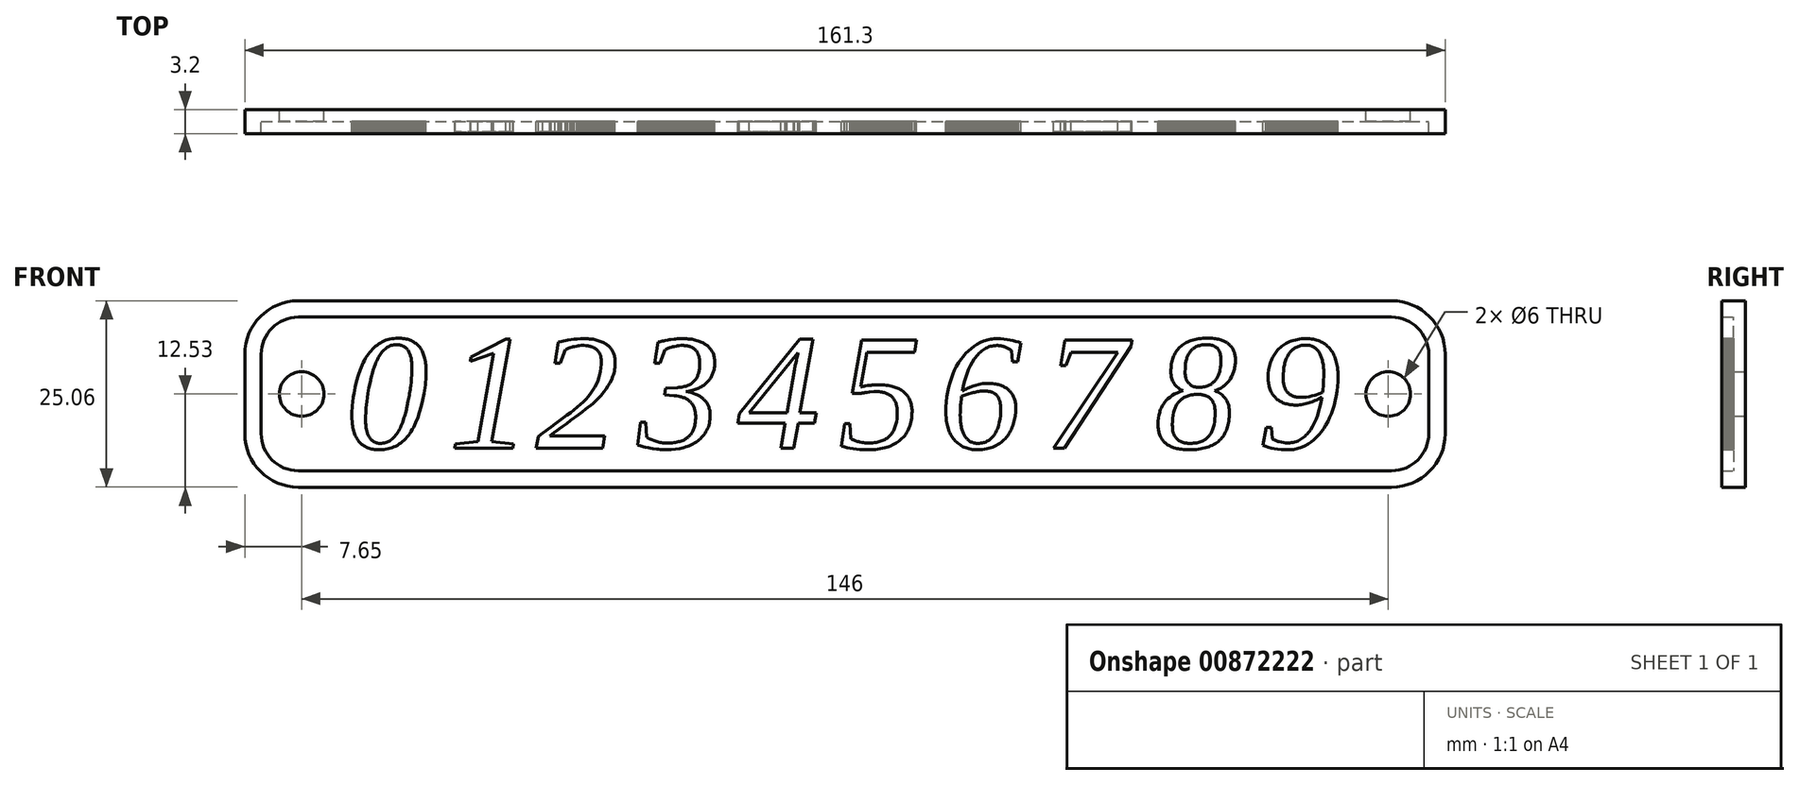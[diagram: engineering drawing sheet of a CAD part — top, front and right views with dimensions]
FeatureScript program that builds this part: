
annotation { "Feature Type Name" : "Feature", "Feature Type Description" : "" }
export const myFeature = defineFeature(function(context is Context, id is Id, definition is map)
    precondition{}
    {
        {
            var Q0;
            Q0=qCreatedBy(makeId("Front.planeOp"),FACE);
            var sketch = newSketch(context, id + "F0", { "sketchPlane" : qUnion([Q0])});
            skLineSegment(sketch, "E0", {"start": v(-109.12, 0) * mm, "end": v(57, 0) * mm, "construction": true});
            skPoint(sketch, "E0.startSnap0", {"position": v(-80, 0) * mm});
            skPoint(sketch, "E0.endSnap0", {"position": v(24, 0) * mm});
            skCircle(sketch, "E1", {"center": v(-73, 0) * mm, "radius": 3 * mm});
            skCircle(sketch, "E2", {"center": v(73, 0) * mm, "radius": 3 * mm});
            skLineSegment(sketch, "E3", {"start": v(-56.56, 0.05) * mm, "end": v(-56.74, -0.83) * mm});
            skLineSegment(sketch, "E4", {"start": v(-56.74, -0.83) * mm, "end": v(-56.94, -1.67) * mm});
            skLineSegment(sketch, "E5", {"start": v(-56.94, -1.67) * mm, "end": v(-57.16, -2.45) * mm});
            skLineSegment(sketch, "E6", {"start": v(-57.16, -2.45) * mm, "end": v(-57.4, -3.18) * mm});
            skLineSegment(sketch, "E7", {"start": v(-57.4, -3.18) * mm, "end": v(-57.68, -3.86) * mm});
            skLineSegment(sketch, "E8", {"start": v(-57.68, -3.86) * mm, "end": v(-57.82, -4.18) * mm});
            skLineSegment(sketch, "E9", {"start": v(-57.82, -4.18) * mm, "end": v(-57.98, -4.48) * mm});
            skLineSegment(sketch, "E10", {"start": v(-57.98, -4.48) * mm, "end": v(-58.13, -4.77) * mm});
            skLineSegment(sketch, "E11", {"start": v(-58.13, -4.77) * mm, "end": v(-58.3, -5.05) * mm});
            skLineSegment(sketch, "E12", {"start": v(-58.3, -5.05) * mm, "end": v(-58.48, -5.3) * mm});
            skLineSegment(sketch, "E13", {"start": v(-58.48, -5.3) * mm, "end": v(-58.66, -5.56) * mm});
            skLineSegment(sketch, "E14", {"start": v(-58.66, -5.56) * mm, "end": v(-58.84, -5.79) * mm});
            skLineSegment(sketch, "E15", {"start": v(-58.84, -5.79) * mm, "end": v(-59.04, -6) * mm});
            skLineSegment(sketch, "E16", {"start": v(-59.04, -6) * mm, "end": v(-59.24, -6.2) * mm});
            skLineSegment(sketch, "E17", {"start": v(-59.24, -6.2) * mm, "end": v(-59.45, -6.4) * mm});
            skLineSegment(sketch, "E18", {"start": v(-59.45, -6.4) * mm, "end": v(-59.67, -6.57) * mm});
            skLineSegment(sketch, "E19", {"start": v(-59.67, -6.57) * mm, "end": v(-59.9, -6.73) * mm});
            skLineSegment(sketch, "E20", {"start": v(-59.9, -6.73) * mm, "end": v(-60.13, -6.88) * mm});
            skLineSegment(sketch, "E21", {"start": v(-60.13, -6.88) * mm, "end": v(-60.37, -7.01) * mm});
            skLineSegment(sketch, "E22", {"start": v(-60.37, -7.01) * mm, "end": v(-60.62, -7.13) * mm});
            skLineSegment(sketch, "E23", {"start": v(-60.62, -7.13) * mm, "end": v(-60.87, -7.23) * mm});
            skLineSegment(sketch, "E24", {"start": v(-60.87, -7.23) * mm, "end": v(-61.13, -7.3) * mm});
            skLineSegment(sketch, "E25", {"start": v(-61.13, -7.3) * mm, "end": v(-61.4, -7.38) * mm});
            skLineSegment(sketch, "E26", {"start": v(-61.4, -7.38) * mm, "end": v(-61.68, -7.43) * mm});
            skLineSegment(sketch, "E27", {"start": v(-61.68, -7.43) * mm, "end": v(-61.97, -7.47) * mm});
            skLineSegment(sketch, "E28", {"start": v(-61.97, -7.47) * mm, "end": v(-62.26, -7.5) * mm});
            skLineSegment(sketch, "E29", {"start": v(-62.26, -7.5) * mm, "end": v(-62.56, -7.5) * mm});
            skLineSegment(sketch, "E30", {"start": v(-62.56, -7.5) * mm, "end": v(-62.79, -7.5) * mm});
            skLineSegment(sketch, "E31", {"start": v(-62.79, -7.5) * mm, "end": v(-63, -7.48) * mm});
            skLineSegment(sketch, "E32", {"start": v(-63, -7.48) * mm, "end": v(-63.2, -7.46) * mm});
            skLineSegment(sketch, "E33", {"start": v(-63.2, -7.46) * mm, "end": v(-63.41, -7.43) * mm});
            skLineSegment(sketch, "E34", {"start": v(-63.41, -7.43) * mm, "end": v(-63.6, -7.4) * mm});
            skLineSegment(sketch, "E35", {"start": v(-63.6, -7.4) * mm, "end": v(-63.8, -7.34) * mm});
            skLineSegment(sketch, "E36", {"start": v(-63.8, -7.34) * mm, "end": v(-63.98, -7.29) * mm});
            skLineSegment(sketch, "E37", {"start": v(-63.98, -7.29) * mm, "end": v(-64.15, -7.22) * mm});
            skLineSegment(sketch, "E38", {"start": v(-64.15, -7.22) * mm, "end": v(-64.32, -7.15) * mm});
            skLineSegment(sketch, "E39", {"start": v(-64.32, -7.15) * mm, "end": v(-64.48, -7.06) * mm});
            skLineSegment(sketch, "E40", {"start": v(-64.48, -7.06) * mm, "end": v(-64.64, -6.97) * mm});
            skLineSegment(sketch, "E41", {"start": v(-64.64, -6.97) * mm, "end": v(-64.78, -6.87) * mm});
            skLineSegment(sketch, "E42", {"start": v(-64.78, -6.87) * mm, "end": v(-64.93, -6.76) * mm});
            skLineSegment(sketch, "E43", {"start": v(-64.93, -6.76) * mm, "end": v(-65.06, -6.64) * mm});
            skLineSegment(sketch, "E44", {"start": v(-65.06, -6.64) * mm, "end": v(-65.19, -6.52) * mm});
            skLineSegment(sketch, "E45", {"start": v(-65.19, -6.52) * mm, "end": v(-65.3, -6.38) * mm});
            skLineSegment(sketch, "E46", {"start": v(-65.3, -6.38) * mm, "end": v(-65.42, -6.24) * mm});
            skLineSegment(sketch, "E47", {"start": v(-65.42, -6.24) * mm, "end": v(-65.53, -6.08) * mm});
            skLineSegment(sketch, "E48", {"start": v(-65.53, -6.08) * mm, "end": v(-65.63, -5.92) * mm});
            skLineSegment(sketch, "E49", {"start": v(-65.63, -5.92) * mm, "end": v(-65.72, -5.74) * mm});
            skLineSegment(sketch, "E50", {"start": v(-65.72, -5.74) * mm, "end": v(-65.8, -5.56) * mm});
            skLineSegment(sketch, "E51", {"start": v(-65.8, -5.56) * mm, "end": v(-65.88, -5.37) * mm});
            skLineSegment(sketch, "E52", {"start": v(-65.88, -5.37) * mm, "end": v(-65.95, -5.17) * mm});
            skLineSegment(sketch, "E53", {"start": v(-65.95, -5.17) * mm, "end": v(-66.02, -4.96) * mm});
            skLineSegment(sketch, "E54", {"start": v(-66.02, -4.96) * mm, "end": v(-66.07, -4.74) * mm});
            skLineSegment(sketch, "E55", {"start": v(-66.07, -4.74) * mm, "end": v(-66.12, -4.51) * mm});
            skLineSegment(sketch, "E56", {"start": v(-66.12, -4.51) * mm, "end": v(-66.16, -4.28) * mm});
            skLineSegment(sketch, "E57", {"start": v(-66.16, -4.28) * mm, "end": v(-66.2, -4.03) * mm});
            skLineSegment(sketch, "E58", {"start": v(-66.2, -4.03) * mm, "end": v(-66.22, -3.77) * mm});
            skLineSegment(sketch, "E59", {"start": v(-66.22, -3.77) * mm, "end": v(-66.25, -3.24) * mm});
            skLineSegment(sketch, "E60", {"start": v(-66.25, -3.24) * mm, "end": v(-66.25, -2.95) * mm});
            skLineSegment(sketch, "E61", {"start": v(-66.25, -2.95) * mm, "end": v(-66.25, -2.62) * mm});
            skLineSegment(sketch, "E62", {"start": v(-66.25, -2.62) * mm, "end": v(-66.24, -2.28) * mm});
            skLineSegment(sketch, "E63", {"start": v(-66.24, -2.28) * mm, "end": v(-66.22, -1.92) * mm});
            skLineSegment(sketch, "E64", {"start": v(-66.22, -1.92) * mm, "end": v(-66.19, -1.54) * mm});
            skLineSegment(sketch, "E65", {"start": v(-66.19, -1.54) * mm, "end": v(-66.15, -1.15) * mm});
            skLineSegment(sketch, "E66", {"start": v(-66.15, -1.15) * mm, "end": v(-66.05, -0.35) * mm});
            skLineSegment(sketch, "E67", {"start": v(-66.05, -0.35) * mm, "end": v(-65.98, 0.05) * mm});
            skLineSegment(sketch, "E68", {"start": v(-65.98, 0.05) * mm, "end": v(-65.8, 0.93) * mm});
            skLineSegment(sketch, "E69", {"start": v(-65.8, 0.93) * mm, "end": v(-65.6, 1.75) * mm});
            skLineSegment(sketch, "E70", {"start": v(-65.6, 1.75) * mm, "end": v(-65.38, 2.52) * mm});
            skLineSegment(sketch, "E71", {"start": v(-65.38, 2.52) * mm, "end": v(-65.14, 3.25) * mm});
            skLineSegment(sketch, "E72", {"start": v(-65.14, 3.25) * mm, "end": v(-64.86, 3.91) * mm});
            skLineSegment(sketch, "E73", {"start": v(-64.86, 3.91) * mm, "end": v(-64.71, 4.22) * mm});
            skLineSegment(sketch, "E74", {"start": v(-64.71, 4.22) * mm, "end": v(-64.56, 4.52) * mm});
            skLineSegment(sketch, "E75", {"start": v(-64.56, 4.52) * mm, "end": v(-64.4, 4.8) * mm});
            skLineSegment(sketch, "E76", {"start": v(-64.4, 4.8) * mm, "end": v(-64.23, 5.08) * mm});
            skLineSegment(sketch, "E77", {"start": v(-64.23, 5.08) * mm, "end": v(-64.06, 5.34) * mm});
            skLineSegment(sketch, "E78", {"start": v(-64.06, 5.34) * mm, "end": v(-63.88, 5.58) * mm});
            skLineSegment(sketch, "E79", {"start": v(-63.88, 5.58) * mm, "end": v(-63.69, 5.8) * mm});
            skLineSegment(sketch, "E80", {"start": v(-63.69, 5.8) * mm, "end": v(-63.5, 6.02) * mm});
            skLineSegment(sketch, "E81", {"start": v(-63.5, 6.02) * mm, "end": v(-63.3, 6.22) * mm});
            skLineSegment(sketch, "E82", {"start": v(-63.3, 6.22) * mm, "end": v(-63.08, 6.4) * mm});
            skLineSegment(sketch, "E83", {"start": v(-63.08, 6.4) * mm, "end": v(-62.87, 6.58) * mm});
            skLineSegment(sketch, "E84", {"start": v(-62.87, 6.58) * mm, "end": v(-62.65, 6.74) * mm});
            skLineSegment(sketch, "E85", {"start": v(-62.65, 6.74) * mm, "end": v(-62.42, 6.88) * mm});
            skLineSegment(sketch, "E86", {"start": v(-62.42, 6.88) * mm, "end": v(-62.18, 7.01) * mm});
            skLineSegment(sketch, "E87", {"start": v(-62.18, 7.01) * mm, "end": v(-61.94, 7.13) * mm});
            skLineSegment(sketch, "E88", {"start": v(-61.94, 7.13) * mm, "end": v(-61.7, 7.23) * mm});
            skLineSegment(sketch, "E89", {"start": v(-61.7, 7.23) * mm, "end": v(-61.43, 7.3) * mm});
            skLineSegment(sketch, "E90", {"start": v(-61.43, 7.3) * mm, "end": v(-61.17, 7.38) * mm});
            skLineSegment(sketch, "E91", {"start": v(-61.17, 7.38) * mm, "end": v(-60.9, 7.43) * mm});
            skLineSegment(sketch, "E92", {"start": v(-60.9, 7.43) * mm, "end": v(-60.62, 7.47) * mm});
            skLineSegment(sketch, "E93", {"start": v(-60.62, 7.47) * mm, "end": v(-60.33, 7.5) * mm});
            skLineSegment(sketch, "E94", {"start": v(-60.33, 7.5) * mm, "end": v(-60.03, 7.5) * mm});
            skLineSegment(sketch, "E95", {"start": v(-60.03, 7.5) * mm, "end": v(-59.81, 7.5) * mm});
            skLineSegment(sketch, "E96", {"start": v(-59.81, 7.5) * mm, "end": v(-59.6, 7.48) * mm});
            skLineSegment(sketch, "E97", {"start": v(-59.6, 7.48) * mm, "end": v(-59.39, 7.46) * mm});
            skLineSegment(sketch, "E98", {"start": v(-59.39, 7.46) * mm, "end": v(-59.19, 7.43) * mm});
            skLineSegment(sketch, "E99", {"start": v(-59.19, 7.43) * mm, "end": v(-58.99, 7.4) * mm});
            skLineSegment(sketch, "E100", {"start": v(-58.99, 7.4) * mm, "end": v(-58.8, 7.35) * mm});
            skLineSegment(sketch, "E101", {"start": v(-58.8, 7.35) * mm, "end": v(-58.62, 7.3) * mm});
            skLineSegment(sketch, "E102", {"start": v(-58.62, 7.3) * mm, "end": v(-58.44, 7.23) * mm});
            skLineSegment(sketch, "E103", {"start": v(-58.44, 7.23) * mm, "end": v(-58.27, 7.16) * mm});
            skLineSegment(sketch, "E104", {"start": v(-58.27, 7.16) * mm, "end": v(-58.1, 7.08) * mm});
            skLineSegment(sketch, "E105", {"start": v(-58.1, 7.08) * mm, "end": v(-57.95, 6.99) * mm});
            skLineSegment(sketch, "E106", {"start": v(-57.95, 6.99) * mm, "end": v(-57.8, 6.89) * mm});
            skLineSegment(sketch, "E107", {"start": v(-57.8, 6.89) * mm, "end": v(-57.65, 6.78) * mm});
            skLineSegment(sketch, "E108", {"start": v(-57.65, 6.78) * mm, "end": v(-57.51, 6.67) * mm});
            skLineSegment(sketch, "E109", {"start": v(-57.51, 6.67) * mm, "end": v(-57.38, 6.55) * mm});
            skLineSegment(sketch, "E110", {"start": v(-57.38, 6.55) * mm, "end": v(-57.26, 6.41) * mm});
            skLineSegment(sketch, "E111", {"start": v(-57.26, 6.41) * mm, "end": v(-57.14, 6.27) * mm});
            skLineSegment(sketch, "E112", {"start": v(-57.14, 6.27) * mm, "end": v(-57.03, 6.12) * mm});
            skLineSegment(sketch, "E113", {"start": v(-57.03, 6.12) * mm, "end": v(-56.92, 5.97) * mm});
            skLineSegment(sketch, "E114", {"start": v(-56.92, 5.97) * mm, "end": v(-56.83, 5.8) * mm});
            skLineSegment(sketch, "E115", {"start": v(-56.83, 5.8) * mm, "end": v(-56.74, 5.62) * mm});
            skLineSegment(sketch, "E116", {"start": v(-56.74, 5.62) * mm, "end": v(-56.66, 5.43) * mm});
            skLineSegment(sketch, "E117", {"start": v(-56.66, 5.43) * mm, "end": v(-56.59, 5.23) * mm});
            skLineSegment(sketch, "E118", {"start": v(-56.59, 5.23) * mm, "end": v(-56.52, 5.03) * mm});
            skLineSegment(sketch, "E119", {"start": v(-56.52, 5.03) * mm, "end": v(-56.47, 4.81) * mm});
            skLineSegment(sketch, "E120", {"start": v(-56.47, 4.81) * mm, "end": v(-56.42, 4.59) * mm});
            skLineSegment(sketch, "E121", {"start": v(-56.42, 4.59) * mm, "end": v(-56.37, 4.35) * mm});
            skLineSegment(sketch, "E122", {"start": v(-56.37, 4.35) * mm, "end": v(-56.34, 4.1) * mm});
            skLineSegment(sketch, "E123", {"start": v(-56.34, 4.1) * mm, "end": v(-56.31, 3.86) * mm});
            skLineSegment(sketch, "E124", {"start": v(-56.31, 3.86) * mm, "end": v(-56.3, 3.6) * mm});
            skLineSegment(sketch, "E125", {"start": v(-56.3, 3.6) * mm, "end": v(-56.28, 3.32) * mm});
            skLineSegment(sketch, "E126", {"start": v(-56.28, 3.32) * mm, "end": v(-56.28, 3.04) * mm});
            skLineSegment(sketch, "E127", {"start": v(-56.28, 3.04) * mm, "end": v(-56.28, 2.71) * mm});
            skLineSegment(sketch, "E128", {"start": v(-56.28, 2.71) * mm, "end": v(-56.3, 2.37) * mm});
            skLineSegment(sketch, "E129", {"start": v(-56.3, 2.37) * mm, "end": v(-56.32, 2) * mm});
            skLineSegment(sketch, "E130", {"start": v(-56.32, 2) * mm, "end": v(-56.36, 1.62) * mm});
            skLineSegment(sketch, "E131", {"start": v(-56.36, 1.62) * mm, "end": v(-56.4, 1.23) * mm});
            skLineSegment(sketch, "E132", {"start": v(-56.4, 1.23) * mm, "end": v(-56.5, 0.45) * mm});
            skLineSegment(sketch, "E133", {"start": v(-56.5, 0.45) * mm, "end": v(-56.56, 0.05) * mm});
            skLineSegment(sketch, "E134", {"start": v(-58.54, -0.18) * mm, "end": v(-58.5, 0.08) * mm});
            skLineSegment(sketch, "E135", {"start": v(-58.5, 0.08) * mm, "end": v(-58.42, 0.6) * mm});
            skLineSegment(sketch, "E136", {"start": v(-58.42, 0.6) * mm, "end": v(-58.38, 0.85) * mm});
            skLineSegment(sketch, "E137", {"start": v(-58.38, 0.85) * mm, "end": v(-58.35, 1.1) * mm});
            skLineSegment(sketch, "E138", {"start": v(-58.35, 1.1) * mm, "end": v(-58.29, 1.6) * mm});
            skLineSegment(sketch, "E139", {"start": v(-58.29, 1.6) * mm, "end": v(-58.27, 1.85) * mm});
            skLineSegment(sketch, "E140", {"start": v(-58.27, 1.85) * mm, "end": v(-58.24, 2.08) * mm});
            skLineSegment(sketch, "E141", {"start": v(-58.24, 2.08) * mm, "end": v(-58.21, 2.52) * mm});
            skLineSegment(sketch, "E142", {"start": v(-58.21, 2.52) * mm, "end": v(-58.2, 2.74) * mm});
            skLineSegment(sketch, "E143", {"start": v(-58.2, 2.74) * mm, "end": v(-58.2, 2.94) * mm});
            skLineSegment(sketch, "E144", {"start": v(-58.2, 2.94) * mm, "end": v(-58.18, 3.13) * mm});
            skLineSegment(sketch, "E145", {"start": v(-58.18, 3.13) * mm, "end": v(-58.18, 3.32) * mm});
            skLineSegment(sketch, "E146", {"start": v(-58.18, 3.32) * mm, "end": v(-58.18, 3.48) * mm});
            skLineSegment(sketch, "E147", {"start": v(-58.18, 3.48) * mm, "end": v(-58.19, 3.84) * mm});
            skLineSegment(sketch, "E148", {"start": v(-58.19, 3.84) * mm, "end": v(-58.2, 4.18) * mm});
            skLineSegment(sketch, "E149", {"start": v(-58.2, 4.18) * mm, "end": v(-58.25, 4.5) * mm});
            skLineSegment(sketch, "E150", {"start": v(-58.25, 4.5) * mm, "end": v(-58.3, 4.8) * mm});
            skLineSegment(sketch, "E151", {"start": v(-58.3, 4.8) * mm, "end": v(-58.33, 4.95) * mm});
            skLineSegment(sketch, "E152", {"start": v(-58.33, 4.95) * mm, "end": v(-58.37, 5.09) * mm});
            skLineSegment(sketch, "E153", {"start": v(-58.37, 5.09) * mm, "end": v(-58.4, 5.22) * mm});
            skLineSegment(sketch, "E154", {"start": v(-58.4, 5.22) * mm, "end": v(-58.45, 5.35) * mm});
            skLineSegment(sketch, "E155", {"start": v(-58.45, 5.35) * mm, "end": v(-58.5, 5.47) * mm});
            skLineSegment(sketch, "E156", {"start": v(-58.5, 5.47) * mm, "end": v(-58.56, 5.58) * mm});
            skLineSegment(sketch, "E157", {"start": v(-58.56, 5.58) * mm, "end": v(-58.61, 5.7) * mm});
            skLineSegment(sketch, "E158", {"start": v(-58.61, 5.7) * mm, "end": v(-58.68, 5.8) * mm});
            skLineSegment(sketch, "E159", {"start": v(-58.68, 5.8) * mm, "end": v(-58.74, 5.9) * mm});
            skLineSegment(sketch, "E160", {"start": v(-58.74, 5.9) * mm, "end": v(-58.81, 5.99) * mm});
            skLineSegment(sketch, "E161", {"start": v(-58.81, 5.99) * mm, "end": v(-58.88, 6.08) * mm});
            skLineSegment(sketch, "E162", {"start": v(-58.88, 6.08) * mm, "end": v(-58.96, 6.16) * mm});
            skLineSegment(sketch, "E163", {"start": v(-58.96, 6.16) * mm, "end": v(-59.04, 6.23) * mm});
            skLineSegment(sketch, "E164", {"start": v(-59.04, 6.23) * mm, "end": v(-59.13, 6.3) * mm});
            skLineSegment(sketch, "E165", {"start": v(-59.13, 6.3) * mm, "end": v(-59.22, 6.36) * mm});
            skLineSegment(sketch, "E166", {"start": v(-59.22, 6.36) * mm, "end": v(-59.32, 6.41) * mm});
            skLineSegment(sketch, "E167", {"start": v(-59.32, 6.41) * mm, "end": v(-59.42, 6.47) * mm});
            skLineSegment(sketch, "E168", {"start": v(-59.42, 6.47) * mm, "end": v(-59.52, 6.5) * mm});
            skLineSegment(sketch, "E169", {"start": v(-59.52, 6.5) * mm, "end": v(-59.62, 6.55) * mm});
            skLineSegment(sketch, "E170", {"start": v(-59.62, 6.55) * mm, "end": v(-59.74, 6.58) * mm});
            skLineSegment(sketch, "E171", {"start": v(-59.74, 6.58) * mm, "end": v(-59.85, 6.6) * mm});
            skLineSegment(sketch, "E172", {"start": v(-59.85, 6.6) * mm, "end": v(-59.97, 6.62) * mm});
            skLineSegment(sketch, "E173", {"start": v(-59.97, 6.62) * mm, "end": v(-60.1, 6.63) * mm});
            skLineSegment(sketch, "E174", {"start": v(-60.1, 6.63) * mm, "end": v(-60.23, 6.63) * mm});
            skLineSegment(sketch, "E175", {"start": v(-60.23, 6.63) * mm, "end": v(-60.43, 6.62) * mm});
            skLineSegment(sketch, "E176", {"start": v(-60.43, 6.62) * mm, "end": v(-60.62, 6.6) * mm});
            skLineSegment(sketch, "E177", {"start": v(-60.62, 6.6) * mm, "end": v(-60.8, 6.57) * mm});
            skLineSegment(sketch, "E178", {"start": v(-60.8, 6.57) * mm, "end": v(-60.98, 6.52) * mm});
            skLineSegment(sketch, "E179", {"start": v(-60.98, 6.52) * mm, "end": v(-61.15, 6.46) * mm});
            skLineSegment(sketch, "E180", {"start": v(-61.15, 6.46) * mm, "end": v(-61.32, 6.38) * mm});
            skLineSegment(sketch, "E181", {"start": v(-61.32, 6.38) * mm, "end": v(-61.48, 6.3) * mm});
            skLineSegment(sketch, "E182", {"start": v(-61.48, 6.3) * mm, "end": v(-61.63, 6.19) * mm});
            skLineSegment(sketch, "E183", {"start": v(-61.63, 6.19) * mm, "end": v(-61.78, 6.07) * mm});
            skLineSegment(sketch, "E184", {"start": v(-61.78, 6.07) * mm, "end": v(-61.92, 5.94) * mm});
            skLineSegment(sketch, "E185", {"start": v(-61.92, 5.94) * mm, "end": v(-62.06, 5.8) * mm});
            skLineSegment(sketch, "E186", {"start": v(-62.06, 5.8) * mm, "end": v(-62.2, 5.65) * mm});
            skLineSegment(sketch, "E187", {"start": v(-62.2, 5.65) * mm, "end": v(-62.32, 5.49) * mm});
            skLineSegment(sketch, "E188", {"start": v(-62.32, 5.49) * mm, "end": v(-62.45, 5.3) * mm});
            skLineSegment(sketch, "E189", {"start": v(-62.45, 5.3) * mm, "end": v(-62.57, 5.12) * mm});
            skLineSegment(sketch, "E190", {"start": v(-62.57, 5.12) * mm, "end": v(-62.68, 4.92) * mm});
            skLineSegment(sketch, "E191", {"start": v(-62.68, 4.92) * mm, "end": v(-62.8, 4.7) * mm});
            skLineSegment(sketch, "E192", {"start": v(-62.8, 4.7) * mm, "end": v(-62.9, 4.47) * mm});
            skLineSegment(sketch, "E193", {"start": v(-62.9, 4.47) * mm, "end": v(-63, 4.24) * mm});
            skLineSegment(sketch, "E194", {"start": v(-63, 4.24) * mm, "end": v(-63.11, 3.98) * mm});
            skLineSegment(sketch, "E195", {"start": v(-63.11, 3.98) * mm, "end": v(-63.21, 3.72) * mm});
            skLineSegment(sketch, "E196", {"start": v(-63.21, 3.72) * mm, "end": v(-63.4, 3.16) * mm});
            skLineSegment(sketch, "E197", {"start": v(-63.4, 3.16) * mm, "end": v(-63.49, 2.85) * mm});
            skLineSegment(sketch, "E198", {"start": v(-63.49, 2.85) * mm, "end": v(-63.65, 2.22) * mm});
            skLineSegment(sketch, "E199", {"start": v(-63.65, 2.22) * mm, "end": v(-63.8, 1.54) * mm});
            skLineSegment(sketch, "E200", {"start": v(-63.8, 1.54) * mm, "end": v(-63.95, 0.83) * mm});
            skLineSegment(sketch, "E201", {"start": v(-63.95, 0.83) * mm, "end": v(-64.1, 0.07) * mm});
            skLineSegment(sketch, "E202", {"start": v(-64.1, 0.07) * mm, "end": v(-64.18, -0.48) * mm});
            skLineSegment(sketch, "E203", {"start": v(-64.18, -0.48) * mm, "end": v(-64.26, -0.99) * mm});
            skLineSegment(sketch, "E204", {"start": v(-64.26, -0.99) * mm, "end": v(-64.31, -1.47) * mm});
            skLineSegment(sketch, "E205", {"start": v(-64.31, -1.47) * mm, "end": v(-64.35, -1.91) * mm});
            skLineSegment(sketch, "E206", {"start": v(-64.35, -1.91) * mm, "end": v(-64.38, -2.33) * mm});
            skLineSegment(sketch, "E207", {"start": v(-64.38, -2.33) * mm, "end": v(-64.4, -3.15) * mm});
            skLineSegment(sketch, "E208", {"start": v(-64.4, -3.15) * mm, "end": v(-64.4, -3.54) * mm});
            skLineSegment(sketch, "E209", {"start": v(-64.4, -3.54) * mm, "end": v(-64.4, -3.88) * mm});
            skLineSegment(sketch, "E210", {"start": v(-64.4, -3.88) * mm, "end": v(-64.38, -4.2) * mm});
            skLineSegment(sketch, "E211", {"start": v(-64.38, -4.2) * mm, "end": v(-64.35, -4.51) * mm});
            skLineSegment(sketch, "E212", {"start": v(-64.35, -4.51) * mm, "end": v(-64.3, -4.8) * mm});
            skLineSegment(sketch, "E213", {"start": v(-64.3, -4.8) * mm, "end": v(-64.27, -4.95) * mm});
            skLineSegment(sketch, "E214", {"start": v(-64.27, -4.95) * mm, "end": v(-64.23, -5.09) * mm});
            skLineSegment(sketch, "E215", {"start": v(-64.23, -5.09) * mm, "end": v(-64.2, -5.22) * mm});
            skLineSegment(sketch, "E216", {"start": v(-64.2, -5.22) * mm, "end": v(-64.15, -5.34) * mm});
            skLineSegment(sketch, "E217", {"start": v(-64.15, -5.34) * mm, "end": v(-64.1, -5.46) * mm});
            skLineSegment(sketch, "E218", {"start": v(-64.1, -5.46) * mm, "end": v(-64.05, -5.58) * mm});
            skLineSegment(sketch, "E219", {"start": v(-64.05, -5.58) * mm, "end": v(-64, -5.7) * mm});
            skLineSegment(sketch, "E220", {"start": v(-64, -5.7) * mm, "end": v(-63.94, -5.8) * mm});
            skLineSegment(sketch, "E221", {"start": v(-63.94, -5.8) * mm, "end": v(-63.88, -5.9) * mm});
            skLineSegment(sketch, "E222", {"start": v(-63.88, -5.9) * mm, "end": v(-63.8, -5.99) * mm});
            skLineSegment(sketch, "E223", {"start": v(-63.8, -5.99) * mm, "end": v(-63.74, -6.07) * mm});
            skLineSegment(sketch, "E224", {"start": v(-63.74, -6.07) * mm, "end": v(-63.66, -6.15) * mm});
            skLineSegment(sketch, "E225", {"start": v(-63.66, -6.15) * mm, "end": v(-63.58, -6.23) * mm});
            skLineSegment(sketch, "E226", {"start": v(-63.58, -6.23) * mm, "end": v(-63.5, -6.3) * mm});
            skLineSegment(sketch, "E227", {"start": v(-63.5, -6.3) * mm, "end": v(-63.41, -6.37) * mm});
            skLineSegment(sketch, "E228", {"start": v(-63.41, -6.37) * mm, "end": v(-63.32, -6.43) * mm});
            skLineSegment(sketch, "E229", {"start": v(-63.32, -6.43) * mm, "end": v(-63.23, -6.48) * mm});
            skLineSegment(sketch, "E230", {"start": v(-63.23, -6.48) * mm, "end": v(-63.13, -6.52) * mm});
            skLineSegment(sketch, "E231", {"start": v(-63.13, -6.52) * mm, "end": v(-63.03, -6.56) * mm});
            skLineSegment(sketch, "E232", {"start": v(-63.03, -6.56) * mm, "end": v(-62.92, -6.59) * mm});
            skLineSegment(sketch, "E233", {"start": v(-62.92, -6.59) * mm, "end": v(-62.8, -6.61) * mm});
            skLineSegment(sketch, "E234", {"start": v(-62.8, -6.61) * mm, "end": v(-62.68, -6.63) * mm});
            skLineSegment(sketch, "E235", {"start": v(-62.68, -6.63) * mm, "end": v(-62.56, -6.64) * mm});
            skLineSegment(sketch, "E236", {"start": v(-62.56, -6.64) * mm, "end": v(-62.43, -6.64) * mm});
            skLineSegment(sketch, "E237", {"start": v(-62.43, -6.64) * mm, "end": v(-62.24, -6.64) * mm});
            skLineSegment(sketch, "E238", {"start": v(-62.24, -6.64) * mm, "end": v(-62.05, -6.62) * mm});
            skLineSegment(sketch, "E239", {"start": v(-62.05, -6.62) * mm, "end": v(-61.86, -6.58) * mm});
            skLineSegment(sketch, "E240", {"start": v(-61.86, -6.58) * mm, "end": v(-61.69, -6.54) * mm});
            skLineSegment(sketch, "E241", {"start": v(-61.69, -6.54) * mm, "end": v(-61.51, -6.48) * mm});
            skLineSegment(sketch, "E242", {"start": v(-61.51, -6.48) * mm, "end": v(-61.35, -6.4) * mm});
            skLineSegment(sketch, "E243", {"start": v(-61.35, -6.4) * mm, "end": v(-61.19, -6.32) * mm});
            skLineSegment(sketch, "E244", {"start": v(-61.19, -6.32) * mm, "end": v(-61.03, -6.22) * mm});
            skLineSegment(sketch, "E245", {"start": v(-61.03, -6.22) * mm, "end": v(-60.88, -6.1) * mm});
            skLineSegment(sketch, "E246", {"start": v(-60.88, -6.1) * mm, "end": v(-60.74, -5.98) * mm});
            skLineSegment(sketch, "E247", {"start": v(-60.74, -5.98) * mm, "end": v(-60.6, -5.85) * mm});
            skLineSegment(sketch, "E248", {"start": v(-60.6, -5.85) * mm, "end": v(-60.46, -5.7) * mm});
            skLineSegment(sketch, "E249", {"start": v(-60.46, -5.7) * mm, "end": v(-60.33, -5.54) * mm});
            skLineSegment(sketch, "E250", {"start": v(-60.33, -5.54) * mm, "end": v(-60.2, -5.36) * mm});
            skLineSegment(sketch, "E251", {"start": v(-60.2, -5.36) * mm, "end": v(-60.09, -5.18) * mm});
            skLineSegment(sketch, "E252", {"start": v(-60.09, -5.18) * mm, "end": v(-59.97, -4.98) * mm});
            skLineSegment(sketch, "E253", {"start": v(-59.97, -4.98) * mm, "end": v(-59.85, -4.77) * mm});
            skLineSegment(sketch, "E254", {"start": v(-59.85, -4.77) * mm, "end": v(-59.74, -4.55) * mm});
            skLineSegment(sketch, "E255", {"start": v(-59.74, -4.55) * mm, "end": v(-59.64, -4.3) * mm});
            skLineSegment(sketch, "E256", {"start": v(-59.64, -4.3) * mm, "end": v(-59.54, -4.06) * mm});
            skLineSegment(sketch, "E257", {"start": v(-59.54, -4.06) * mm, "end": v(-59.44, -3.8) * mm});
            skLineSegment(sketch, "E258", {"start": v(-59.44, -3.8) * mm, "end": v(-59.25, -3.25) * mm});
            skLineSegment(sketch, "E259", {"start": v(-59.25, -3.25) * mm, "end": v(-59.17, -2.95) * mm});
            skLineSegment(sketch, "E260", {"start": v(-59.17, -2.95) * mm, "end": v(-59, -2.33) * mm});
            skLineSegment(sketch, "E261", {"start": v(-59, -2.33) * mm, "end": v(-58.84, -1.66) * mm});
            skLineSegment(sketch, "E262", {"start": v(-58.84, -1.66) * mm, "end": v(-58.68, -0.94) * mm});
            skLineSegment(sketch, "E263", {"start": v(-58.68, -0.94) * mm, "end": v(-58.54, -0.18) * mm});
            skLineSegment(sketch, "E264", {"start": v(-47.45, -6.41) * mm, "end": v(-44.52, -6.7) * mm});
            skLineSegment(sketch, "E265", {"start": v(-44.52, -6.7) * mm, "end": v(-44.63, -7.28) * mm});
            skLineSegment(sketch, "E266", {"start": v(-44.63, -7.28) * mm, "end": v(-52.46, -7.28) * mm});
            skLineSegment(sketch, "E267", {"start": v(-52.46, -7.28) * mm, "end": v(-52.35, -6.7) * mm});
            skLineSegment(sketch, "E268", {"start": v(-52.35, -6.7) * mm, "end": v(-49.32, -6.41) * mm});
            skLineSegment(sketch, "E269", {"start": v(-49.32, -6.41) * mm, "end": v(-47.23, 5.46) * mm});
            skLineSegment(sketch, "E270", {"start": v(-47.23, 5.46) * mm, "end": v(-50.35, 4.4) * mm});
            skLineSegment(sketch, "E271", {"start": v(-50.35, 4.4) * mm, "end": v(-50.24, 4.98) * mm});
            skLineSegment(sketch, "E272", {"start": v(-50.24, 4.98) * mm, "end": v(-45.58, 7.4) * mm});
            skLineSegment(sketch, "E273", {"start": v(-45.58, 7.4) * mm, "end": v(-45.01, 7.4) * mm});
            skLineSegment(sketch, "E274", {"start": v(-45.01, 7.4) * mm, "end": v(-47.45, -6.41) * mm});
            skLineSegment(sketch, "E275", {"start": v(-32.58, -7.28) * mm, "end": v(-41.48, -7.28) * mm});
            skLineSegment(sketch, "E276", {"start": v(-41.48, -7.28) * mm, "end": v(-41.2, -5.69) * mm});
            skLineSegment(sketch, "E277", {"start": v(-41.2, -5.69) * mm, "end": v(-40.6, -5.25) * mm});
            skLineSegment(sketch, "E278", {"start": v(-40.6, -5.25) * mm, "end": v(-39.45, -4.4) * mm});
            skLineSegment(sketch, "E279", {"start": v(-39.45, -4.4) * mm, "end": v(-38.9, -4.02) * mm});
            skLineSegment(sketch, "E280", {"start": v(-38.9, -4.02) * mm, "end": v(-38.36, -3.63) * mm});
            skLineSegment(sketch, "E281", {"start": v(-38.36, -3.63) * mm, "end": v(-37.35, -2.87) * mm});
            skLineSegment(sketch, "E282", {"start": v(-37.35, -2.87) * mm, "end": v(-36.87, -2.5) * mm});
            skLineSegment(sketch, "E283", {"start": v(-36.87, -2.5) * mm, "end": v(-36.4, -2.14) * mm});
            skLineSegment(sketch, "E284", {"start": v(-36.4, -2.14) * mm, "end": v(-35.56, -1.4) * mm});
            skLineSegment(sketch, "E285", {"start": v(-35.56, -1.4) * mm, "end": v(-35.17, -1.04) * mm});
            skLineSegment(sketch, "E286", {"start": v(-35.17, -1.04) * mm, "end": v(-34.8, -0.67) * mm});
            skLineSegment(sketch, "E287", {"start": v(-34.8, -0.67) * mm, "end": v(-34.46, -0.28) * mm});
            skLineSegment(sketch, "E288", {"start": v(-34.46, -0.28) * mm, "end": v(-34.15, 0.1) * mm});
            skLineSegment(sketch, "E289", {"start": v(-34.15, 0.1) * mm, "end": v(-33.87, 0.51) * mm});
            skLineSegment(sketch, "E290", {"start": v(-33.87, 0.51) * mm, "end": v(-33.62, 0.92) * mm});
            skLineSegment(sketch, "E291", {"start": v(-33.62, 0.92) * mm, "end": v(-33.4, 1.35) * mm});
            skLineSegment(sketch, "E292", {"start": v(-33.4, 1.35) * mm, "end": v(-33.2, 1.8) * mm});
            skLineSegment(sketch, "E293", {"start": v(-33.2, 1.8) * mm, "end": v(-33.04, 2.25) * mm});
            skLineSegment(sketch, "E294", {"start": v(-33.04, 2.25) * mm, "end": v(-32.97, 2.48) * mm});
            skLineSegment(sketch, "E295", {"start": v(-32.97, 2.48) * mm, "end": v(-32.9, 2.72) * mm});
            skLineSegment(sketch, "E296", {"start": v(-32.9, 2.72) * mm, "end": v(-32.86, 2.97) * mm});
            skLineSegment(sketch, "E297", {"start": v(-32.86, 2.97) * mm, "end": v(-32.79, 3.48) * mm});
            skLineSegment(sketch, "E298", {"start": v(-32.79, 3.48) * mm, "end": v(-32.75, 4.02) * mm});
            skLineSegment(sketch, "E299", {"start": v(-32.75, 4.02) * mm, "end": v(-32.74, 4.3) * mm});
            skLineSegment(sketch, "E300", {"start": v(-32.74, 4.3) * mm, "end": v(-32.75, 4.44) * mm});
            skLineSegment(sketch, "E301", {"start": v(-32.75, 4.44) * mm, "end": v(-32.75, 4.58) * mm});
            skLineSegment(sketch, "E302", {"start": v(-32.75, 4.58) * mm, "end": v(-32.77, 4.71) * mm});
            skLineSegment(sketch, "E303", {"start": v(-32.77, 4.71) * mm, "end": v(-32.78, 4.84) * mm});
            skLineSegment(sketch, "E304", {"start": v(-32.78, 4.84) * mm, "end": v(-32.8, 4.96) * mm});
            skLineSegment(sketch, "E305", {"start": v(-32.8, 4.96) * mm, "end": v(-32.83, 5.08) * mm});
            skLineSegment(sketch, "E306", {"start": v(-32.83, 5.08) * mm, "end": v(-32.87, 5.2) * mm});
            skLineSegment(sketch, "E307", {"start": v(-32.87, 5.2) * mm, "end": v(-32.9, 5.3) * mm});
            skLineSegment(sketch, "E308", {"start": v(-32.9, 5.3) * mm, "end": v(-32.94, 5.4) * mm});
            skLineSegment(sketch, "E309", {"start": v(-32.94, 5.4) * mm, "end": v(-33, 5.5) * mm});
            skLineSegment(sketch, "E310", {"start": v(-33, 5.5) * mm, "end": v(-33.04, 5.6) * mm});
            skLineSegment(sketch, "E311", {"start": v(-33.04, 5.6) * mm, "end": v(-33.1, 5.69) * mm});
            skLineSegment(sketch, "E312", {"start": v(-33.1, 5.69) * mm, "end": v(-33.16, 5.77) * mm});
            skLineSegment(sketch, "E313", {"start": v(-33.16, 5.77) * mm, "end": v(-33.23, 5.85) * mm});
            skLineSegment(sketch, "E314", {"start": v(-33.23, 5.85) * mm, "end": v(-33.3, 5.92) * mm});
            skLineSegment(sketch, "E315", {"start": v(-33.3, 5.92) * mm, "end": v(-33.37, 6) * mm});
            skLineSegment(sketch, "E316", {"start": v(-33.37, 6) * mm, "end": v(-33.46, 6.06) * mm});
            skLineSegment(sketch, "E317", {"start": v(-33.46, 6.06) * mm, "end": v(-33.54, 6.12) * mm});
            skLineSegment(sketch, "E318", {"start": v(-33.54, 6.12) * mm, "end": v(-33.63, 6.17) * mm});
            skLineSegment(sketch, "E319", {"start": v(-33.63, 6.17) * mm, "end": v(-33.73, 6.22) * mm});
            skLineSegment(sketch, "E320", {"start": v(-33.73, 6.22) * mm, "end": v(-33.82, 6.27) * mm});
            skLineSegment(sketch, "E321", {"start": v(-33.82, 6.27) * mm, "end": v(-33.93, 6.32) * mm});
            skLineSegment(sketch, "E322", {"start": v(-33.93, 6.32) * mm, "end": v(-34.04, 6.35) * mm});
            skLineSegment(sketch, "E323", {"start": v(-34.04, 6.35) * mm, "end": v(-34.15, 6.4) * mm});
            skLineSegment(sketch, "E324", {"start": v(-34.15, 6.4) * mm, "end": v(-34.27, 6.42) * mm});
            skLineSegment(sketch, "E325", {"start": v(-34.27, 6.42) * mm, "end": v(-34.4, 6.45) * mm});
            skLineSegment(sketch, "E326", {"start": v(-34.4, 6.45) * mm, "end": v(-34.52, 6.47) * mm});
            skLineSegment(sketch, "E327", {"start": v(-34.52, 6.47) * mm, "end": v(-34.65, 6.49) * mm});
            skLineSegment(sketch, "E328", {"start": v(-34.65, 6.49) * mm, "end": v(-34.78, 6.5) * mm});
            skLineSegment(sketch, "E329", {"start": v(-34.78, 6.5) * mm, "end": v(-35.07, 6.52) * mm});
            skLineSegment(sketch, "E330", {"start": v(-35.07, 6.52) * mm, "end": v(-35.22, 6.52) * mm});
            skLineSegment(sketch, "E331", {"start": v(-35.22, 6.52) * mm, "end": v(-35.38, 6.52) * mm});
            skLineSegment(sketch, "E332", {"start": v(-35.38, 6.52) * mm, "end": v(-35.71, 6.5) * mm});
            skLineSegment(sketch, "E333", {"start": v(-35.71, 6.5) * mm, "end": v(-35.88, 6.47) * mm});
            skLineSegment(sketch, "E334", {"start": v(-35.88, 6.47) * mm, "end": v(-36.04, 6.44) * mm});
            skLineSegment(sketch, "E335", {"start": v(-36.04, 6.44) * mm, "end": v(-36.36, 6.38) * mm});
            skLineSegment(sketch, "E336", {"start": v(-36.36, 6.38) * mm, "end": v(-36.52, 6.34) * mm});
            skLineSegment(sketch, "E337", {"start": v(-36.52, 6.34) * mm, "end": v(-36.67, 6.3) * mm});
            skLineSegment(sketch, "E338", {"start": v(-36.67, 6.3) * mm, "end": v(-36.96, 6.2) * mm});
            skLineSegment(sketch, "E339", {"start": v(-36.96, 6.2) * mm, "end": v(-37.1, 6.15) * mm});
            skLineSegment(sketch, "E340", {"start": v(-37.1, 6.15) * mm, "end": v(-37.23, 6.1) * mm});
            skLineSegment(sketch, "E341", {"start": v(-37.23, 6.1) * mm, "end": v(-37.35, 6.05) * mm});
            skLineSegment(sketch, "E342", {"start": v(-37.35, 6.05) * mm, "end": v(-37.47, 6) * mm});
            skLineSegment(sketch, "E343", {"start": v(-37.47, 6) * mm, "end": v(-37.57, 5.95) * mm});
            skLineSegment(sketch, "E344", {"start": v(-37.57, 5.95) * mm, "end": v(-38.27, 4.17) * mm});
            skLineSegment(sketch, "E345", {"start": v(-38.27, 4.17) * mm, "end": v(-38.99, 4.17) * mm});
            skLineSegment(sketch, "E346", {"start": v(-38.99, 4.17) * mm, "end": v(-38.5, 6.97) * mm});
            skLineSegment(sketch, "E347", {"start": v(-38.5, 6.97) * mm, "end": v(-38.07, 7.06) * mm});
            skLineSegment(sketch, "E348", {"start": v(-38.07, 7.06) * mm, "end": v(-37.23, 7.22) * mm});
            skLineSegment(sketch, "E349", {"start": v(-37.23, 7.22) * mm, "end": v(-36.81, 7.3) * mm});
            skLineSegment(sketch, "E350", {"start": v(-36.81, 7.3) * mm, "end": v(-36.4, 7.36) * mm});
            skLineSegment(sketch, "E351", {"start": v(-36.4, 7.36) * mm, "end": v(-35.96, 7.4) * mm});
            skLineSegment(sketch, "E352", {"start": v(-35.96, 7.4) * mm, "end": v(-35.52, 7.43) * mm});
            skLineSegment(sketch, "E353", {"start": v(-35.52, 7.43) * mm, "end": v(-35.06, 7.43) * mm});
            skLineSegment(sketch, "E354", {"start": v(-35.06, 7.43) * mm, "end": v(-34.55, 7.42) * mm});
            skLineSegment(sketch, "E355", {"start": v(-34.55, 7.42) * mm, "end": v(-34.3, 7.4) * mm});
            skLineSegment(sketch, "E356", {"start": v(-34.3, 7.4) * mm, "end": v(-34.07, 7.38) * mm});
            skLineSegment(sketch, "E357", {"start": v(-34.07, 7.38) * mm, "end": v(-33.85, 7.35) * mm});
            skLineSegment(sketch, "E358", {"start": v(-33.85, 7.35) * mm, "end": v(-33.63, 7.3) * mm});
            skLineSegment(sketch, "E359", {"start": v(-33.63, 7.3) * mm, "end": v(-33.42, 7.26) * mm});
            skLineSegment(sketch, "E360", {"start": v(-33.42, 7.26) * mm, "end": v(-33.22, 7.2) * mm});
            skLineSegment(sketch, "E361", {"start": v(-33.22, 7.2) * mm, "end": v(-33.03, 7.15) * mm});
            skLineSegment(sketch, "E362", {"start": v(-33.03, 7.15) * mm, "end": v(-32.84, 7.09) * mm});
            skLineSegment(sketch, "E363", {"start": v(-32.84, 7.09) * mm, "end": v(-32.67, 7.02) * mm});
            skLineSegment(sketch, "E364", {"start": v(-32.67, 7.02) * mm, "end": v(-32.5, 6.94) * mm});
            skLineSegment(sketch, "E365", {"start": v(-32.5, 6.94) * mm, "end": v(-32.34, 6.86) * mm});
            skLineSegment(sketch, "E366", {"start": v(-32.34, 6.86) * mm, "end": v(-32.19, 6.77) * mm});
            skLineSegment(sketch, "E367", {"start": v(-32.19, 6.77) * mm, "end": v(-32.04, 6.68) * mm});
            skLineSegment(sketch, "E368", {"start": v(-32.04, 6.68) * mm, "end": v(-31.9, 6.58) * mm});
            skLineSegment(sketch, "E369", {"start": v(-31.9, 6.58) * mm, "end": v(-31.78, 6.47) * mm});
            skLineSegment(sketch, "E370", {"start": v(-31.78, 6.47) * mm, "end": v(-31.66, 6.36) * mm});
            skLineSegment(sketch, "E371", {"start": v(-31.66, 6.36) * mm, "end": v(-31.55, 6.25) * mm});
            skLineSegment(sketch, "E372", {"start": v(-31.55, 6.25) * mm, "end": v(-31.45, 6.12) * mm});
            skLineSegment(sketch, "E373", {"start": v(-31.45, 6.12) * mm, "end": v(-31.36, 6) * mm});
            skLineSegment(sketch, "E374", {"start": v(-31.36, 6) * mm, "end": v(-31.27, 5.87) * mm});
            skLineSegment(sketch, "E375", {"start": v(-31.27, 5.87) * mm, "end": v(-31.2, 5.73) * mm});
            skLineSegment(sketch, "E376", {"start": v(-31.2, 5.73) * mm, "end": v(-31.13, 5.59) * mm});
            skLineSegment(sketch, "E377", {"start": v(-31.13, 5.59) * mm, "end": v(-31.07, 5.44) * mm});
            skLineSegment(sketch, "E378", {"start": v(-31.07, 5.44) * mm, "end": v(-31.01, 5.3) * mm});
            skLineSegment(sketch, "E379", {"start": v(-31.01, 5.3) * mm, "end": v(-30.97, 5.14) * mm});
            skLineSegment(sketch, "E380", {"start": v(-30.97, 5.14) * mm, "end": v(-30.93, 4.98) * mm});
            skLineSegment(sketch, "E381", {"start": v(-30.93, 4.98) * mm, "end": v(-30.9, 4.82) * mm});
            skLineSegment(sketch, "E382", {"start": v(-30.9, 4.82) * mm, "end": v(-30.88, 4.65) * mm});
            skLineSegment(sketch, "E383", {"start": v(-30.88, 4.65) * mm, "end": v(-30.87, 4.47) * mm});
            skLineSegment(sketch, "E384", {"start": v(-30.87, 4.47) * mm, "end": v(-30.87, 4.3) * mm});
            skLineSegment(sketch, "E385", {"start": v(-30.87, 4.3) * mm, "end": v(-30.89, 3.79) * mm});
            skLineSegment(sketch, "E386", {"start": v(-30.89, 3.79) * mm, "end": v(-30.91, 3.54) * mm});
            skLineSegment(sketch, "E387", {"start": v(-30.91, 3.54) * mm, "end": v(-30.95, 3.3) * mm});
            skLineSegment(sketch, "E388", {"start": v(-30.95, 3.3) * mm, "end": v(-31, 3.05) * mm});
            skLineSegment(sketch, "E389", {"start": v(-31, 3.05) * mm, "end": v(-31.05, 2.81) * mm});
            skLineSegment(sketch, "E390", {"start": v(-31.05, 2.81) * mm, "end": v(-31.12, 2.58) * mm});
            skLineSegment(sketch, "E391", {"start": v(-31.12, 2.58) * mm, "end": v(-31.2, 2.36) * mm});
            skLineSegment(sketch, "E392", {"start": v(-31.2, 2.36) * mm, "end": v(-31.37, 1.92) * mm});
            skLineSegment(sketch, "E393", {"start": v(-31.37, 1.92) * mm, "end": v(-31.58, 1.48) * mm});
            skLineSegment(sketch, "E394", {"start": v(-31.58, 1.48) * mm, "end": v(-31.83, 1.06) * mm});
            skLineSegment(sketch, "E395", {"start": v(-31.83, 1.06) * mm, "end": v(-32.1, 0.65) * mm});
            skLineSegment(sketch, "E396", {"start": v(-32.1, 0.65) * mm, "end": v(-32.4, 0.25) * mm});
            skLineSegment(sketch, "E397", {"start": v(-32.4, 0.25) * mm, "end": v(-32.74, -0.15) * mm});
            skLineSegment(sketch, "E398", {"start": v(-32.74, -0.15) * mm, "end": v(-33.1, -0.54) * mm});
            skLineSegment(sketch, "E399", {"start": v(-33.1, -0.54) * mm, "end": v(-33.5, -0.92) * mm});
            skLineSegment(sketch, "E400", {"start": v(-33.5, -0.92) * mm, "end": v(-33.91, -1.3) * mm});
            skLineSegment(sketch, "E401", {"start": v(-33.91, -1.3) * mm, "end": v(-34.81, -2.05) * mm});
            skLineSegment(sketch, "E402", {"start": v(-34.81, -2.05) * mm, "end": v(-35.3, -2.43) * mm});
            skLineSegment(sketch, "E403", {"start": v(-35.3, -2.43) * mm, "end": v(-35.8, -2.8) * mm});
            skLineSegment(sketch, "E404", {"start": v(-35.8, -2.8) * mm, "end": v(-36.84, -3.57) * mm});
            skLineSegment(sketch, "E405", {"start": v(-36.84, -3.57) * mm, "end": v(-37.4, -3.96) * mm});
            skLineSegment(sketch, "E406", {"start": v(-37.4, -3.96) * mm, "end": v(-37.95, -4.36) * mm});
            skLineSegment(sketch, "E407", {"start": v(-37.95, -4.36) * mm, "end": v(-39.1, -5.18) * mm});
            skLineSegment(sketch, "E408", {"start": v(-39.1, -5.18) * mm, "end": v(-39.7, -5.61) * mm});
            skLineSegment(sketch, "E409", {"start": v(-39.7, -5.61) * mm, "end": v(-32.29, -5.61) * mm});
            skLineSegment(sketch, "E410", {"start": v(-32.29, -5.61) * mm, "end": v(-32.58, -7.28) * mm});
            skLineSegment(sketch, "E411", {"start": v(-23.96, -7.5) * mm, "end": v(-24.23, -7.5) * mm});
            skLineSegment(sketch, "E412", {"start": v(-24.23, -7.5) * mm, "end": v(-24.77, -7.47) * mm});
            skLineSegment(sketch, "E413", {"start": v(-24.77, -7.47) * mm, "end": v(-25.05, -7.45) * mm});
            skLineSegment(sketch, "E414", {"start": v(-25.05, -7.45) * mm, "end": v(-25.32, -7.42) * mm});
            skLineSegment(sketch, "E415", {"start": v(-25.32, -7.42) * mm, "end": v(-25.85, -7.34) * mm});
            skLineSegment(sketch, "E416", {"start": v(-25.85, -7.34) * mm, "end": v(-26.11, -7.3) * mm});
            skLineSegment(sketch, "E417", {"start": v(-26.11, -7.3) * mm, "end": v(-26.36, -7.25) * mm});
            skLineSegment(sketch, "E418", {"start": v(-26.36, -7.25) * mm, "end": v(-26.85, -7.15) * mm});
            skLineSegment(sketch, "E419", {"start": v(-26.85, -7.15) * mm, "end": v(-27.08, -7.09) * mm});
            skLineSegment(sketch, "E420", {"start": v(-27.08, -7.09) * mm, "end": v(-27.3, -7.03) * mm});
            skLineSegment(sketch, "E421", {"start": v(-27.3, -7.03) * mm, "end": v(-27.5, -6.97) * mm});
            skLineSegment(sketch, "E422", {"start": v(-27.5, -6.97) * mm, "end": v(-27.69, -6.9) * mm});
            skLineSegment(sketch, "E423", {"start": v(-27.69, -6.9) * mm, "end": v(-27.87, -6.84) * mm});
            skLineSegment(sketch, "E424", {"start": v(-27.87, -6.84) * mm, "end": v(-27.47, -3.78) * mm});
            skLineSegment(sketch, "E425", {"start": v(-27.47, -3.78) * mm, "end": v(-26.75, -3.78) * mm});
            skLineSegment(sketch, "E426", {"start": v(-26.75, -3.78) * mm, "end": v(-26.62, -5.82) * mm});
            skLineSegment(sketch, "E427", {"start": v(-26.62, -5.82) * mm, "end": v(-26.57, -5.86) * mm});
            skLineSegment(sketch, "E428", {"start": v(-26.57, -5.86) * mm, "end": v(-26.52, -5.9) * mm});
            skLineSegment(sketch, "E429", {"start": v(-26.52, -5.9) * mm, "end": v(-26.46, -5.93) * mm});
            skLineSegment(sketch, "E430", {"start": v(-26.46, -5.93) * mm, "end": v(-26.4, -5.97) * mm});
            skLineSegment(sketch, "E431", {"start": v(-26.4, -5.97) * mm, "end": v(-26.33, -6) * mm});
            skLineSegment(sketch, "E432", {"start": v(-26.33, -6) * mm, "end": v(-26.26, -6.04) * mm});
            skLineSegment(sketch, "E433", {"start": v(-26.26, -6.04) * mm, "end": v(-26.19, -6.08) * mm});
            skLineSegment(sketch, "E434", {"start": v(-26.19, -6.08) * mm, "end": v(-26.11, -6.11) * mm});
            skLineSegment(sketch, "E435", {"start": v(-26.11, -6.11) * mm, "end": v(-25.95, -6.18) * mm});
            skLineSegment(sketch, "E436", {"start": v(-25.95, -6.18) * mm, "end": v(-25.6, -6.3) * mm});
            skLineSegment(sketch, "E437", {"start": v(-25.6, -6.3) * mm, "end": v(-25.43, -6.36) * mm});
            skLineSegment(sketch, "E438", {"start": v(-25.43, -6.36) * mm, "end": v(-25.24, -6.41) * mm});
            skLineSegment(sketch, "E439", {"start": v(-25.24, -6.41) * mm, "end": v(-24.87, -6.5) * mm});
            skLineSegment(sketch, "E440", {"start": v(-24.87, -6.5) * mm, "end": v(-24.68, -6.53) * mm});
            skLineSegment(sketch, "E441", {"start": v(-24.68, -6.53) * mm, "end": v(-24.49, -6.56) * mm});
            skLineSegment(sketch, "E442", {"start": v(-24.49, -6.56) * mm, "end": v(-24.3, -6.58) * mm});
            skLineSegment(sketch, "E443", {"start": v(-24.3, -6.58) * mm, "end": v(-24.13, -6.6) * mm});
            skLineSegment(sketch, "E444", {"start": v(-24.13, -6.6) * mm, "end": v(-23.96, -6.6) * mm});
            skLineSegment(sketch, "E445", {"start": v(-23.96, -6.6) * mm, "end": v(-23.7, -6.6) * mm});
            skLineSegment(sketch, "E446", {"start": v(-23.7, -6.6) * mm, "end": v(-23.46, -6.59) * mm});
            skLineSegment(sketch, "E447", {"start": v(-23.46, -6.59) * mm, "end": v(-23.22, -6.57) * mm});
            skLineSegment(sketch, "E448", {"start": v(-23.22, -6.57) * mm, "end": v(-22.99, -6.54) * mm});
            skLineSegment(sketch, "E449", {"start": v(-22.99, -6.54) * mm, "end": v(-22.77, -6.51) * mm});
            skLineSegment(sketch, "E450", {"start": v(-22.77, -6.51) * mm, "end": v(-22.56, -6.48) * mm});
            skLineSegment(sketch, "E451", {"start": v(-22.56, -6.48) * mm, "end": v(-22.36, -6.43) * mm});
            skLineSegment(sketch, "E452", {"start": v(-22.36, -6.43) * mm, "end": v(-22.17, -6.38) * mm});
            skLineSegment(sketch, "E453", {"start": v(-22.17, -6.38) * mm, "end": v(-22, -6.32) * mm});
            skLineSegment(sketch, "E454", {"start": v(-22, -6.32) * mm, "end": v(-21.82, -6.26) * mm});
            skLineSegment(sketch, "E455", {"start": v(-21.82, -6.26) * mm, "end": v(-21.66, -6.18) * mm});
            skLineSegment(sketch, "E456", {"start": v(-21.66, -6.18) * mm, "end": v(-21.5, -6.1) * mm});
            skLineSegment(sketch, "E457", {"start": v(-21.5, -6.1) * mm, "end": v(-21.35, -6.02) * mm});
            skLineSegment(sketch, "E458", {"start": v(-21.35, -6.02) * mm, "end": v(-21.22, -5.92) * mm});
            skLineSegment(sketch, "E459", {"start": v(-21.22, -5.92) * mm, "end": v(-21.09, -5.83) * mm});
            skLineSegment(sketch, "E460", {"start": v(-21.09, -5.83) * mm, "end": v(-20.97, -5.72) * mm});
            skLineSegment(sketch, "E461", {"start": v(-20.97, -5.72) * mm, "end": v(-20.85, -5.6) * mm});
            skLineSegment(sketch, "E462", {"start": v(-20.85, -5.6) * mm, "end": v(-20.75, -5.48) * mm});
            skLineSegment(sketch, "E463", {"start": v(-20.75, -5.48) * mm, "end": v(-20.65, -5.36) * mm});
            skLineSegment(sketch, "E464", {"start": v(-20.65, -5.36) * mm, "end": v(-20.56, -5.22) * mm});
            skLineSegment(sketch, "E465", {"start": v(-20.56, -5.22) * mm, "end": v(-20.48, -5.08) * mm});
            skLineSegment(sketch, "E466", {"start": v(-20.48, -5.08) * mm, "end": v(-20.4, -4.93) * mm});
            skLineSegment(sketch, "E467", {"start": v(-20.4, -4.93) * mm, "end": v(-20.34, -4.78) * mm});
            skLineSegment(sketch, "E468", {"start": v(-20.34, -4.78) * mm, "end": v(-20.28, -4.61) * mm});
            skLineSegment(sketch, "E469", {"start": v(-20.28, -4.61) * mm, "end": v(-20.23, -4.44) * mm});
            skLineSegment(sketch, "E470", {"start": v(-20.23, -4.44) * mm, "end": v(-20.19, -4.27) * mm});
            skLineSegment(sketch, "E471", {"start": v(-20.19, -4.27) * mm, "end": v(-20.15, -4.08) * mm});
            skLineSegment(sketch, "E472", {"start": v(-20.15, -4.08) * mm, "end": v(-20.12, -3.9) * mm});
            skLineSegment(sketch, "E473", {"start": v(-20.12, -3.9) * mm, "end": v(-20.1, -3.7) * mm});
            skLineSegment(sketch, "E474", {"start": v(-20.1, -3.7) * mm, "end": v(-20.08, -3.5) * mm});
            skLineSegment(sketch, "E475", {"start": v(-20.08, -3.5) * mm, "end": v(-20.07, -3.28) * mm});
            skLineSegment(sketch, "E476", {"start": v(-20.07, -3.28) * mm, "end": v(-20.07, -3.06) * mm});
            skLineSegment(sketch, "E477", {"start": v(-20.07, -3.06) * mm, "end": v(-20.07, -2.9) * mm});
            skLineSegment(sketch, "E478", {"start": v(-20.07, -2.9) * mm, "end": v(-20.08, -2.73) * mm});
            skLineSegment(sketch, "E479", {"start": v(-20.08, -2.73) * mm, "end": v(-20.1, -2.58) * mm});
            skLineSegment(sketch, "E480", {"start": v(-20.1, -2.58) * mm, "end": v(-20.11, -2.43) * mm});
            skLineSegment(sketch, "E481", {"start": v(-20.11, -2.43) * mm, "end": v(-20.14, -2.28) * mm});
            skLineSegment(sketch, "E482", {"start": v(-20.14, -2.28) * mm, "end": v(-20.17, -2.14) * mm});
            skLineSegment(sketch, "E483", {"start": v(-20.17, -2.14) * mm, "end": v(-20.2, -2) * mm});
            skLineSegment(sketch, "E484", {"start": v(-20.2, -2) * mm, "end": v(-20.25, -1.88) * mm});
            skLineSegment(sketch, "E485", {"start": v(-20.25, -1.88) * mm, "end": v(-20.3, -1.75) * mm});
            skLineSegment(sketch, "E486", {"start": v(-20.3, -1.75) * mm, "end": v(-20.36, -1.63) * mm});
            skLineSegment(sketch, "E487", {"start": v(-20.36, -1.63) * mm, "end": v(-20.42, -1.52) * mm});
            skLineSegment(sketch, "E488", {"start": v(-20.42, -1.52) * mm, "end": v(-20.49, -1.4) * mm});
            skLineSegment(sketch, "E489", {"start": v(-20.49, -1.4) * mm, "end": v(-20.56, -1.3) * mm});
            skLineSegment(sketch, "E490", {"start": v(-20.56, -1.3) * mm, "end": v(-20.64, -1.2) * mm});
            skLineSegment(sketch, "E491", {"start": v(-20.64, -1.2) * mm, "end": v(-20.72, -1.1) * mm});
            skLineSegment(sketch, "E492", {"start": v(-20.72, -1.1) * mm, "end": v(-20.81, -1.02) * mm});
            skLineSegment(sketch, "E493", {"start": v(-20.81, -1.02) * mm, "end": v(-20.9, -0.94) * mm});
            skLineSegment(sketch, "E494", {"start": v(-20.9, -0.94) * mm, "end": v(-21.01, -0.86) * mm});
            skLineSegment(sketch, "E495", {"start": v(-21.01, -0.86) * mm, "end": v(-21.12, -0.78) * mm});
            skLineSegment(sketch, "E496", {"start": v(-21.12, -0.78) * mm, "end": v(-21.23, -0.7) * mm});
            skLineSegment(sketch, "E497", {"start": v(-21.23, -0.7) * mm, "end": v(-21.34, -0.64) * mm});
            skLineSegment(sketch, "E498", {"start": v(-21.34, -0.64) * mm, "end": v(-21.47, -0.58) * mm});
            skLineSegment(sketch, "E499", {"start": v(-21.47, -0.58) * mm, "end": v(-21.6, -0.52) * mm});
            skLineSegment(sketch, "E500", {"start": v(-21.6, -0.52) * mm, "end": v(-21.73, -0.47) * mm});
            skLineSegment(sketch, "E501", {"start": v(-21.73, -0.47) * mm, "end": v(-21.86, -0.42) * mm});
            skLineSegment(sketch, "E502", {"start": v(-21.86, -0.42) * mm, "end": v(-22, -0.38) * mm});
            skLineSegment(sketch, "E503", {"start": v(-22, -0.38) * mm, "end": v(-22.16, -0.34) * mm});
            skLineSegment(sketch, "E504", {"start": v(-22.16, -0.34) * mm, "end": v(-22.31, -0.3) * mm});
            skLineSegment(sketch, "E505", {"start": v(-22.31, -0.3) * mm, "end": v(-22.64, -0.25) * mm});
            skLineSegment(sketch, "E506", {"start": v(-22.64, -0.25) * mm, "end": v(-22.99, -0.22) * mm});
            skLineSegment(sketch, "E507", {"start": v(-22.99, -0.22) * mm, "end": v(-24.23, -0.13) * mm});
            skLineSegment(sketch, "E508", {"start": v(-24.23, -0.13) * mm, "end": v(-24.08, 0.76) * mm});
            skLineSegment(sketch, "E509", {"start": v(-24.08, 0.76) * mm, "end": v(-22.5, 0.86) * mm});
            skLineSegment(sketch, "E510", {"start": v(-22.5, 0.86) * mm, "end": v(-22.3, 0.87) * mm});
            skLineSegment(sketch, "E511", {"start": v(-22.3, 0.87) * mm, "end": v(-22.1, 0.9) * mm});
            skLineSegment(sketch, "E512", {"start": v(-22.1, 0.9) * mm, "end": v(-21.92, 0.93) * mm});
            skLineSegment(sketch, "E513", {"start": v(-21.92, 0.93) * mm, "end": v(-21.74, 0.96) * mm});
            skLineSegment(sketch, "E514", {"start": v(-21.74, 0.96) * mm, "end": v(-21.56, 1) * mm});
            skLineSegment(sketch, "E515", {"start": v(-21.56, 1) * mm, "end": v(-21.4, 1.05) * mm});
            skLineSegment(sketch, "E516", {"start": v(-21.4, 1.05) * mm, "end": v(-21.24, 1.1) * mm});
            skLineSegment(sketch, "E517", {"start": v(-21.24, 1.1) * mm, "end": v(-21.1, 1.16) * mm});
            skLineSegment(sketch, "E518", {"start": v(-21.1, 1.16) * mm, "end": v(-20.96, 1.23) * mm});
            skLineSegment(sketch, "E519", {"start": v(-20.96, 1.23) * mm, "end": v(-20.82, 1.3) * mm});
            skLineSegment(sketch, "E520", {"start": v(-20.82, 1.3) * mm, "end": v(-20.7, 1.37) * mm});
            skLineSegment(sketch, "E521", {"start": v(-20.7, 1.37) * mm, "end": v(-20.58, 1.45) * mm});
            skLineSegment(sketch, "E522", {"start": v(-20.58, 1.45) * mm, "end": v(-20.47, 1.54) * mm});
            skLineSegment(sketch, "E523", {"start": v(-20.47, 1.54) * mm, "end": v(-20.36, 1.63) * mm});
            skLineSegment(sketch, "E524", {"start": v(-20.36, 1.63) * mm, "end": v(-20.26, 1.73) * mm});
            skLineSegment(sketch, "E525", {"start": v(-20.26, 1.73) * mm, "end": v(-20.17, 1.83) * mm});
            skLineSegment(sketch, "E526", {"start": v(-20.17, 1.83) * mm, "end": v(-20.09, 1.94) * mm});
            skLineSegment(sketch, "E527", {"start": v(-20.09, 1.94) * mm, "end": v(-20, 2.06) * mm});
            skLineSegment(sketch, "E528", {"start": v(-20, 2.06) * mm, "end": v(-19.93, 2.17) * mm});
            skLineSegment(sketch, "E529", {"start": v(-19.93, 2.17) * mm, "end": v(-19.87, 2.3) * mm});
            skLineSegment(sketch, "E530", {"start": v(-19.87, 2.3) * mm, "end": v(-19.8, 2.42) * mm});
            skLineSegment(sketch, "E531", {"start": v(-19.8, 2.42) * mm, "end": v(-19.75, 2.55) * mm});
            skLineSegment(sketch, "E532", {"start": v(-19.75, 2.55) * mm, "end": v(-19.7, 2.7) * mm});
            skLineSegment(sketch, "E533", {"start": v(-19.7, 2.7) * mm, "end": v(-19.66, 2.83) * mm});
            skLineSegment(sketch, "E534", {"start": v(-19.66, 2.83) * mm, "end": v(-19.6, 3.13) * mm});
            skLineSegment(sketch, "E535", {"start": v(-19.6, 3.13) * mm, "end": v(-19.55, 3.45) * mm});
            skLineSegment(sketch, "E536", {"start": v(-19.55, 3.45) * mm, "end": v(-19.52, 3.78) * mm});
            skLineSegment(sketch, "E537", {"start": v(-19.52, 3.78) * mm, "end": v(-19.51, 4.12) * mm});
            skLineSegment(sketch, "E538", {"start": v(-19.51, 4.12) * mm, "end": v(-19.51, 4.27) * mm});
            skLineSegment(sketch, "E539", {"start": v(-19.51, 4.27) * mm, "end": v(-19.52, 4.41) * mm});
            skLineSegment(sketch, "E540", {"start": v(-19.52, 4.41) * mm, "end": v(-19.53, 4.55) * mm});
            skLineSegment(sketch, "E541", {"start": v(-19.53, 4.55) * mm, "end": v(-19.55, 4.68) * mm});
            skLineSegment(sketch, "E542", {"start": v(-19.55, 4.68) * mm, "end": v(-19.57, 4.81) * mm});
            skLineSegment(sketch, "E543", {"start": v(-19.57, 4.81) * mm, "end": v(-19.6, 4.94) * mm});
            skLineSegment(sketch, "E544", {"start": v(-19.6, 4.94) * mm, "end": v(-19.62, 5.05) * mm});
            skLineSegment(sketch, "E545", {"start": v(-19.62, 5.05) * mm, "end": v(-19.65, 5.17) * mm});
            skLineSegment(sketch, "E546", {"start": v(-19.65, 5.17) * mm, "end": v(-19.7, 5.28) * mm});
            skLineSegment(sketch, "E547", {"start": v(-19.7, 5.28) * mm, "end": v(-19.73, 5.38) * mm});
            skLineSegment(sketch, "E548", {"start": v(-19.73, 5.38) * mm, "end": v(-19.78, 5.48) * mm});
            skLineSegment(sketch, "E549", {"start": v(-19.78, 5.48) * mm, "end": v(-19.83, 5.58) * mm});
            skLineSegment(sketch, "E550", {"start": v(-19.83, 5.58) * mm, "end": v(-19.88, 5.67) * mm});
            skLineSegment(sketch, "E551", {"start": v(-19.88, 5.67) * mm, "end": v(-19.94, 5.76) * mm});
            skLineSegment(sketch, "E552", {"start": v(-19.94, 5.76) * mm, "end": v(-20, 5.84) * mm});
            skLineSegment(sketch, "E553", {"start": v(-20, 5.84) * mm, "end": v(-20.08, 5.92) * mm});
            skLineSegment(sketch, "E554", {"start": v(-20.08, 5.92) * mm, "end": v(-20.15, 5.99) * mm});
            skLineSegment(sketch, "E555", {"start": v(-20.15, 5.99) * mm, "end": v(-20.23, 6.06) * mm});
            skLineSegment(sketch, "E556", {"start": v(-20.23, 6.06) * mm, "end": v(-20.31, 6.12) * mm});
            skLineSegment(sketch, "E557", {"start": v(-20.31, 6.12) * mm, "end": v(-20.4, 6.18) * mm});
            skLineSegment(sketch, "E558", {"start": v(-20.4, 6.18) * mm, "end": v(-20.5, 6.24) * mm});
            skLineSegment(sketch, "E559", {"start": v(-20.5, 6.24) * mm, "end": v(-20.59, 6.29) * mm});
            skLineSegment(sketch, "E560", {"start": v(-20.59, 6.29) * mm, "end": v(-20.7, 6.33) * mm});
            skLineSegment(sketch, "E561", {"start": v(-20.7, 6.33) * mm, "end": v(-20.8, 6.37) * mm});
            skLineSegment(sketch, "E562", {"start": v(-20.8, 6.37) * mm, "end": v(-20.91, 6.4) * mm});
            skLineSegment(sketch, "E563", {"start": v(-20.91, 6.4) * mm, "end": v(-21.03, 6.44) * mm});
            skLineSegment(sketch, "E564", {"start": v(-21.03, 6.44) * mm, "end": v(-21.16, 6.46) * mm});
            skLineSegment(sketch, "E565", {"start": v(-21.16, 6.46) * mm, "end": v(-21.28, 6.49) * mm});
            skLineSegment(sketch, "E566", {"start": v(-21.28, 6.49) * mm, "end": v(-21.42, 6.5) * mm});
            skLineSegment(sketch, "E567", {"start": v(-21.42, 6.5) * mm, "end": v(-21.55, 6.51) * mm});
            skLineSegment(sketch, "E568", {"start": v(-21.55, 6.51) * mm, "end": v(-21.7, 6.52) * mm});
            skLineSegment(sketch, "E569", {"start": v(-21.7, 6.52) * mm, "end": v(-21.85, 6.52) * mm});
            skLineSegment(sketch, "E570", {"start": v(-21.85, 6.52) * mm, "end": v(-22, 6.52) * mm});
            skLineSegment(sketch, "E571", {"start": v(-22, 6.52) * mm, "end": v(-22.33, 6.5) * mm});
            skLineSegment(sketch, "E572", {"start": v(-22.33, 6.5) * mm, "end": v(-22.5, 6.47) * mm});
            skLineSegment(sketch, "E573", {"start": v(-22.5, 6.47) * mm, "end": v(-22.66, 6.44) * mm});
            skLineSegment(sketch, "E574", {"start": v(-22.66, 6.44) * mm, "end": v(-22.97, 6.38) * mm});
            skLineSegment(sketch, "E575", {"start": v(-22.97, 6.38) * mm, "end": v(-23.13, 6.34) * mm});
            skLineSegment(sketch, "E576", {"start": v(-23.13, 6.34) * mm, "end": v(-23.28, 6.3) * mm});
            skLineSegment(sketch, "E577", {"start": v(-23.28, 6.3) * mm, "end": v(-23.56, 6.2) * mm});
            skLineSegment(sketch, "E578", {"start": v(-23.56, 6.2) * mm, "end": v(-23.7, 6.15) * mm});
            skLineSegment(sketch, "E579", {"start": v(-23.7, 6.15) * mm, "end": v(-23.83, 6.1) * mm});
            skLineSegment(sketch, "E580", {"start": v(-23.83, 6.1) * mm, "end": v(-23.96, 6.05) * mm});
            skLineSegment(sketch, "E581", {"start": v(-23.96, 6.05) * mm, "end": v(-24.07, 6) * mm});
            skLineSegment(sketch, "E582", {"start": v(-24.07, 6) * mm, "end": v(-24.18, 5.95) * mm});
            skLineSegment(sketch, "E583", {"start": v(-24.18, 5.95) * mm, "end": v(-24.87, 4.17) * mm});
            skLineSegment(sketch, "E584", {"start": v(-24.87, 4.17) * mm, "end": v(-25.6, 4.17) * mm});
            skLineSegment(sketch, "E585", {"start": v(-25.6, 4.17) * mm, "end": v(-25.1, 6.97) * mm});
            skLineSegment(sketch, "E586", {"start": v(-25.1, 6.97) * mm, "end": v(-24.92, 7.02) * mm});
            skLineSegment(sketch, "E587", {"start": v(-24.92, 7.02) * mm, "end": v(-24.55, 7.1) * mm});
            skLineSegment(sketch, "E588", {"start": v(-24.55, 7.1) * mm, "end": v(-24.37, 7.15) * mm});
            skLineSegment(sketch, "E589", {"start": v(-24.37, 7.15) * mm, "end": v(-24.19, 7.2) * mm});
            skLineSegment(sketch, "E590", {"start": v(-24.19, 7.2) * mm, "end": v(-23.8, 7.27) * mm});
            skLineSegment(sketch, "E591", {"start": v(-23.8, 7.27) * mm, "end": v(-23.61, 7.3) * mm});
            skLineSegment(sketch, "E592", {"start": v(-23.61, 7.3) * mm, "end": v(-23.41, 7.34) * mm});
            skLineSegment(sketch, "E593", {"start": v(-23.41, 7.34) * mm, "end": v(-22.99, 7.38) * mm});
            skLineSegment(sketch, "E594", {"start": v(-22.99, 7.38) * mm, "end": v(-22.77, 7.4) * mm});
            skLineSegment(sketch, "E595", {"start": v(-22.77, 7.4) * mm, "end": v(-22.53, 7.42) * mm});
            skLineSegment(sketch, "E596", {"start": v(-22.53, 7.42) * mm, "end": v(-22.3, 7.43) * mm});
            skLineSegment(sketch, "E597", {"start": v(-22.3, 7.43) * mm, "end": v(-22.04, 7.43) * mm});
            skLineSegment(sketch, "E598", {"start": v(-22.04, 7.43) * mm, "end": v(-21.77, 7.43) * mm});
            skLineSegment(sketch, "E599", {"start": v(-21.77, 7.43) * mm, "end": v(-21.27, 7.42) * mm});
            skLineSegment(sketch, "E600", {"start": v(-21.27, 7.42) * mm, "end": v(-21.03, 7.4) * mm});
            skLineSegment(sketch, "E601", {"start": v(-21.03, 7.4) * mm, "end": v(-20.8, 7.38) * mm});
            skLineSegment(sketch, "E602", {"start": v(-20.8, 7.38) * mm, "end": v(-20.57, 7.35) * mm});
            skLineSegment(sketch, "E603", {"start": v(-20.57, 7.35) * mm, "end": v(-20.36, 7.3) * mm});
            skLineSegment(sketch, "E604", {"start": v(-20.36, 7.3) * mm, "end": v(-20.15, 7.26) * mm});
            skLineSegment(sketch, "E605", {"start": v(-20.15, 7.26) * mm, "end": v(-19.95, 7.2) * mm});
            skLineSegment(sketch, "E606", {"start": v(-19.95, 7.2) * mm, "end": v(-19.75, 7.15) * mm});
            skLineSegment(sketch, "E607", {"start": v(-19.75, 7.15) * mm, "end": v(-19.56, 7.09) * mm});
            skLineSegment(sketch, "E608", {"start": v(-19.56, 7.09) * mm, "end": v(-19.38, 7.02) * mm});
            skLineSegment(sketch, "E609", {"start": v(-19.38, 7.02) * mm, "end": v(-19.2, 6.94) * mm});
            skLineSegment(sketch, "E610", {"start": v(-19.2, 6.94) * mm, "end": v(-19.04, 6.86) * mm});
            skLineSegment(sketch, "E611", {"start": v(-19.04, 6.86) * mm, "end": v(-18.89, 6.77) * mm});
            skLineSegment(sketch, "E612", {"start": v(-18.89, 6.77) * mm, "end": v(-18.74, 6.68) * mm});
            skLineSegment(sketch, "E613", {"start": v(-18.74, 6.68) * mm, "end": v(-18.6, 6.58) * mm});
            skLineSegment(sketch, "E614", {"start": v(-18.6, 6.58) * mm, "end": v(-18.47, 6.47) * mm});
            skLineSegment(sketch, "E615", {"start": v(-18.47, 6.47) * mm, "end": v(-18.35, 6.37) * mm});
            skLineSegment(sketch, "E616", {"start": v(-18.35, 6.37) * mm, "end": v(-18.23, 6.25) * mm});
            skLineSegment(sketch, "E617", {"start": v(-18.23, 6.25) * mm, "end": v(-18.12, 6.13) * mm});
            skLineSegment(sketch, "E618", {"start": v(-18.12, 6.13) * mm, "end": v(-18.02, 6) * mm});
            skLineSegment(sketch, "E619", {"start": v(-18.02, 6) * mm, "end": v(-17.93, 5.87) * mm});
            skLineSegment(sketch, "E620", {"start": v(-17.93, 5.87) * mm, "end": v(-17.85, 5.73) * mm});
            skLineSegment(sketch, "E621", {"start": v(-17.85, 5.73) * mm, "end": v(-17.78, 5.59) * mm});
            skLineSegment(sketch, "E622", {"start": v(-17.78, 5.59) * mm, "end": v(-17.7, 5.44) * mm});
            skLineSegment(sketch, "E623", {"start": v(-17.7, 5.44) * mm, "end": v(-17.65, 5.29) * mm});
            skLineSegment(sketch, "E624", {"start": v(-17.65, 5.29) * mm, "end": v(-17.6, 5.13) * mm});
            skLineSegment(sketch, "E625", {"start": v(-17.6, 5.13) * mm, "end": v(-17.56, 4.97) * mm});
            skLineSegment(sketch, "E626", {"start": v(-17.56, 4.97) * mm, "end": v(-17.53, 4.8) * mm});
            skLineSegment(sketch, "E627", {"start": v(-17.53, 4.8) * mm, "end": v(-17.51, 4.63) * mm});
            skLineSegment(sketch, "E628", {"start": v(-17.51, 4.63) * mm, "end": v(-17.5, 4.46) * mm});
            skLineSegment(sketch, "E629", {"start": v(-17.5, 4.46) * mm, "end": v(-17.5, 4.28) * mm});
            skLineSegment(sketch, "E630", {"start": v(-17.5, 4.28) * mm, "end": v(-17.5, 4.08) * mm});
            skLineSegment(sketch, "E631", {"start": v(-17.5, 4.08) * mm, "end": v(-17.5, 3.88) * mm});
            skLineSegment(sketch, "E632", {"start": v(-17.5, 3.88) * mm, "end": v(-17.53, 3.7) * mm});
            skLineSegment(sketch, "E633", {"start": v(-17.53, 3.7) * mm, "end": v(-17.55, 3.5) * mm});
            skLineSegment(sketch, "E634", {"start": v(-17.55, 3.5) * mm, "end": v(-17.59, 3.32) * mm});
            skLineSegment(sketch, "E635", {"start": v(-17.59, 3.32) * mm, "end": v(-17.63, 3.15) * mm});
            skLineSegment(sketch, "E636", {"start": v(-17.63, 3.15) * mm, "end": v(-17.68, 2.98) * mm});
            skLineSegment(sketch, "E637", {"start": v(-17.68, 2.98) * mm, "end": v(-17.73, 2.8) * mm});
            skLineSegment(sketch, "E638", {"start": v(-17.73, 2.8) * mm, "end": v(-17.8, 2.65) * mm});
            skLineSegment(sketch, "E639", {"start": v(-17.8, 2.65) * mm, "end": v(-17.87, 2.49) * mm});
            skLineSegment(sketch, "E640", {"start": v(-17.87, 2.49) * mm, "end": v(-17.94, 2.33) * mm});
            skLineSegment(sketch, "E641", {"start": v(-17.94, 2.33) * mm, "end": v(-18.03, 2.19) * mm});
            skLineSegment(sketch, "E642", {"start": v(-18.03, 2.19) * mm, "end": v(-18.12, 2.04) * mm});
            skLineSegment(sketch, "E643", {"start": v(-18.12, 2.04) * mm, "end": v(-18.22, 1.9) * mm});
            skLineSegment(sketch, "E644", {"start": v(-18.22, 1.9) * mm, "end": v(-18.33, 1.77) * mm});
            skLineSegment(sketch, "E645", {"start": v(-18.33, 1.77) * mm, "end": v(-18.45, 1.64) * mm});
            skLineSegment(sketch, "E646", {"start": v(-18.45, 1.64) * mm, "end": v(-18.57, 1.51) * mm});
            skLineSegment(sketch, "E647", {"start": v(-18.57, 1.51) * mm, "end": v(-18.7, 1.4) * mm});
            skLineSegment(sketch, "E648", {"start": v(-18.7, 1.4) * mm, "end": v(-18.84, 1.28) * mm});
            skLineSegment(sketch, "E649", {"start": v(-18.84, 1.28) * mm, "end": v(-18.99, 1.18) * mm});
            skLineSegment(sketch, "E650", {"start": v(-18.99, 1.18) * mm, "end": v(-19.14, 1.07) * mm});
            skLineSegment(sketch, "E651", {"start": v(-19.14, 1.07) * mm, "end": v(-19.3, 0.98) * mm});
            skLineSegment(sketch, "E652", {"start": v(-19.3, 0.98) * mm, "end": v(-19.47, 0.89) * mm});
            skLineSegment(sketch, "E653", {"start": v(-19.47, 0.89) * mm, "end": v(-19.65, 0.8) * mm});
            skLineSegment(sketch, "E654", {"start": v(-19.65, 0.8) * mm, "end": v(-19.84, 0.72) * mm});
            skLineSegment(sketch, "E655", {"start": v(-19.84, 0.72) * mm, "end": v(-20.04, 0.65) * mm});
            skLineSegment(sketch, "E656", {"start": v(-20.04, 0.65) * mm, "end": v(-20.24, 0.58) * mm});
            skLineSegment(sketch, "E657", {"start": v(-20.24, 0.58) * mm, "end": v(-20.45, 0.52) * mm});
            skLineSegment(sketch, "E658", {"start": v(-20.45, 0.52) * mm, "end": v(-20.9, 0.42) * mm});
            skLineSegment(sketch, "E659", {"start": v(-20.9, 0.42) * mm, "end": v(-21.38, 0.34) * mm});
            skLineSegment(sketch, "E660", {"start": v(-21.38, 0.34) * mm, "end": v(-21.01, 0.27) * mm});
            skLineSegment(sketch, "E661", {"start": v(-21.01, 0.27) * mm, "end": v(-20.67, 0.2) * mm});
            skLineSegment(sketch, "E662", {"start": v(-20.67, 0.2) * mm, "end": v(-20.34, 0.09) * mm});
            skLineSegment(sketch, "E663", {"start": v(-20.34, 0.09) * mm, "end": v(-20.02, -0.03) * mm});
            skLineSegment(sketch, "E664", {"start": v(-20.02, -0.03) * mm, "end": v(-19.87, -0.1) * mm});
            skLineSegment(sketch, "E665", {"start": v(-19.87, -0.1) * mm, "end": v(-19.73, -0.17) * mm});
            skLineSegment(sketch, "E666", {"start": v(-19.73, -0.17) * mm, "end": v(-19.6, -0.25) * mm});
            skLineSegment(sketch, "E667", {"start": v(-19.6, -0.25) * mm, "end": v(-19.46, -0.33) * mm});
            skLineSegment(sketch, "E668", {"start": v(-19.46, -0.33) * mm, "end": v(-19.33, -0.42) * mm});
            skLineSegment(sketch, "E669", {"start": v(-19.33, -0.42) * mm, "end": v(-19.21, -0.5) * mm});
            skLineSegment(sketch, "E670", {"start": v(-19.21, -0.5) * mm, "end": v(-19.1, -0.6) * mm});
            skLineSegment(sketch, "E671", {"start": v(-19.1, -0.6) * mm, "end": v(-19, -0.7) * mm});
            skLineSegment(sketch, "E672", {"start": v(-19, -0.7) * mm, "end": v(-18.89, -0.8) * mm});
            skLineSegment(sketch, "E673", {"start": v(-18.89, -0.8) * mm, "end": v(-18.79, -0.92) * mm});
            skLineSegment(sketch, "E674", {"start": v(-18.79, -0.92) * mm, "end": v(-18.7, -1.03) * mm});
            skLineSegment(sketch, "E675", {"start": v(-18.7, -1.03) * mm, "end": v(-18.6, -1.14) * mm});
            skLineSegment(sketch, "E676", {"start": v(-18.6, -1.14) * mm, "end": v(-18.53, -1.26) * mm});
            skLineSegment(sketch, "E677", {"start": v(-18.53, -1.26) * mm, "end": v(-18.46, -1.39) * mm});
            skLineSegment(sketch, "E678", {"start": v(-18.46, -1.39) * mm, "end": v(-18.39, -1.52) * mm});
            skLineSegment(sketch, "E679", {"start": v(-18.39, -1.52) * mm, "end": v(-18.33, -1.65) * mm});
            skLineSegment(sketch, "E680", {"start": v(-18.33, -1.65) * mm, "end": v(-18.28, -1.79) * mm});
            skLineSegment(sketch, "E681", {"start": v(-18.28, -1.79) * mm, "end": v(-18.23, -1.93) * mm});
            skLineSegment(sketch, "E682", {"start": v(-18.23, -1.93) * mm, "end": v(-18.2, -2.07) * mm});
            skLineSegment(sketch, "E683", {"start": v(-18.2, -2.07) * mm, "end": v(-18.16, -2.22) * mm});
            skLineSegment(sketch, "E684", {"start": v(-18.16, -2.22) * mm, "end": v(-18.13, -2.37) * mm});
            skLineSegment(sketch, "E685", {"start": v(-18.13, -2.37) * mm, "end": v(-18.12, -2.53) * mm});
            skLineSegment(sketch, "E686", {"start": v(-18.12, -2.53) * mm, "end": v(-18.1, -2.7) * mm});
            skLineSegment(sketch, "E687", {"start": v(-18.1, -2.7) * mm, "end": v(-18.1, -2.85) * mm});
            skLineSegment(sketch, "E688", {"start": v(-18.1, -2.85) * mm, "end": v(-18.1, -3.14) * mm});
            skLineSegment(sketch, "E689", {"start": v(-18.1, -3.14) * mm, "end": v(-18.13, -3.41) * mm});
            skLineSegment(sketch, "E690", {"start": v(-18.13, -3.41) * mm, "end": v(-18.17, -3.68) * mm});
            skLineSegment(sketch, "E691", {"start": v(-18.17, -3.68) * mm, "end": v(-18.22, -3.93) * mm});
            skLineSegment(sketch, "E692", {"start": v(-18.22, -3.93) * mm, "end": v(-18.28, -4.18) * mm});
            skLineSegment(sketch, "E693", {"start": v(-18.28, -4.18) * mm, "end": v(-18.36, -4.42) * mm});
            skLineSegment(sketch, "E694", {"start": v(-18.36, -4.42) * mm, "end": v(-18.45, -4.65) * mm});
            skLineSegment(sketch, "E695", {"start": v(-18.45, -4.65) * mm, "end": v(-18.56, -4.87) * mm});
            skLineSegment(sketch, "E696", {"start": v(-18.56, -4.87) * mm, "end": v(-18.67, -5.09) * mm});
            skLineSegment(sketch, "E697", {"start": v(-18.67, -5.09) * mm, "end": v(-18.8, -5.29) * mm});
            skLineSegment(sketch, "E698", {"start": v(-18.8, -5.29) * mm, "end": v(-18.94, -5.48) * mm});
            skLineSegment(sketch, "E699", {"start": v(-18.94, -5.48) * mm, "end": v(-19.09, -5.67) * mm});
            skLineSegment(sketch, "E700", {"start": v(-19.09, -5.67) * mm, "end": v(-19.25, -5.85) * mm});
            skLineSegment(sketch, "E701", {"start": v(-19.25, -5.85) * mm, "end": v(-19.42, -6.02) * mm});
            skLineSegment(sketch, "E702", {"start": v(-19.42, -6.02) * mm, "end": v(-19.6, -6.18) * mm});
            skLineSegment(sketch, "E703", {"start": v(-19.6, -6.18) * mm, "end": v(-19.8, -6.33) * mm});
            skLineSegment(sketch, "E704", {"start": v(-19.8, -6.33) * mm, "end": v(-20, -6.47) * mm});
            skLineSegment(sketch, "E705", {"start": v(-20, -6.47) * mm, "end": v(-20.2, -6.6) * mm});
            skLineSegment(sketch, "E706", {"start": v(-20.2, -6.6) * mm, "end": v(-20.43, -6.73) * mm});
            skLineSegment(sketch, "E707", {"start": v(-20.43, -6.73) * mm, "end": v(-20.66, -6.84) * mm});
            skLineSegment(sketch, "E708", {"start": v(-20.66, -6.84) * mm, "end": v(-20.9, -6.95) * mm});
            skLineSegment(sketch, "E709", {"start": v(-20.9, -6.95) * mm, "end": v(-21.14, -7.04) * mm});
            skLineSegment(sketch, "E710", {"start": v(-21.14, -7.04) * mm, "end": v(-21.4, -7.13) * mm});
            skLineSegment(sketch, "E711", {"start": v(-21.4, -7.13) * mm, "end": v(-21.66, -7.2) * mm});
            skLineSegment(sketch, "E712", {"start": v(-21.66, -7.2) * mm, "end": v(-22.2, -7.34) * mm});
            skLineSegment(sketch, "E713", {"start": v(-22.2, -7.34) * mm, "end": v(-22.77, -7.43) * mm});
            skLineSegment(sketch, "E714", {"start": v(-22.77, -7.43) * mm, "end": v(-23.35, -7.48) * mm});
            skLineSegment(sketch, "E715", {"start": v(-23.35, -7.48) * mm, "end": v(-23.96, -7.5) * mm});
            skLineSegment(sketch, "E716", {"start": v(-6.28, -3.94) * mm, "end": v(-6.88, -7.28) * mm});
            skLineSegment(sketch, "E717", {"start": v(-6.88, -7.28) * mm, "end": v(-8.64, -7.28) * mm});
            skLineSegment(sketch, "E718", {"start": v(-8.64, -7.28) * mm, "end": v(-8.04, -3.94) * mm});
            skLineSegment(sketch, "E719", {"start": v(-8.04, -3.94) * mm, "end": v(-14.4, -3.94) * mm});
            skLineSegment(sketch, "E720", {"start": v(-14.4, -3.94) * mm, "end": v(-14.2, -2.64) * mm});
            skLineSegment(sketch, "E721", {"start": v(-14.2, -2.64) * mm, "end": v(-6.04, 7.35) * mm});
            skLineSegment(sketch, "E722", {"start": v(-6.04, 7.35) * mm, "end": v(-4.3, 7.35) * mm});
            skLineSegment(sketch, "E723", {"start": v(-4.3, 7.35) * mm, "end": v(-6.04, -2.53) * mm});
            skLineSegment(sketch, "E724", {"start": v(-6.04, -2.53) * mm, "end": v(-3.85, -2.53) * mm});
            skLineSegment(sketch, "E725", {"start": v(-3.85, -2.53) * mm, "end": v(-4.09, -3.94) * mm});
            skLineSegment(sketch, "E726", {"start": v(-4.09, -3.94) * mm, "end": v(-6.28, -3.94) * mm});
            skLineSegment(sketch, "E727", {"start": v(-6.77, 3.34) * mm, "end": v(-6.74, 3.49) * mm});
            skLineSegment(sketch, "E728", {"start": v(-6.74, 3.49) * mm, "end": v(-6.7, 3.65) * mm});
            skLineSegment(sketch, "E729", {"start": v(-6.7, 3.65) * mm, "end": v(-6.67, 3.82) * mm});
            skLineSegment(sketch, "E730", {"start": v(-6.67, 3.82) * mm, "end": v(-6.64, 4) * mm});
            skLineSegment(sketch, "E731", {"start": v(-6.64, 4) * mm, "end": v(-6.6, 4.18) * mm});
            skLineSegment(sketch, "E732", {"start": v(-6.6, 4.18) * mm, "end": v(-6.52, 4.54) * mm});
            skLineSegment(sketch, "E733", {"start": v(-6.52, 4.54) * mm, "end": v(-6.49, 4.71) * mm});
            skLineSegment(sketch, "E734", {"start": v(-6.49, 4.71) * mm, "end": v(-6.44, 4.91) * mm});
            skLineSegment(sketch, "E735", {"start": v(-6.44, 4.91) * mm, "end": v(-6.35, 5.32) * mm});
            skLineSegment(sketch, "E736", {"start": v(-6.35, 5.32) * mm, "end": v(-6.3, 5.52) * mm});
            skLineSegment(sketch, "E737", {"start": v(-6.3, 5.52) * mm, "end": v(-12.85, -2.53) * mm});
            skLineSegment(sketch, "E738", {"start": v(-12.85, -2.53) * mm, "end": v(-7.8, -2.53) * mm});
            skLineSegment(sketch, "E739", {"start": v(-7.8, -2.53) * mm, "end": v(-6.77, 3.34) * mm});
            skLineSegment(sketch, "E740", {"start": v(4.5, 1.23) * mm, "end": v(4.78, 1.22) * mm});
            skLineSegment(sketch, "E741", {"start": v(4.78, 1.22) * mm, "end": v(5.06, 1.21) * mm});
            skLineSegment(sketch, "E742", {"start": v(5.06, 1.21) * mm, "end": v(5.32, 1.2) * mm});
            skLineSegment(sketch, "E743", {"start": v(5.32, 1.2) * mm, "end": v(5.57, 1.16) * mm});
            skLineSegment(sketch, "E744", {"start": v(5.57, 1.16) * mm, "end": v(5.82, 1.13) * mm});
            skLineSegment(sketch, "E745", {"start": v(5.82, 1.13) * mm, "end": v(6.05, 1.09) * mm});
            skLineSegment(sketch, "E746", {"start": v(6.05, 1.09) * mm, "end": v(6.28, 1.04) * mm});
            skLineSegment(sketch, "E747", {"start": v(6.28, 1.04) * mm, "end": v(6.5, 0.98) * mm});
            skLineSegment(sketch, "E748", {"start": v(6.5, 0.98) * mm, "end": v(6.7, 0.91) * mm});
            skLineSegment(sketch, "E749", {"start": v(6.7, 0.91) * mm, "end": v(6.9, 0.84) * mm});
            skLineSegment(sketch, "E750", {"start": v(6.9, 0.84) * mm, "end": v(7.1, 0.77) * mm});
            skLineSegment(sketch, "E751", {"start": v(7.1, 0.77) * mm, "end": v(7.27, 0.68) * mm});
            skLineSegment(sketch, "E752", {"start": v(7.27, 0.68) * mm, "end": v(7.44, 0.59) * mm});
            skLineSegment(sketch, "E753", {"start": v(7.44, 0.59) * mm, "end": v(7.6, 0.5) * mm});
            skLineSegment(sketch, "E754", {"start": v(7.6, 0.5) * mm, "end": v(7.75, 0.38) * mm});
            skLineSegment(sketch, "E755", {"start": v(7.75, 0.38) * mm, "end": v(7.9, 0.27) * mm});
            skLineSegment(sketch, "E756", {"start": v(7.9, 0.27) * mm, "end": v(8.03, 0.15) * mm});
            skLineSegment(sketch, "E757", {"start": v(8.03, 0.15) * mm, "end": v(8.16, 0.03) * mm});
            skLineSegment(sketch, "E758", {"start": v(8.16, 0.03) * mm, "end": v(8.28, -0.1) * mm});
            skLineSegment(sketch, "E759", {"start": v(8.28, -0.1) * mm, "end": v(8.39, -0.24) * mm});
            skLineSegment(sketch, "E760", {"start": v(8.39, -0.24) * mm, "end": v(8.49, -0.39) * mm});
            skLineSegment(sketch, "E761", {"start": v(8.49, -0.39) * mm, "end": v(8.58, -0.54) * mm});
            skLineSegment(sketch, "E762", {"start": v(8.58, -0.54) * mm, "end": v(8.66, -0.7) * mm});
            skLineSegment(sketch, "E763", {"start": v(8.66, -0.7) * mm, "end": v(8.73, -0.86) * mm});
            skLineSegment(sketch, "E764", {"start": v(8.73, -0.86) * mm, "end": v(8.8, -1.03) * mm});
            skLineSegment(sketch, "E765", {"start": v(8.8, -1.03) * mm, "end": v(8.86, -1.2) * mm});
            skLineSegment(sketch, "E766", {"start": v(8.86, -1.2) * mm, "end": v(8.9, -1.38) * mm});
            skLineSegment(sketch, "E767", {"start": v(8.9, -1.38) * mm, "end": v(8.94, -1.56) * mm});
            skLineSegment(sketch, "E768", {"start": v(8.94, -1.56) * mm, "end": v(8.98, -1.75) * mm});
            skLineSegment(sketch, "E769", {"start": v(8.98, -1.75) * mm, "end": v(9, -1.95) * mm});
            skLineSegment(sketch, "E770", {"start": v(9, -1.95) * mm, "end": v(9.01, -2.15) * mm});
            skLineSegment(sketch, "E771", {"start": v(9.01, -2.15) * mm, "end": v(9.01, -2.36) * mm});
            skLineSegment(sketch, "E772", {"start": v(9.01, -2.36) * mm, "end": v(9, -2.66) * mm});
            skLineSegment(sketch, "E773", {"start": v(9, -2.66) * mm, "end": v(9, -2.95) * mm});
            skLineSegment(sketch, "E774", {"start": v(9, -2.95) * mm, "end": v(8.96, -3.24) * mm});
            skLineSegment(sketch, "E775", {"start": v(8.96, -3.24) * mm, "end": v(8.92, -3.51) * mm});
            skLineSegment(sketch, "E776", {"start": v(8.92, -3.51) * mm, "end": v(8.86, -3.78) * mm});
            skLineSegment(sketch, "E777", {"start": v(8.86, -3.78) * mm, "end": v(8.8, -4.04) * mm});
            skLineSegment(sketch, "E778", {"start": v(8.8, -4.04) * mm, "end": v(8.72, -4.3) * mm});
            skLineSegment(sketch, "E779", {"start": v(8.72, -4.3) * mm, "end": v(8.62, -4.54) * mm});
            skLineSegment(sketch, "E780", {"start": v(8.62, -4.54) * mm, "end": v(8.52, -4.77) * mm});
            skLineSegment(sketch, "E781", {"start": v(8.52, -4.77) * mm, "end": v(8.41, -5) * mm});
            skLineSegment(sketch, "E782", {"start": v(8.41, -5) * mm, "end": v(8.29, -5.21) * mm});
            skLineSegment(sketch, "E783", {"start": v(8.29, -5.21) * mm, "end": v(8.15, -5.42) * mm});
            skLineSegment(sketch, "E784", {"start": v(8.15, -5.42) * mm, "end": v(8, -5.62) * mm});
            skLineSegment(sketch, "E785", {"start": v(8, -5.62) * mm, "end": v(7.84, -5.8) * mm});
            skLineSegment(sketch, "E786", {"start": v(7.84, -5.8) * mm, "end": v(7.67, -5.98) * mm});
            skLineSegment(sketch, "E787", {"start": v(7.67, -5.98) * mm, "end": v(7.48, -6.15) * mm});
            skLineSegment(sketch, "E788", {"start": v(7.48, -6.15) * mm, "end": v(7.3, -6.31) * mm});
            skLineSegment(sketch, "E789", {"start": v(7.3, -6.31) * mm, "end": v(7.09, -6.47) * mm});
            skLineSegment(sketch, "E790", {"start": v(7.09, -6.47) * mm, "end": v(6.87, -6.6) * mm});
            skLineSegment(sketch, "E791", {"start": v(6.87, -6.6) * mm, "end": v(6.64, -6.74) * mm});
            skLineSegment(sketch, "E792", {"start": v(6.64, -6.74) * mm, "end": v(6.4, -6.86) * mm});
            skLineSegment(sketch, "E793", {"start": v(6.4, -6.86) * mm, "end": v(6.15, -6.97) * mm});
            skLineSegment(sketch, "E794", {"start": v(6.15, -6.97) * mm, "end": v(5.9, -7.07) * mm});
            skLineSegment(sketch, "E795", {"start": v(5.9, -7.07) * mm, "end": v(5.62, -7.16) * mm});
            skLineSegment(sketch, "E796", {"start": v(5.62, -7.16) * mm, "end": v(5.34, -7.24) * mm});
            skLineSegment(sketch, "E797", {"start": v(5.34, -7.24) * mm, "end": v(5.04, -7.31) * mm});
            skLineSegment(sketch, "E798", {"start": v(5.04, -7.31) * mm, "end": v(4.74, -7.37) * mm});
            skLineSegment(sketch, "E799", {"start": v(4.74, -7.37) * mm, "end": v(4.42, -7.42) * mm});
            skLineSegment(sketch, "E800", {"start": v(4.42, -7.42) * mm, "end": v(4.1, -7.45) * mm});
            skLineSegment(sketch, "E801", {"start": v(4.1, -7.45) * mm, "end": v(3.76, -7.48) * mm});
            skLineSegment(sketch, "E802", {"start": v(3.76, -7.48) * mm, "end": v(3.05, -7.5) * mm});
            skLineSegment(sketch, "E803", {"start": v(3.05, -7.5) * mm, "end": v(2.52, -7.5) * mm});
            skLineSegment(sketch, "E804", {"start": v(2.52, -7.5) * mm, "end": v(2.02, -7.46) * mm});
            skLineSegment(sketch, "E805", {"start": v(2.02, -7.46) * mm, "end": v(1.54, -7.42) * mm});
            skLineSegment(sketch, "E806", {"start": v(1.54, -7.42) * mm, "end": v(1.1, -7.36) * mm});
            skLineSegment(sketch, "E807", {"start": v(1.1, -7.36) * mm, "end": v(0.66, -7.29) * mm});
            skLineSegment(sketch, "E808", {"start": v(0.66, -7.29) * mm, "end": v(0.26, -7.21) * mm});
            skLineSegment(sketch, "E809", {"start": v(0.26, -7.21) * mm, "end": v(-0.12, -7.13) * mm});
            skLineSegment(sketch, "E810", {"start": v(-0.12, -7.13) * mm, "end": v(-0.47, -7.03) * mm});
            skLineSegment(sketch, "E811", {"start": v(-0.47, -7.03) * mm, "end": v(-0.06, -3.97) * mm});
            skLineSegment(sketch, "E812", {"start": v(-0.06, -3.97) * mm, "end": v(0.66, -3.97) * mm});
            skLineSegment(sketch, "E813", {"start": v(0.66, -3.97) * mm, "end": v(0.79, -6.01) * mm});
            skLineSegment(sketch, "E814", {"start": v(0.79, -6.01) * mm, "end": v(0.83, -6.04) * mm});
            skLineSegment(sketch, "E815", {"start": v(0.83, -6.04) * mm, "end": v(0.88, -6.07) * mm});
            skLineSegment(sketch, "E816", {"start": v(0.88, -6.07) * mm, "end": v(0.93, -6.1) * mm});
            skLineSegment(sketch, "E817", {"start": v(0.93, -6.1) * mm, "end": v(0.99, -6.12) * mm});
            skLineSegment(sketch, "E818", {"start": v(0.99, -6.12) * mm, "end": v(1.04, -6.15) * mm});
            skLineSegment(sketch, "E819", {"start": v(1.04, -6.15) * mm, "end": v(1.1, -6.18) * mm});
            skLineSegment(sketch, "E820", {"start": v(1.1, -6.18) * mm, "end": v(1.23, -6.23) * mm});
            skLineSegment(sketch, "E821", {"start": v(1.23, -6.23) * mm, "end": v(1.38, -6.28) * mm});
            skLineSegment(sketch, "E822", {"start": v(1.38, -6.28) * mm, "end": v(1.68, -6.38) * mm});
            skLineSegment(sketch, "E823", {"start": v(1.68, -6.38) * mm, "end": v(1.84, -6.43) * mm});
            skLineSegment(sketch, "E824", {"start": v(1.84, -6.43) * mm, "end": v(2, -6.46) * mm});
            skLineSegment(sketch, "E825", {"start": v(2, -6.46) * mm, "end": v(2.34, -6.53) * mm});
            skLineSegment(sketch, "E826", {"start": v(2.34, -6.53) * mm, "end": v(2.51, -6.56) * mm});
            skLineSegment(sketch, "E827", {"start": v(2.51, -6.56) * mm, "end": v(2.7, -6.57) * mm});
            skLineSegment(sketch, "E828", {"start": v(2.7, -6.57) * mm, "end": v(3.03, -6.6) * mm});
            skLineSegment(sketch, "E829", {"start": v(3.03, -6.6) * mm, "end": v(3.2, -6.6) * mm});
            skLineSegment(sketch, "E830", {"start": v(3.2, -6.6) * mm, "end": v(3.46, -6.6) * mm});
            skLineSegment(sketch, "E831", {"start": v(3.46, -6.6) * mm, "end": v(3.71, -6.58) * mm});
            skLineSegment(sketch, "E832", {"start": v(3.71, -6.58) * mm, "end": v(3.95, -6.56) * mm});
            skLineSegment(sketch, "E833", {"start": v(3.95, -6.56) * mm, "end": v(4.18, -6.52) * mm});
            skLineSegment(sketch, "E834", {"start": v(4.18, -6.52) * mm, "end": v(4.4, -6.48) * mm});
            skLineSegment(sketch, "E835", {"start": v(4.4, -6.48) * mm, "end": v(4.61, -6.43) * mm});
            skLineSegment(sketch, "E836", {"start": v(4.61, -6.43) * mm, "end": v(4.81, -6.37) * mm});
            skLineSegment(sketch, "E837", {"start": v(4.81, -6.37) * mm, "end": v(5, -6.3) * mm});
            skLineSegment(sketch, "E838", {"start": v(5, -6.3) * mm, "end": v(5.18, -6.22) * mm});
            skLineSegment(sketch, "E839", {"start": v(5.18, -6.22) * mm, "end": v(5.35, -6.13) * mm});
            skLineSegment(sketch, "E840", {"start": v(5.35, -6.13) * mm, "end": v(5.51, -6.03) * mm});
            skLineSegment(sketch, "E841", {"start": v(5.51, -6.03) * mm, "end": v(5.66, -5.93) * mm});
            skLineSegment(sketch, "E842", {"start": v(5.66, -5.93) * mm, "end": v(5.8, -5.82) * mm});
            skLineSegment(sketch, "E843", {"start": v(5.8, -5.82) * mm, "end": v(5.94, -5.7) * mm});
            skLineSegment(sketch, "E844", {"start": v(5.94, -5.7) * mm, "end": v(6.07, -5.58) * mm});
            skLineSegment(sketch, "E845", {"start": v(6.07, -5.58) * mm, "end": v(6.18, -5.45) * mm});
            skLineSegment(sketch, "E846", {"start": v(6.18, -5.45) * mm, "end": v(6.3, -5.3) * mm});
            skLineSegment(sketch, "E847", {"start": v(6.3, -5.3) * mm, "end": v(6.4, -5.16) * mm});
            skLineSegment(sketch, "E848", {"start": v(6.4, -5.16) * mm, "end": v(6.49, -5.01) * mm});
            skLineSegment(sketch, "E849", {"start": v(6.49, -5.01) * mm, "end": v(6.57, -4.85) * mm});
            skLineSegment(sketch, "E850", {"start": v(6.57, -4.85) * mm, "end": v(6.65, -4.69) * mm});
            skLineSegment(sketch, "E851", {"start": v(6.65, -4.69) * mm, "end": v(6.72, -4.51) * mm});
            skLineSegment(sketch, "E852", {"start": v(6.72, -4.51) * mm, "end": v(6.78, -4.33) * mm});
            skLineSegment(sketch, "E853", {"start": v(6.78, -4.33) * mm, "end": v(6.83, -4.15) * mm});
            skLineSegment(sketch, "E854", {"start": v(6.83, -4.15) * mm, "end": v(6.92, -3.75) * mm});
            skLineSegment(sketch, "E855", {"start": v(6.92, -3.75) * mm, "end": v(6.98, -3.34) * mm});
            skLineSegment(sketch, "E856", {"start": v(6.98, -3.34) * mm, "end": v(7.02, -2.9) * mm});
            skLineSegment(sketch, "E857", {"start": v(7.02, -2.9) * mm, "end": v(7.03, -2.45) * mm});
            skLineSegment(sketch, "E858", {"start": v(7.03, -2.45) * mm, "end": v(7.02, -2.17) * mm});
            skLineSegment(sketch, "E859", {"start": v(7.02, -2.17) * mm, "end": v(7, -1.9) * mm});
            skLineSegment(sketch, "E860", {"start": v(7, -1.9) * mm, "end": v(6.96, -1.64) * mm});
            skLineSegment(sketch, "E861", {"start": v(6.96, -1.64) * mm, "end": v(6.9, -1.39) * mm});
            skLineSegment(sketch, "E862", {"start": v(6.9, -1.39) * mm, "end": v(6.86, -1.26) * mm});
            skLineSegment(sketch, "E863", {"start": v(6.86, -1.26) * mm, "end": v(6.82, -1.14) * mm});
            skLineSegment(sketch, "E864", {"start": v(6.82, -1.14) * mm, "end": v(6.77, -1.02) * mm});
            skLineSegment(sketch, "E865", {"start": v(6.77, -1.02) * mm, "end": v(6.72, -0.91) * mm});
            skLineSegment(sketch, "E866", {"start": v(6.72, -0.91) * mm, "end": v(6.66, -0.8) * mm});
            skLineSegment(sketch, "E867", {"start": v(6.66, -0.8) * mm, "end": v(6.6, -0.7) * mm});
            skLineSegment(sketch, "E868", {"start": v(6.6, -0.7) * mm, "end": v(6.52, -0.6) * mm});
            skLineSegment(sketch, "E869", {"start": v(6.52, -0.6) * mm, "end": v(6.44, -0.5) * mm});
            skLineSegment(sketch, "E870", {"start": v(6.44, -0.5) * mm, "end": v(6.36, -0.4) * mm});
            skLineSegment(sketch, "E871", {"start": v(6.36, -0.4) * mm, "end": v(6.27, -0.32) * mm});
            skLineSegment(sketch, "E872", {"start": v(6.27, -0.32) * mm, "end": v(6.17, -0.24) * mm});
            skLineSegment(sketch, "E873", {"start": v(6.17, -0.24) * mm, "end": v(6.06, -0.16) * mm});
            skLineSegment(sketch, "E874", {"start": v(6.06, -0.16) * mm, "end": v(5.95, -0.09) * mm});
            skLineSegment(sketch, "E875", {"start": v(5.95, -0.09) * mm, "end": v(5.83, -0.02) * mm});
            skLineSegment(sketch, "E876", {"start": v(5.83, -0.02) * mm, "end": v(5.7, 0.04) * mm});
            skLineSegment(sketch, "E877", {"start": v(5.7, 0.04) * mm, "end": v(5.57, 0.1) * mm});
            skLineSegment(sketch, "E878", {"start": v(5.57, 0.1) * mm, "end": v(5.43, 0.15) * mm});
            skLineSegment(sketch, "E879", {"start": v(5.43, 0.15) * mm, "end": v(5.29, 0.2) * mm});
            skLineSegment(sketch, "E880", {"start": v(5.29, 0.2) * mm, "end": v(5.13, 0.23) * mm});
            skLineSegment(sketch, "E881", {"start": v(5.13, 0.23) * mm, "end": v(4.96, 0.26) * mm});
            skLineSegment(sketch, "E882", {"start": v(4.96, 0.26) * mm, "end": v(4.79, 0.28) * mm});
            skLineSegment(sketch, "E883", {"start": v(4.79, 0.28) * mm, "end": v(4.6, 0.3) * mm});
            skLineSegment(sketch, "E884", {"start": v(4.6, 0.3) * mm, "end": v(4.4, 0.31) * mm});
            skLineSegment(sketch, "E885", {"start": v(4.4, 0.31) * mm, "end": v(4.2, 0.31) * mm});
            skLineSegment(sketch, "E886", {"start": v(4.2, 0.31) * mm, "end": v(3.89, 0.3) * mm});
            skLineSegment(sketch, "E887", {"start": v(3.89, 0.3) * mm, "end": v(3.26, 0.27) * mm});
            skLineSegment(sketch, "E888", {"start": v(3.26, 0.27) * mm, "end": v(2.96, 0.23) * mm});
            skLineSegment(sketch, "E889", {"start": v(2.96, 0.23) * mm, "end": v(2.81, 0.2) * mm});
            skLineSegment(sketch, "E890", {"start": v(2.81, 0.2) * mm, "end": v(2.68, 0.18) * mm});
            skLineSegment(sketch, "E891", {"start": v(2.68, 0.18) * mm, "end": v(2.55, 0.16) * mm});
            skLineSegment(sketch, "E892", {"start": v(2.55, 0.16) * mm, "end": v(2.43, 0.14) * mm});
            skLineSegment(sketch, "E893", {"start": v(2.43, 0.14) * mm, "end": v(2.31, 0.12) * mm});
            skLineSegment(sketch, "E894", {"start": v(2.31, 0.12) * mm, "end": v(2.2, 0.1) * mm});
            skLineSegment(sketch, "E895", {"start": v(2.2, 0.1) * mm, "end": v(2.11, 0.08) * mm});
            skLineSegment(sketch, "E896", {"start": v(2.11, 0.08) * mm, "end": v(2.07, 0.07) * mm});
            skLineSegment(sketch, "E897", {"start": v(2.07, 0.07) * mm, "end": v(2.03, 0.05) * mm});
            skLineSegment(sketch, "E898", {"start": v(2.03, 0.05) * mm, "end": v(0.98, 0.05) * mm});
            skLineSegment(sketch, "E899", {"start": v(0.98, 0.05) * mm, "end": v(2.25, 7.27) * mm});
            skLineSegment(sketch, "E900", {"start": v(2.25, 7.27) * mm, "end": v(9.63, 7.27) * mm});
            skLineSegment(sketch, "E901", {"start": v(9.63, 7.27) * mm, "end": v(9.34, 5.61) * mm});
            skLineSegment(sketch, "E902", {"start": v(9.34, 5.61) * mm, "end": v(2.94, 5.61) * mm});
            skLineSegment(sketch, "E903", {"start": v(2.94, 5.61) * mm, "end": v(2.12, 0.97) * mm});
            skLineSegment(sketch, "E904", {"start": v(2.12, 0.97) * mm, "end": v(2.23, 0.99) * mm});
            skLineSegment(sketch, "E905", {"start": v(2.23, 0.99) * mm, "end": v(2.44, 1.03) * mm});
            skLineSegment(sketch, "E906", {"start": v(2.44, 1.03) * mm, "end": v(2.55, 1.05) * mm});
            skLineSegment(sketch, "E907", {"start": v(2.55, 1.05) * mm, "end": v(2.66, 1.07) * mm});
            skLineSegment(sketch, "E908", {"start": v(2.66, 1.07) * mm, "end": v(2.78, 1.1) * mm});
            skLineSegment(sketch, "E909", {"start": v(2.78, 1.1) * mm, "end": v(3.05, 1.13) * mm});
            skLineSegment(sketch, "E910", {"start": v(3.05, 1.13) * mm, "end": v(3.2, 1.15) * mm});
            skLineSegment(sketch, "E911", {"start": v(3.2, 1.15) * mm, "end": v(3.34, 1.17) * mm});
            skLineSegment(sketch, "E912", {"start": v(3.34, 1.17) * mm, "end": v(3.5, 1.18) * mm});
            skLineSegment(sketch, "E913", {"start": v(3.5, 1.18) * mm, "end": v(3.67, 1.2) * mm});
            skLineSegment(sketch, "E914", {"start": v(3.67, 1.2) * mm, "end": v(3.76, 1.2) * mm});
            skLineSegment(sketch, "E915", {"start": v(3.76, 1.2) * mm, "end": v(3.86, 1.2) * mm});
            skLineSegment(sketch, "E916", {"start": v(3.86, 1.2) * mm, "end": v(4.05, 1.22) * mm});
            skLineSegment(sketch, "E917", {"start": v(4.05, 1.22) * mm, "end": v(4.27, 1.22) * mm});
            skLineSegment(sketch, "E918", {"start": v(4.27, 1.22) * mm, "end": v(4.5, 1.23) * mm});
            skLineSegment(sketch, "E919", {"start": v(17.84, -7.5) * mm, "end": v(17.6, -7.5) * mm});
            skLineSegment(sketch, "E920", {"start": v(17.6, -7.5) * mm, "end": v(17.35, -7.48) * mm});
            skLineSegment(sketch, "E921", {"start": v(17.35, -7.48) * mm, "end": v(17.12, -7.45) * mm});
            skLineSegment(sketch, "E922", {"start": v(17.12, -7.45) * mm, "end": v(16.9, -7.42) * mm});
            skLineSegment(sketch, "E923", {"start": v(16.9, -7.42) * mm, "end": v(16.67, -7.37) * mm});
            skLineSegment(sketch, "E924", {"start": v(16.67, -7.37) * mm, "end": v(16.46, -7.31) * mm});
            skLineSegment(sketch, "E925", {"start": v(16.46, -7.31) * mm, "end": v(16.25, -7.24) * mm});
            skLineSegment(sketch, "E926", {"start": v(16.25, -7.24) * mm, "end": v(16.05, -7.16) * mm});
            skLineSegment(sketch, "E927", {"start": v(16.05, -7.16) * mm, "end": v(15.86, -7.07) * mm});
            skLineSegment(sketch, "E928", {"start": v(15.86, -7.07) * mm, "end": v(15.67, -6.98) * mm});
            skLineSegment(sketch, "E929", {"start": v(15.67, -6.98) * mm, "end": v(15.49, -6.87) * mm});
            skLineSegment(sketch, "E930", {"start": v(15.49, -6.87) * mm, "end": v(15.32, -6.75) * mm});
            skLineSegment(sketch, "E931", {"start": v(15.32, -6.75) * mm, "end": v(15.15, -6.62) * mm});
            skLineSegment(sketch, "E932", {"start": v(15.15, -6.62) * mm, "end": v(15, -6.48) * mm});
            skLineSegment(sketch, "E933", {"start": v(15, -6.48) * mm, "end": v(14.85, -6.33) * mm});
            skLineSegment(sketch, "E934", {"start": v(14.85, -6.33) * mm, "end": v(14.7, -6.18) * mm});
            skLineSegment(sketch, "E935", {"start": v(14.7, -6.18) * mm, "end": v(14.57, -6) * mm});
            skLineSegment(sketch, "E936", {"start": v(14.57, -6) * mm, "end": v(14.44, -5.83) * mm});
            skLineSegment(sketch, "E937", {"start": v(14.44, -5.83) * mm, "end": v(14.33, -5.65) * mm});
            skLineSegment(sketch, "E938", {"start": v(14.33, -5.65) * mm, "end": v(14.22, -5.45) * mm});
            skLineSegment(sketch, "E939", {"start": v(14.22, -5.45) * mm, "end": v(14.11, -5.25) * mm});
            skLineSegment(sketch, "E940", {"start": v(14.11, -5.25) * mm, "end": v(14.02, -5.04) * mm});
            skLineSegment(sketch, "E941", {"start": v(14.02, -5.04) * mm, "end": v(13.93, -4.82) * mm});
            skLineSegment(sketch, "E942", {"start": v(13.93, -4.82) * mm, "end": v(13.86, -4.6) * mm});
            skLineSegment(sketch, "E943", {"start": v(13.86, -4.6) * mm, "end": v(13.79, -4.35) * mm});
            skLineSegment(sketch, "E944", {"start": v(13.79, -4.35) * mm, "end": v(13.73, -4.1) * mm});
            skLineSegment(sketch, "E945", {"start": v(13.73, -4.1) * mm, "end": v(13.68, -3.85) * mm});
            skLineSegment(sketch, "E946", {"start": v(13.68, -3.85) * mm, "end": v(13.64, -3.58) * mm});
            skLineSegment(sketch, "E947", {"start": v(13.64, -3.58) * mm, "end": v(13.6, -3.3) * mm});
            skLineSegment(sketch, "E948", {"start": v(13.6, -3.3) * mm, "end": v(13.57, -2.74) * mm});
            skLineSegment(sketch, "E949", {"start": v(13.57, -2.74) * mm, "end": v(13.56, -2.44) * mm});
            skLineSegment(sketch, "E950", {"start": v(13.56, -2.44) * mm, "end": v(13.58, -1.74) * mm});
            skLineSegment(sketch, "E951", {"start": v(13.58, -1.74) * mm, "end": v(13.62, -1.06) * mm});
            skLineSegment(sketch, "E952", {"start": v(13.62, -1.06) * mm, "end": v(13.7, -0.39) * mm});
            skLineSegment(sketch, "E953", {"start": v(13.7, -0.39) * mm, "end": v(13.8, 0.26) * mm});
            skLineSegment(sketch, "E954", {"start": v(13.8, 0.26) * mm, "end": v(13.94, 0.9) * mm});
            skLineSegment(sketch, "E955", {"start": v(13.94, 0.9) * mm, "end": v(14.1, 1.5) * mm});
            skLineSegment(sketch, "E956", {"start": v(14.1, 1.5) * mm, "end": v(14.28, 2.09) * mm});
            skLineSegment(sketch, "E957", {"start": v(14.28, 2.09) * mm, "end": v(14.49, 2.65) * mm});
            skLineSegment(sketch, "E958", {"start": v(14.49, 2.65) * mm, "end": v(14.72, 3.18) * mm});
            skLineSegment(sketch, "E959", {"start": v(14.72, 3.18) * mm, "end": v(14.98, 3.7) * mm});
            skLineSegment(sketch, "E960", {"start": v(14.98, 3.7) * mm, "end": v(15.26, 4.17) * mm});
            skLineSegment(sketch, "E961", {"start": v(15.26, 4.17) * mm, "end": v(15.56, 4.62) * mm});
            skLineSegment(sketch, "E962", {"start": v(15.56, 4.62) * mm, "end": v(15.89, 5.05) * mm});
            skLineSegment(sketch, "E963", {"start": v(15.89, 5.05) * mm, "end": v(16.23, 5.45) * mm});
            skLineSegment(sketch, "E964", {"start": v(16.23, 5.45) * mm, "end": v(16.59, 5.8) * mm});
            skLineSegment(sketch, "E965", {"start": v(16.59, 5.8) * mm, "end": v(16.96, 6.13) * mm});
            skLineSegment(sketch, "E966", {"start": v(16.96, 6.13) * mm, "end": v(17.36, 6.43) * mm});
            skLineSegment(sketch, "E967", {"start": v(17.36, 6.43) * mm, "end": v(17.76, 6.69) * mm});
            skLineSegment(sketch, "E968", {"start": v(17.76, 6.69) * mm, "end": v(18.2, 6.91) * mm});
            skLineSegment(sketch, "E969", {"start": v(18.2, 6.91) * mm, "end": v(18.63, 7.1) * mm});
            skLineSegment(sketch, "E970", {"start": v(18.63, 7.1) * mm, "end": v(18.86, 7.18) * mm});
            skLineSegment(sketch, "E971", {"start": v(18.86, 7.18) * mm, "end": v(19.09, 7.25) * mm});
            skLineSegment(sketch, "E972", {"start": v(19.09, 7.25) * mm, "end": v(19.32, 7.3) * mm});
            skLineSegment(sketch, "E973", {"start": v(19.32, 7.3) * mm, "end": v(19.55, 7.35) * mm});
            skLineSegment(sketch, "E974", {"start": v(19.55, 7.35) * mm, "end": v(19.79, 7.39) * mm});
            skLineSegment(sketch, "E975", {"start": v(19.79, 7.39) * mm, "end": v(20.03, 7.41) * mm});
            skLineSegment(sketch, "E976", {"start": v(20.03, 7.41) * mm, "end": v(20.27, 7.43) * mm});
            skLineSegment(sketch, "E977", {"start": v(20.27, 7.43) * mm, "end": v(20.51, 7.43) * mm});
            skLineSegment(sketch, "E978", {"start": v(20.51, 7.43) * mm, "end": v(20.95, 7.42) * mm});
            skLineSegment(sketch, "E979", {"start": v(20.95, 7.42) * mm, "end": v(21.37, 7.4) * mm});
            skLineSegment(sketch, "E980", {"start": v(21.37, 7.4) * mm, "end": v(21.79, 7.34) * mm});
            skLineSegment(sketch, "E981", {"start": v(21.79, 7.34) * mm, "end": v(22.2, 7.26) * mm});
            skLineSegment(sketch, "E982", {"start": v(22.2, 7.26) * mm, "end": v(22.6, 7.17) * mm});
            skLineSegment(sketch, "E983", {"start": v(22.6, 7.17) * mm, "end": v(22.97, 7.07) * mm});
            skLineSegment(sketch, "E984", {"start": v(22.97, 7.07) * mm, "end": v(23.33, 6.97) * mm});
            skLineSegment(sketch, "E985", {"start": v(23.33, 6.97) * mm, "end": v(23.67, 6.86) * mm});
            skLineSegment(sketch, "E986", {"start": v(23.67, 6.86) * mm, "end": v(23.22, 4.35) * mm});
            skLineSegment(sketch, "E987", {"start": v(23.22, 4.35) * mm, "end": v(22.5, 4.35) * mm});
            skLineSegment(sketch, "E988", {"start": v(22.5, 4.35) * mm, "end": v(22.39, 5.87) * mm});
            skLineSegment(sketch, "E989", {"start": v(22.39, 5.87) * mm, "end": v(22.17, 6.01) * mm});
            skLineSegment(sketch, "E990", {"start": v(22.17, 6.01) * mm, "end": v(21.94, 6.14) * mm});
            skLineSegment(sketch, "E991", {"start": v(21.94, 6.14) * mm, "end": v(21.7, 6.24) * mm});
            skLineSegment(sketch, "E992", {"start": v(21.7, 6.24) * mm, "end": v(21.45, 6.34) * mm});
            skLineSegment(sketch, "E993", {"start": v(21.45, 6.34) * mm, "end": v(21.33, 6.38) * mm});
            skLineSegment(sketch, "E994", {"start": v(21.33, 6.38) * mm, "end": v(21.2, 6.42) * mm});
            skLineSegment(sketch, "E995", {"start": v(21.2, 6.42) * mm, "end": v(21.08, 6.45) * mm});
            skLineSegment(sketch, "E996", {"start": v(21.08, 6.45) * mm, "end": v(20.95, 6.48) * mm});
            skLineSegment(sketch, "E997", {"start": v(20.95, 6.48) * mm, "end": v(20.82, 6.5) * mm});
            skLineSegment(sketch, "E998", {"start": v(20.82, 6.5) * mm, "end": v(20.7, 6.51) * mm});
            skLineSegment(sketch, "E999", {"start": v(20.7, 6.51) * mm, "end": v(20.56, 6.52) * mm});
            skLineSegment(sketch, "E1000", {"start": v(20.56, 6.52) * mm, "end": v(20.43, 6.52) * mm});
            skLineSegment(sketch, "E1001", {"start": v(20.43, 6.52) * mm, "end": v(20.2, 6.52) * mm});
            skLineSegment(sketch, "E1002", {"start": v(20.2, 6.52) * mm, "end": v(19.98, 6.5) * mm});
            skLineSegment(sketch, "E1003", {"start": v(19.98, 6.5) * mm, "end": v(19.76, 6.45) * mm});
            skLineSegment(sketch, "E1004", {"start": v(19.76, 6.45) * mm, "end": v(19.54, 6.4) * mm});
            skLineSegment(sketch, "E1005", {"start": v(19.54, 6.4) * mm, "end": v(19.33, 6.33) * mm});
            skLineSegment(sketch, "E1006", {"start": v(19.33, 6.33) * mm, "end": v(19.13, 6.25) * mm});
            skLineSegment(sketch, "E1007", {"start": v(19.13, 6.25) * mm, "end": v(18.93, 6.15) * mm});
            skLineSegment(sketch, "E1008", {"start": v(18.93, 6.15) * mm, "end": v(18.73, 6.03) * mm});
            skLineSegment(sketch, "E1009", {"start": v(18.73, 6.03) * mm, "end": v(18.54, 5.9) * mm});
            skLineSegment(sketch, "E1010", {"start": v(18.54, 5.9) * mm, "end": v(18.36, 5.77) * mm});
            skLineSegment(sketch, "E1011", {"start": v(18.36, 5.77) * mm, "end": v(18.19, 5.63) * mm});
            skLineSegment(sketch, "E1012", {"start": v(18.19, 5.63) * mm, "end": v(18.01, 5.47) * mm});
            skLineSegment(sketch, "E1013", {"start": v(18.01, 5.47) * mm, "end": v(17.85, 5.3) * mm});
            skLineSegment(sketch, "E1014", {"start": v(17.85, 5.3) * mm, "end": v(17.69, 5.12) * mm});
            skLineSegment(sketch, "E1015", {"start": v(17.69, 5.12) * mm, "end": v(17.53, 4.92) * mm});
            skLineSegment(sketch, "E1016", {"start": v(17.53, 4.92) * mm, "end": v(17.38, 4.72) * mm});
            skLineSegment(sketch, "E1017", {"start": v(17.38, 4.72) * mm, "end": v(17.1, 4.29) * mm});
            skLineSegment(sketch, "E1018", {"start": v(17.1, 4.29) * mm, "end": v(16.84, 3.82) * mm});
            skLineSegment(sketch, "E1019", {"start": v(16.84, 3.82) * mm, "end": v(16.6, 3.3) * mm});
            skLineSegment(sketch, "E1020", {"start": v(16.6, 3.3) * mm, "end": v(16.39, 2.77) * mm});
            skLineSegment(sketch, "E1021", {"start": v(16.39, 2.77) * mm, "end": v(16.2, 2.2) * mm});
            skLineSegment(sketch, "E1022", {"start": v(16.2, 2.2) * mm, "end": v(16.03, 1.61) * mm});
            skLineSegment(sketch, "E1023", {"start": v(16.03, 1.61) * mm, "end": v(15.88, 1) * mm});
            skLineSegment(sketch, "E1024", {"start": v(15.88, 1) * mm, "end": v(15.76, 0.38) * mm});
            skLineSegment(sketch, "E1025", {"start": v(15.76, 0.38) * mm, "end": v(15.92, 0.47) * mm});
            skLineSegment(sketch, "E1026", {"start": v(15.92, 0.47) * mm, "end": v(16.1, 0.56) * mm});
            skLineSegment(sketch, "E1027", {"start": v(16.1, 0.56) * mm, "end": v(16.27, 0.66) * mm});
            skLineSegment(sketch, "E1028", {"start": v(16.27, 0.66) * mm, "end": v(16.46, 0.75) * mm});
            skLineSegment(sketch, "E1029", {"start": v(16.46, 0.75) * mm, "end": v(16.67, 0.84) * mm});
            skLineSegment(sketch, "E1030", {"start": v(16.67, 0.84) * mm, "end": v(17.09, 1) * mm});
            skLineSegment(sketch, "E1031", {"start": v(17.09, 1) * mm, "end": v(17.3, 1.09) * mm});
            skLineSegment(sketch, "E1032", {"start": v(17.3, 1.09) * mm, "end": v(17.54, 1.16) * mm});
            skLineSegment(sketch, "E1033", {"start": v(17.54, 1.16) * mm, "end": v(18, 1.28) * mm});
            skLineSegment(sketch, "E1034", {"start": v(18, 1.28) * mm, "end": v(18.24, 1.34) * mm});
            skLineSegment(sketch, "E1035", {"start": v(18.24, 1.34) * mm, "end": v(18.49, 1.38) * mm});
            skLineSegment(sketch, "E1036", {"start": v(18.49, 1.38) * mm, "end": v(18.73, 1.4) * mm});
            skLineSegment(sketch, "E1037", {"start": v(18.73, 1.4) * mm, "end": v(18.97, 1.43) * mm});
            skLineSegment(sketch, "E1038", {"start": v(18.97, 1.43) * mm, "end": v(19.22, 1.43) * mm});
            skLineSegment(sketch, "E1039", {"start": v(19.22, 1.43) * mm, "end": v(19.65, 1.42) * mm});
            skLineSegment(sketch, "E1040", {"start": v(19.65, 1.42) * mm, "end": v(19.86, 1.4) * mm});
            skLineSegment(sketch, "E1041", {"start": v(19.86, 1.4) * mm, "end": v(20.06, 1.38) * mm});
            skLineSegment(sketch, "E1042", {"start": v(20.06, 1.38) * mm, "end": v(20.26, 1.34) * mm});
            skLineSegment(sketch, "E1043", {"start": v(20.26, 1.34) * mm, "end": v(20.44, 1.3) * mm});
            skLineSegment(sketch, "E1044", {"start": v(20.44, 1.3) * mm, "end": v(20.63, 1.26) * mm});
            skLineSegment(sketch, "E1045", {"start": v(20.63, 1.26) * mm, "end": v(20.8, 1.2) * mm});
            skLineSegment(sketch, "E1046", {"start": v(20.8, 1.2) * mm, "end": v(20.97, 1.14) * mm});
            skLineSegment(sketch, "E1047", {"start": v(20.97, 1.14) * mm, "end": v(21.14, 1.08) * mm});
            skLineSegment(sketch, "E1048", {"start": v(21.14, 1.08) * mm, "end": v(21.3, 1) * mm});
            skLineSegment(sketch, "E1049", {"start": v(21.3, 1) * mm, "end": v(21.44, 0.93) * mm});
            skLineSegment(sketch, "E1050", {"start": v(21.44, 0.93) * mm, "end": v(21.59, 0.84) * mm});
            skLineSegment(sketch, "E1051", {"start": v(21.59, 0.84) * mm, "end": v(21.72, 0.75) * mm});
            skLineSegment(sketch, "E1052", {"start": v(21.72, 0.75) * mm, "end": v(21.85, 0.65) * mm});
            skLineSegment(sketch, "E1053", {"start": v(21.85, 0.65) * mm, "end": v(21.98, 0.54) * mm});
            skLineSegment(sketch, "E1054", {"start": v(21.98, 0.54) * mm, "end": v(22.1, 0.43) * mm});
            skLineSegment(sketch, "E1055", {"start": v(22.1, 0.43) * mm, "end": v(22.2, 0.32) * mm});
            skLineSegment(sketch, "E1056", {"start": v(22.2, 0.32) * mm, "end": v(22.3, 0.2) * mm});
            skLineSegment(sketch, "E1057", {"start": v(22.3, 0.2) * mm, "end": v(22.4, 0.07) * mm});
            skLineSegment(sketch, "E1058", {"start": v(22.4, 0.07) * mm, "end": v(22.48, -0.06) * mm});
            skLineSegment(sketch, "E1059", {"start": v(22.48, -0.06) * mm, "end": v(22.56, -0.2) * mm});
            skLineSegment(sketch, "E1060", {"start": v(22.56, -0.2) * mm, "end": v(22.64, -0.35) * mm});
            skLineSegment(sketch, "E1061", {"start": v(22.64, -0.35) * mm, "end": v(22.7, -0.5) * mm});
            skLineSegment(sketch, "E1062", {"start": v(22.7, -0.5) * mm, "end": v(22.76, -0.65) * mm});
            skLineSegment(sketch, "E1063", {"start": v(22.76, -0.65) * mm, "end": v(22.81, -0.81) * mm});
            skLineSegment(sketch, "E1064", {"start": v(22.81, -0.81) * mm, "end": v(22.86, -0.98) * mm});
            skLineSegment(sketch, "E1065", {"start": v(22.86, -0.98) * mm, "end": v(22.9, -1.15) * mm});
            skLineSegment(sketch, "E1066", {"start": v(22.9, -1.15) * mm, "end": v(22.92, -1.32) * mm});
            skLineSegment(sketch, "E1067", {"start": v(22.92, -1.32) * mm, "end": v(22.94, -1.5) * mm});
            skLineSegment(sketch, "E1068", {"start": v(22.94, -1.5) * mm, "end": v(22.95, -1.68) * mm});
            skLineSegment(sketch, "E1069", {"start": v(22.95, -1.68) * mm, "end": v(22.95, -1.87) * mm});
            skLineSegment(sketch, "E1070", {"start": v(22.95, -1.87) * mm, "end": v(22.93, -2.42) * mm});
            skLineSegment(sketch, "E1071", {"start": v(22.93, -2.42) * mm, "end": v(22.87, -2.97) * mm});
            skLineSegment(sketch, "E1072", {"start": v(22.87, -2.97) * mm, "end": v(22.78, -3.5) * mm});
            skLineSegment(sketch, "E1073", {"start": v(22.78, -3.5) * mm, "end": v(22.64, -4.02) * mm});
            skLineSegment(sketch, "E1074", {"start": v(22.64, -4.02) * mm, "end": v(22.56, -4.27) * mm});
            skLineSegment(sketch, "E1075", {"start": v(22.56, -4.27) * mm, "end": v(22.47, -4.51) * mm});
            skLineSegment(sketch, "E1076", {"start": v(22.47, -4.51) * mm, "end": v(22.36, -4.75) * mm});
            skLineSegment(sketch, "E1077", {"start": v(22.36, -4.75) * mm, "end": v(22.25, -4.97) * mm});
            skLineSegment(sketch, "E1078", {"start": v(22.25, -4.97) * mm, "end": v(22.13, -5.2) * mm});
            skLineSegment(sketch, "E1079", {"start": v(22.13, -5.2) * mm, "end": v(22, -5.4) * mm});
            skLineSegment(sketch, "E1080", {"start": v(22, -5.4) * mm, "end": v(21.85, -5.61) * mm});
            skLineSegment(sketch, "E1081", {"start": v(21.85, -5.61) * mm, "end": v(21.7, -5.8) * mm});
            skLineSegment(sketch, "E1082", {"start": v(21.7, -5.8) * mm, "end": v(21.53, -6) * mm});
            skLineSegment(sketch, "E1083", {"start": v(21.53, -6) * mm, "end": v(21.36, -6.17) * mm});
            skLineSegment(sketch, "E1084", {"start": v(21.36, -6.17) * mm, "end": v(21.17, -6.34) * mm});
            skLineSegment(sketch, "E1085", {"start": v(21.17, -6.34) * mm, "end": v(20.98, -6.5) * mm});
            skLineSegment(sketch, "E1086", {"start": v(20.98, -6.5) * mm, "end": v(20.78, -6.65) * mm});
            skLineSegment(sketch, "E1087", {"start": v(20.78, -6.65) * mm, "end": v(20.56, -6.8) * mm});
            skLineSegment(sketch, "E1088", {"start": v(20.56, -6.8) * mm, "end": v(20.33, -6.92) * mm});
            skLineSegment(sketch, "E1089", {"start": v(20.33, -6.92) * mm, "end": v(20.1, -7.04) * mm});
            skLineSegment(sketch, "E1090", {"start": v(20.1, -7.04) * mm, "end": v(19.85, -7.15) * mm});
            skLineSegment(sketch, "E1091", {"start": v(19.85, -7.15) * mm, "end": v(19.6, -7.24) * mm});
            skLineSegment(sketch, "E1092", {"start": v(19.6, -7.24) * mm, "end": v(19.33, -7.32) * mm});
            skLineSegment(sketch, "E1093", {"start": v(19.33, -7.32) * mm, "end": v(19.06, -7.39) * mm});
            skLineSegment(sketch, "E1094", {"start": v(19.06, -7.39) * mm, "end": v(18.77, -7.44) * mm});
            skLineSegment(sketch, "E1095", {"start": v(18.77, -7.44) * mm, "end": v(18.47, -7.47) * mm});
            skLineSegment(sketch, "E1096", {"start": v(18.47, -7.47) * mm, "end": v(18.16, -7.5) * mm});
            skLineSegment(sketch, "E1097", {"start": v(18.16, -7.5) * mm, "end": v(17.84, -7.5) * mm});
            skLineSegment(sketch, "E1098", {"start": v(15.49, -2.82) * mm, "end": v(15.49, -3.07) * mm});
            skLineSegment(sketch, "E1099", {"start": v(15.49, -3.07) * mm, "end": v(15.5, -3.32) * mm});
            skLineSegment(sketch, "E1100", {"start": v(15.5, -3.32) * mm, "end": v(15.51, -3.55) * mm});
            skLineSegment(sketch, "E1101", {"start": v(15.51, -3.55) * mm, "end": v(15.53, -3.78) * mm});
            skLineSegment(sketch, "E1102", {"start": v(15.53, -3.78) * mm, "end": v(15.56, -4) * mm});
            skLineSegment(sketch, "E1103", {"start": v(15.56, -4) * mm, "end": v(15.59, -4.2) * mm});
            skLineSegment(sketch, "E1104", {"start": v(15.59, -4.2) * mm, "end": v(15.63, -4.4) * mm});
            skLineSegment(sketch, "E1105", {"start": v(15.63, -4.4) * mm, "end": v(15.67, -4.58) * mm});
            skLineSegment(sketch, "E1106", {"start": v(15.67, -4.58) * mm, "end": v(15.72, -4.76) * mm});
            skLineSegment(sketch, "E1107", {"start": v(15.72, -4.76) * mm, "end": v(15.77, -4.93) * mm});
            skLineSegment(sketch, "E1108", {"start": v(15.77, -4.93) * mm, "end": v(15.83, -5.09) * mm});
            skLineSegment(sketch, "E1109", {"start": v(15.83, -5.09) * mm, "end": v(15.89, -5.24) * mm});
            skLineSegment(sketch, "E1110", {"start": v(15.89, -5.24) * mm, "end": v(15.95, -5.38) * mm});
            skLineSegment(sketch, "E1111", {"start": v(15.95, -5.38) * mm, "end": v(16.02, -5.52) * mm});
            skLineSegment(sketch, "E1112", {"start": v(16.02, -5.52) * mm, "end": v(16.1, -5.65) * mm});
            skLineSegment(sketch, "E1113", {"start": v(16.1, -5.65) * mm, "end": v(16.17, -5.76) * mm});
            skLineSegment(sketch, "E1114", {"start": v(16.17, -5.76) * mm, "end": v(16.25, -5.87) * mm});
            skLineSegment(sketch, "E1115", {"start": v(16.25, -5.87) * mm, "end": v(16.33, -5.98) * mm});
            skLineSegment(sketch, "E1116", {"start": v(16.33, -5.98) * mm, "end": v(16.42, -6.07) * mm});
            skLineSegment(sketch, "E1117", {"start": v(16.42, -6.07) * mm, "end": v(16.51, -6.16) * mm});
            skLineSegment(sketch, "E1118", {"start": v(16.51, -6.16) * mm, "end": v(16.6, -6.24) * mm});
            skLineSegment(sketch, "E1119", {"start": v(16.6, -6.24) * mm, "end": v(16.7, -6.31) * mm});
            skLineSegment(sketch, "E1120", {"start": v(16.7, -6.31) * mm, "end": v(16.81, -6.38) * mm});
            skLineSegment(sketch, "E1121", {"start": v(16.81, -6.38) * mm, "end": v(16.92, -6.44) * mm});
            skLineSegment(sketch, "E1122", {"start": v(16.92, -6.44) * mm, "end": v(17.03, -6.48) * mm});
            skLineSegment(sketch, "E1123", {"start": v(17.03, -6.48) * mm, "end": v(17.14, -6.53) * mm});
            skLineSegment(sketch, "E1124", {"start": v(17.14, -6.53) * mm, "end": v(17.25, -6.56) * mm});
            skLineSegment(sketch, "E1125", {"start": v(17.25, -6.56) * mm, "end": v(17.37, -6.6) * mm});
            skLineSegment(sketch, "E1126", {"start": v(17.37, -6.6) * mm, "end": v(17.5, -6.61) * mm});
            skLineSegment(sketch, "E1127", {"start": v(17.5, -6.61) * mm, "end": v(17.61, -6.63) * mm});
            skLineSegment(sketch, "E1128", {"start": v(17.61, -6.63) * mm, "end": v(17.74, -6.64) * mm});
            skLineSegment(sketch, "E1129", {"start": v(17.74, -6.64) * mm, "end": v(17.86, -6.64) * mm});
            skLineSegment(sketch, "E1130", {"start": v(17.86, -6.64) * mm, "end": v(18.06, -6.64) * mm});
            skLineSegment(sketch, "E1131", {"start": v(18.06, -6.64) * mm, "end": v(18.25, -6.62) * mm});
            skLineSegment(sketch, "E1132", {"start": v(18.25, -6.62) * mm, "end": v(18.43, -6.6) * mm});
            skLineSegment(sketch, "E1133", {"start": v(18.43, -6.6) * mm, "end": v(18.6, -6.55) * mm});
            skLineSegment(sketch, "E1134", {"start": v(18.6, -6.55) * mm, "end": v(18.78, -6.5) * mm});
            skLineSegment(sketch, "E1135", {"start": v(18.78, -6.5) * mm, "end": v(18.94, -6.44) * mm});
            skLineSegment(sketch, "E1136", {"start": v(18.94, -6.44) * mm, "end": v(19.1, -6.37) * mm});
            skLineSegment(sketch, "E1137", {"start": v(19.1, -6.37) * mm, "end": v(19.24, -6.28) * mm});
            skLineSegment(sketch, "E1138", {"start": v(19.24, -6.28) * mm, "end": v(19.38, -6.19) * mm});
            skLineSegment(sketch, "E1139", {"start": v(19.38, -6.19) * mm, "end": v(19.52, -6.08) * mm});
            skLineSegment(sketch, "E1140", {"start": v(19.52, -6.08) * mm, "end": v(19.65, -5.97) * mm});
            skLineSegment(sketch, "E1141", {"start": v(19.65, -5.97) * mm, "end": v(19.77, -5.85) * mm});
            skLineSegment(sketch, "E1142", {"start": v(19.77, -5.85) * mm, "end": v(19.89, -5.72) * mm});
            skLineSegment(sketch, "E1143", {"start": v(19.89, -5.72) * mm, "end": v(20, -5.58) * mm});
            skLineSegment(sketch, "E1144", {"start": v(20, -5.58) * mm, "end": v(20.1, -5.44) * mm});
            skLineSegment(sketch, "E1145", {"start": v(20.1, -5.44) * mm, "end": v(20.2, -5.29) * mm});
            skLineSegment(sketch, "E1146", {"start": v(20.2, -5.29) * mm, "end": v(20.29, -5.12) * mm});
            skLineSegment(sketch, "E1147", {"start": v(20.29, -5.12) * mm, "end": v(20.37, -4.95) * mm});
            skLineSegment(sketch, "E1148", {"start": v(20.37, -4.95) * mm, "end": v(20.45, -4.78) * mm});
            skLineSegment(sketch, "E1149", {"start": v(20.45, -4.78) * mm, "end": v(20.52, -4.6) * mm});
            skLineSegment(sketch, "E1150", {"start": v(20.52, -4.6) * mm, "end": v(20.6, -4.4) * mm});
            skLineSegment(sketch, "E1151", {"start": v(20.6, -4.4) * mm, "end": v(20.65, -4.2) * mm});
            skLineSegment(sketch, "E1152", {"start": v(20.65, -4.2) * mm, "end": v(20.75, -3.8) * mm});
            skLineSegment(sketch, "E1153", {"start": v(20.75, -3.8) * mm, "end": v(20.83, -3.37) * mm});
            skLineSegment(sketch, "E1154", {"start": v(20.83, -3.37) * mm, "end": v(20.89, -2.92) * mm});
            skLineSegment(sketch, "E1155", {"start": v(20.89, -2.92) * mm, "end": v(20.92, -2.46) * mm});
            skLineSegment(sketch, "E1156", {"start": v(20.92, -2.46) * mm, "end": v(20.93, -1.98) * mm});
            skLineSegment(sketch, "E1157", {"start": v(20.93, -1.98) * mm, "end": v(20.93, -1.69) * mm});
            skLineSegment(sketch, "E1158", {"start": v(20.93, -1.69) * mm, "end": v(20.92, -1.55) * mm});
            skLineSegment(sketch, "E1159", {"start": v(20.92, -1.55) * mm, "end": v(20.9, -1.42) * mm});
            skLineSegment(sketch, "E1160", {"start": v(20.9, -1.42) * mm, "end": v(20.88, -1.3) * mm});
            skLineSegment(sketch, "E1161", {"start": v(20.88, -1.3) * mm, "end": v(20.86, -1.17) * mm});
            skLineSegment(sketch, "E1162", {"start": v(20.86, -1.17) * mm, "end": v(20.83, -1.05) * mm});
            skLineSegment(sketch, "E1163", {"start": v(20.83, -1.05) * mm, "end": v(20.8, -0.94) * mm});
            skLineSegment(sketch, "E1164", {"start": v(20.8, -0.94) * mm, "end": v(20.77, -0.83) * mm});
            skLineSegment(sketch, "E1165", {"start": v(20.77, -0.83) * mm, "end": v(20.73, -0.73) * mm});
            skLineSegment(sketch, "E1166", {"start": v(20.73, -0.73) * mm, "end": v(20.68, -0.63) * mm});
            skLineSegment(sketch, "E1167", {"start": v(20.68, -0.63) * mm, "end": v(20.63, -0.54) * mm});
            skLineSegment(sketch, "E1168", {"start": v(20.63, -0.54) * mm, "end": v(20.58, -0.45) * mm});
            skLineSegment(sketch, "E1169", {"start": v(20.58, -0.45) * mm, "end": v(20.53, -0.36) * mm});
            skLineSegment(sketch, "E1170", {"start": v(20.53, -0.36) * mm, "end": v(20.47, -0.28) * mm});
            skLineSegment(sketch, "E1171", {"start": v(20.47, -0.28) * mm, "end": v(20.4, -0.2) * mm});
            skLineSegment(sketch, "E1172", {"start": v(20.4, -0.2) * mm, "end": v(20.33, -0.13) * mm});
            skLineSegment(sketch, "E1173", {"start": v(20.33, -0.13) * mm, "end": v(20.26, -0.07) * mm});
            skLineSegment(sketch, "E1174", {"start": v(20.26, -0.07) * mm, "end": v(20.19, 0) * mm});
            skLineSegment(sketch, "E1175", {"start": v(20.19, 0) * mm, "end": v(20.1, 0.06) * mm});
            skLineSegment(sketch, "E1176", {"start": v(20.1, 0.06) * mm, "end": v(20.02, 0.1) * mm});
            skLineSegment(sketch, "E1177", {"start": v(20.02, 0.1) * mm, "end": v(19.93, 0.16) * mm});
            skLineSegment(sketch, "E1178", {"start": v(19.93, 0.16) * mm, "end": v(19.83, 0.2) * mm});
            skLineSegment(sketch, "E1179", {"start": v(19.83, 0.2) * mm, "end": v(19.73, 0.24) * mm});
            skLineSegment(sketch, "E1180", {"start": v(19.73, 0.24) * mm, "end": v(19.63, 0.28) * mm});
            skLineSegment(sketch, "E1181", {"start": v(19.63, 0.28) * mm, "end": v(19.52, 0.3) * mm});
            skLineSegment(sketch, "E1182", {"start": v(19.52, 0.3) * mm, "end": v(19.4, 0.33) * mm});
            skLineSegment(sketch, "E1183", {"start": v(19.4, 0.33) * mm, "end": v(19.28, 0.35) * mm});
            skLineSegment(sketch, "E1184", {"start": v(19.28, 0.35) * mm, "end": v(19.16, 0.37) * mm});
            skLineSegment(sketch, "E1185", {"start": v(19.16, 0.37) * mm, "end": v(19.03, 0.38) * mm});
            skLineSegment(sketch, "E1186", {"start": v(19.03, 0.38) * mm, "end": v(18.9, 0.39) * mm});
            skLineSegment(sketch, "E1187", {"start": v(18.9, 0.39) * mm, "end": v(18.76, 0.4) * mm});
            skLineSegment(sketch, "E1188", {"start": v(18.76, 0.4) * mm, "end": v(18.58, 0.39) * mm});
            skLineSegment(sketch, "E1189", {"start": v(18.58, 0.39) * mm, "end": v(18.2, 0.36) * mm});
            skLineSegment(sketch, "E1190", {"start": v(18.2, 0.36) * mm, "end": v(18.01, 0.34) * mm});
            skLineSegment(sketch, "E1191", {"start": v(18.01, 0.34) * mm, "end": v(17.82, 0.3) * mm});
            skLineSegment(sketch, "E1192", {"start": v(17.82, 0.3) * mm, "end": v(17.42, 0.23) * mm});
            skLineSegment(sketch, "E1193", {"start": v(17.42, 0.23) * mm, "end": v(17.22, 0.18) * mm});
            skLineSegment(sketch, "E1194", {"start": v(17.22, 0.18) * mm, "end": v(17.02, 0.14) * mm});
            skLineSegment(sketch, "E1195", {"start": v(17.02, 0.14) * mm, "end": v(16.62, 0.03) * mm});
            skLineSegment(sketch, "E1196", {"start": v(16.62, 0.03) * mm, "end": v(16.42, -0.03) * mm});
            skLineSegment(sketch, "E1197", {"start": v(16.42, -0.03) * mm, "end": v(16.22, -0.1) * mm});
            skLineSegment(sketch, "E1198", {"start": v(16.22, -0.1) * mm, "end": v(15.84, -0.22) * mm});
            skLineSegment(sketch, "E1199", {"start": v(15.84, -0.22) * mm, "end": v(15.66, -0.28) * mm});
            skLineSegment(sketch, "E1200", {"start": v(15.66, -0.28) * mm, "end": v(15.62, -0.6) * mm});
            skLineSegment(sketch, "E1201", {"start": v(15.62, -0.6) * mm, "end": v(15.55, -1.22) * mm});
            skLineSegment(sketch, "E1202", {"start": v(15.55, -1.22) * mm, "end": v(15.53, -1.54) * mm});
            skLineSegment(sketch, "E1203", {"start": v(15.53, -1.54) * mm, "end": v(15.5, -1.86) * mm});
            skLineSegment(sketch, "E1204", {"start": v(15.5, -1.86) * mm, "end": v(15.49, -2.5) * mm});
            skLineSegment(sketch, "E1205", {"start": v(15.49, -2.5) * mm, "end": v(15.49, -2.82) * mm});
            skLineSegment(sketch, "E1206", {"start": v(29.67, 3.83) * mm, "end": v(28.96, 3.83) * mm});
            skLineSegment(sketch, "E1207", {"start": v(28.96, 3.83) * mm, "end": v(29.56, 7.27) * mm});
            skLineSegment(sketch, "E1208", {"start": v(29.56, 7.27) * mm, "end": v(38.57, 7.27) * mm});
            skLineSegment(sketch, "E1209", {"start": v(38.57, 7.27) * mm, "end": v(38.42, 6.44) * mm});
            skLineSegment(sketch, "E1210", {"start": v(38.42, 6.44) * mm, "end": v(29.51, -7.28) * mm});
            skLineSegment(sketch, "E1211", {"start": v(29.51, -7.28) * mm, "end": v(28, -7.28) * mm});
            skLineSegment(sketch, "E1212", {"start": v(28, -7.28) * mm, "end": v(36.65, 5.61) * mm});
            skLineSegment(sketch, "E1213", {"start": v(36.65, 5.61) * mm, "end": v(30.37, 5.61) * mm});
            skLineSegment(sketch, "E1214", {"start": v(30.37, 5.61) * mm, "end": v(29.67, 3.83) * mm});
            skLineSegment(sketch, "E1215", {"start": v(52.47, 4.57) * mm, "end": v(52.45, 4.15) * mm});
            skLineSegment(sketch, "E1216", {"start": v(52.45, 4.15) * mm, "end": v(52.44, 3.94) * mm});
            skLineSegment(sketch, "E1217", {"start": v(52.44, 3.94) * mm, "end": v(52.41, 3.74) * mm});
            skLineSegment(sketch, "E1218", {"start": v(52.41, 3.74) * mm, "end": v(52.38, 3.55) * mm});
            skLineSegment(sketch, "E1219", {"start": v(52.38, 3.55) * mm, "end": v(52.34, 3.36) * mm});
            skLineSegment(sketch, "E1220", {"start": v(52.34, 3.36) * mm, "end": v(52.3, 3.18) * mm});
            skLineSegment(sketch, "E1221", {"start": v(52.3, 3.18) * mm, "end": v(52.24, 3) * mm});
            skLineSegment(sketch, "E1222", {"start": v(52.24, 3) * mm, "end": v(52.12, 2.67) * mm});
            skLineSegment(sketch, "E1223", {"start": v(52.12, 2.67) * mm, "end": v(51.97, 2.36) * mm});
            skLineSegment(sketch, "E1224", {"start": v(51.97, 2.36) * mm, "end": v(51.8, 2.07) * mm});
            skLineSegment(sketch, "E1225", {"start": v(51.8, 2.07) * mm, "end": v(51.72, 1.93) * mm});
            skLineSegment(sketch, "E1226", {"start": v(51.72, 1.93) * mm, "end": v(51.62, 1.8) * mm});
            skLineSegment(sketch, "E1227", {"start": v(51.62, 1.8) * mm, "end": v(51.42, 1.55) * mm});
            skLineSegment(sketch, "E1228", {"start": v(51.42, 1.55) * mm, "end": v(51.2, 1.32) * mm});
            skLineSegment(sketch, "E1229", {"start": v(51.2, 1.32) * mm, "end": v(51.1, 1.22) * mm});
            skLineSegment(sketch, "E1230", {"start": v(51.1, 1.22) * mm, "end": v(50.98, 1.12) * mm});
            skLineSegment(sketch, "E1231", {"start": v(50.98, 1.12) * mm, "end": v(50.86, 1.02) * mm});
            skLineSegment(sketch, "E1232", {"start": v(50.86, 1.02) * mm, "end": v(50.73, 0.93) * mm});
            skLineSegment(sketch, "E1233", {"start": v(50.73, 0.93) * mm, "end": v(50.48, 0.78) * mm});
            skLineSegment(sketch, "E1234", {"start": v(50.48, 0.78) * mm, "end": v(50.22, 0.64) * mm});
            skLineSegment(sketch, "E1235", {"start": v(50.22, 0.64) * mm, "end": v(49.95, 0.53) * mm});
            skLineSegment(sketch, "E1236", {"start": v(49.95, 0.53) * mm, "end": v(49.67, 0.43) * mm});
            skLineSegment(sketch, "E1237", {"start": v(49.67, 0.43) * mm, "end": v(49.9, 0.35) * mm});
            skLineSegment(sketch, "E1238", {"start": v(49.9, 0.35) * mm, "end": v(50.1, 0.24) * mm});
            skLineSegment(sketch, "E1239", {"start": v(50.1, 0.24) * mm, "end": v(50.31, 0.13) * mm});
            skLineSegment(sketch, "E1240", {"start": v(50.31, 0.13) * mm, "end": v(50.5, 0) * mm});
            skLineSegment(sketch, "E1241", {"start": v(50.5, 0) * mm, "end": v(50.68, -0.14) * mm});
            skLineSegment(sketch, "E1242", {"start": v(50.68, -0.14) * mm, "end": v(50.84, -0.3) * mm});
            skLineSegment(sketch, "E1243", {"start": v(50.84, -0.3) * mm, "end": v(51, -0.47) * mm});
            skLineSegment(sketch, "E1244", {"start": v(51, -0.47) * mm, "end": v(51.13, -0.65) * mm});
            skLineSegment(sketch, "E1245", {"start": v(51.13, -0.65) * mm, "end": v(51.2, -0.75) * mm});
            skLineSegment(sketch, "E1246", {"start": v(51.2, -0.75) * mm, "end": v(51.31, -0.94) * mm});
            skLineSegment(sketch, "E1247", {"start": v(51.31, -0.94) * mm, "end": v(51.41, -1.15) * mm});
            skLineSegment(sketch, "E1248", {"start": v(51.41, -1.15) * mm, "end": v(51.5, -1.38) * mm});
            skLineSegment(sketch, "E1249", {"start": v(51.5, -1.38) * mm, "end": v(51.56, -1.6) * mm});
            skLineSegment(sketch, "E1250", {"start": v(51.56, -1.6) * mm, "end": v(51.61, -1.85) * mm});
            skLineSegment(sketch, "E1251", {"start": v(51.61, -1.85) * mm, "end": v(51.65, -2.1) * mm});
            skLineSegment(sketch, "E1252", {"start": v(51.65, -2.1) * mm, "end": v(51.66, -2.37) * mm});
            skLineSegment(sketch, "E1253", {"start": v(51.66, -2.37) * mm, "end": v(51.66, -2.5) * mm});
            skLineSegment(sketch, "E1254", {"start": v(51.66, -2.5) * mm, "end": v(51.66, -2.8) * mm});
            skLineSegment(sketch, "E1255", {"start": v(51.66, -2.8) * mm, "end": v(51.64, -3.1) * mm});
            skLineSegment(sketch, "E1256", {"start": v(51.64, -3.1) * mm, "end": v(51.62, -3.37) * mm});
            skLineSegment(sketch, "E1257", {"start": v(51.62, -3.37) * mm, "end": v(51.58, -3.64) * mm});
            skLineSegment(sketch, "E1258", {"start": v(51.58, -3.64) * mm, "end": v(51.54, -3.9) * mm});
            skLineSegment(sketch, "E1259", {"start": v(51.54, -3.9) * mm, "end": v(51.48, -4.16) * mm});
            skLineSegment(sketch, "E1260", {"start": v(51.48, -4.16) * mm, "end": v(51.42, -4.4) * mm});
            skLineSegment(sketch, "E1261", {"start": v(51.42, -4.4) * mm, "end": v(51.34, -4.65) * mm});
            skLineSegment(sketch, "E1262", {"start": v(51.34, -4.65) * mm, "end": v(51.25, -4.87) * mm});
            skLineSegment(sketch, "E1263", {"start": v(51.25, -4.87) * mm, "end": v(51.15, -5.1) * mm});
            skLineSegment(sketch, "E1264", {"start": v(51.15, -5.1) * mm, "end": v(51.05, -5.3) * mm});
            skLineSegment(sketch, "E1265", {"start": v(51.05, -5.3) * mm, "end": v(50.93, -5.5) * mm});
            skLineSegment(sketch, "E1266", {"start": v(50.93, -5.5) * mm, "end": v(50.8, -5.7) * mm});
            skLineSegment(sketch, "E1267", {"start": v(50.8, -5.7) * mm, "end": v(50.66, -5.88) * mm});
            skLineSegment(sketch, "E1268", {"start": v(50.66, -5.88) * mm, "end": v(50.5, -6.05) * mm});
            skLineSegment(sketch, "E1269", {"start": v(50.5, -6.05) * mm, "end": v(50.34, -6.22) * mm});
            skLineSegment(sketch, "E1270", {"start": v(50.34, -6.22) * mm, "end": v(50.17, -6.37) * mm});
            skLineSegment(sketch, "E1271", {"start": v(50.17, -6.37) * mm, "end": v(49.99, -6.51) * mm});
            skLineSegment(sketch, "E1272", {"start": v(49.99, -6.51) * mm, "end": v(49.8, -6.65) * mm});
            skLineSegment(sketch, "E1273", {"start": v(49.8, -6.65) * mm, "end": v(49.59, -6.77) * mm});
            skLineSegment(sketch, "E1274", {"start": v(49.59, -6.77) * mm, "end": v(49.37, -6.89) * mm});
            skLineSegment(sketch, "E1275", {"start": v(49.37, -6.89) * mm, "end": v(49.14, -7) * mm});
            skLineSegment(sketch, "E1276", {"start": v(49.14, -7) * mm, "end": v(48.9, -7.09) * mm});
            skLineSegment(sketch, "E1277", {"start": v(48.9, -7.09) * mm, "end": v(48.65, -7.17) * mm});
            skLineSegment(sketch, "E1278", {"start": v(48.65, -7.17) * mm, "end": v(48.39, -7.25) * mm});
            skLineSegment(sketch, "E1279", {"start": v(48.39, -7.25) * mm, "end": v(48.11, -7.32) * mm});
            skLineSegment(sketch, "E1280", {"start": v(48.11, -7.32) * mm, "end": v(47.83, -7.37) * mm});
            skLineSegment(sketch, "E1281", {"start": v(47.83, -7.37) * mm, "end": v(47.53, -7.42) * mm});
            skLineSegment(sketch, "E1282", {"start": v(47.53, -7.42) * mm, "end": v(47.22, -7.45) * mm});
            skLineSegment(sketch, "E1283", {"start": v(47.22, -7.45) * mm, "end": v(46.9, -7.48) * mm});
            skLineSegment(sketch, "E1284", {"start": v(46.9, -7.48) * mm, "end": v(46.57, -7.5) * mm});
            skLineSegment(sketch, "E1285", {"start": v(46.57, -7.5) * mm, "end": v(46.23, -7.5) * mm});
            skLineSegment(sketch, "E1286", {"start": v(46.23, -7.5) * mm, "end": v(45.71, -7.49) * mm});
            skLineSegment(sketch, "E1287", {"start": v(45.71, -7.49) * mm, "end": v(45.47, -7.47) * mm});
            skLineSegment(sketch, "E1288", {"start": v(45.47, -7.47) * mm, "end": v(45.24, -7.44) * mm});
            skLineSegment(sketch, "E1289", {"start": v(45.24, -7.44) * mm, "end": v(45.01, -7.41) * mm});
            skLineSegment(sketch, "E1290", {"start": v(45.01, -7.41) * mm, "end": v(44.8, -7.38) * mm});
            skLineSegment(sketch, "E1291", {"start": v(44.8, -7.38) * mm, "end": v(44.58, -7.33) * mm});
            skLineSegment(sketch, "E1292", {"start": v(44.58, -7.33) * mm, "end": v(44.38, -7.28) * mm});
            skLineSegment(sketch, "E1293", {"start": v(44.38, -7.28) * mm, "end": v(44.2, -7.22) * mm});
            skLineSegment(sketch, "E1294", {"start": v(44.2, -7.22) * mm, "end": v(44, -7.16) * mm});
            skLineSegment(sketch, "E1295", {"start": v(44, -7.16) * mm, "end": v(43.83, -7.08) * mm});
            skLineSegment(sketch, "E1296", {"start": v(43.83, -7.08) * mm, "end": v(43.67, -7) * mm});
            skLineSegment(sketch, "E1297", {"start": v(43.67, -7) * mm, "end": v(43.51, -6.92) * mm});
            skLineSegment(sketch, "E1298", {"start": v(43.51, -6.92) * mm, "end": v(43.36, -6.83) * mm});
            skLineSegment(sketch, "E1299", {"start": v(43.36, -6.83) * mm, "end": v(43.22, -6.73) * mm});
            skLineSegment(sketch, "E1300", {"start": v(43.22, -6.73) * mm, "end": v(43.1, -6.62) * mm});
            skLineSegment(sketch, "E1301", {"start": v(43.1, -6.62) * mm, "end": v(42.97, -6.5) * mm});
            skLineSegment(sketch, "E1302", {"start": v(42.97, -6.5) * mm, "end": v(42.85, -6.39) * mm});
            skLineSegment(sketch, "E1303", {"start": v(42.85, -6.39) * mm, "end": v(42.74, -6.26) * mm});
            skLineSegment(sketch, "E1304", {"start": v(42.74, -6.26) * mm, "end": v(42.64, -6.13) * mm});
            skLineSegment(sketch, "E1305", {"start": v(42.64, -6.13) * mm, "end": v(42.55, -6) * mm});
            skLineSegment(sketch, "E1306", {"start": v(42.55, -6) * mm, "end": v(42.47, -5.85) * mm});
            skLineSegment(sketch, "E1307", {"start": v(42.47, -5.85) * mm, "end": v(42.4, -5.7) * mm});
            skLineSegment(sketch, "E1308", {"start": v(42.4, -5.7) * mm, "end": v(42.32, -5.55) * mm});
            skLineSegment(sketch, "E1309", {"start": v(42.32, -5.55) * mm, "end": v(42.27, -5.39) * mm});
            skLineSegment(sketch, "E1310", {"start": v(42.27, -5.39) * mm, "end": v(42.21, -5.22) * mm});
            skLineSegment(sketch, "E1311", {"start": v(42.21, -5.22) * mm, "end": v(42.17, -5.05) * mm});
            skLineSegment(sketch, "E1312", {"start": v(42.17, -5.05) * mm, "end": v(42.13, -4.87) * mm});
            skLineSegment(sketch, "E1313", {"start": v(42.13, -4.87) * mm, "end": v(42.1, -4.69) * mm});
            skLineSegment(sketch, "E1314", {"start": v(42.1, -4.69) * mm, "end": v(42.09, -4.5) * mm});
            skLineSegment(sketch, "E1315", {"start": v(42.09, -4.5) * mm, "end": v(42.07, -4.3) * mm});
            skLineSegment(sketch, "E1316", {"start": v(42.07, -4.3) * mm, "end": v(42.07, -4.1) * mm});
            skLineSegment(sketch, "E1317", {"start": v(42.07, -4.1) * mm, "end": v(42.08, -3.66) * mm});
            skLineSegment(sketch, "E1318", {"start": v(42.08, -3.66) * mm, "end": v(42.12, -3.23) * mm});
            skLineSegment(sketch, "E1319", {"start": v(42.12, -3.23) * mm, "end": v(42.2, -2.83) * mm});
            skLineSegment(sketch, "E1320", {"start": v(42.2, -2.83) * mm, "end": v(42.24, -2.64) * mm});
            skLineSegment(sketch, "E1321", {"start": v(42.24, -2.64) * mm, "end": v(42.29, -2.45) * mm});
            skLineSegment(sketch, "E1322", {"start": v(42.29, -2.45) * mm, "end": v(42.34, -2.27) * mm});
            skLineSegment(sketch, "E1323", {"start": v(42.34, -2.27) * mm, "end": v(42.4, -2.1) * mm});
            skLineSegment(sketch, "E1324", {"start": v(42.4, -2.1) * mm, "end": v(42.48, -1.92) * mm});
            skLineSegment(sketch, "E1325", {"start": v(42.48, -1.92) * mm, "end": v(42.56, -1.76) * mm});
            skLineSegment(sketch, "E1326", {"start": v(42.56, -1.76) * mm, "end": v(42.64, -1.6) * mm});
            skLineSegment(sketch, "E1327", {"start": v(42.64, -1.6) * mm, "end": v(42.73, -1.45) * mm});
            skLineSegment(sketch, "E1328", {"start": v(42.73, -1.45) * mm, "end": v(42.83, -1.3) * mm});
            skLineSegment(sketch, "E1329", {"start": v(42.83, -1.3) * mm, "end": v(42.94, -1.16) * mm});
            skLineSegment(sketch, "E1330", {"start": v(42.94, -1.16) * mm, "end": v(43.17, -0.9) * mm});
            skLineSegment(sketch, "E1331", {"start": v(43.17, -0.9) * mm, "end": v(43.42, -0.64) * mm});
            skLineSegment(sketch, "E1332", {"start": v(43.42, -0.64) * mm, "end": v(43.7, -0.41) * mm});
            skLineSegment(sketch, "E1333", {"start": v(43.7, -0.41) * mm, "end": v(44, -0.2) * mm});
            skLineSegment(sketch, "E1334", {"start": v(44, -0.2) * mm, "end": v(44.31, -0.01) * mm});
            skLineSegment(sketch, "E1335", {"start": v(44.31, -0.01) * mm, "end": v(44.66, 0.16) * mm});
            skLineSegment(sketch, "E1336", {"start": v(44.66, 0.16) * mm, "end": v(45.02, 0.3) * mm});
            skLineSegment(sketch, "E1337", {"start": v(45.02, 0.3) * mm, "end": v(45.41, 0.43) * mm});
            skLineSegment(sketch, "E1338", {"start": v(45.41, 0.43) * mm, "end": v(45.24, 0.52) * mm});
            skLineSegment(sketch, "E1339", {"start": v(45.24, 0.52) * mm, "end": v(45.08, 0.6) * mm});
            skLineSegment(sketch, "E1340", {"start": v(45.08, 0.6) * mm, "end": v(44.92, 0.7) * mm});
            skLineSegment(sketch, "E1341", {"start": v(44.92, 0.7) * mm, "end": v(44.78, 0.82) * mm});
            skLineSegment(sketch, "E1342", {"start": v(44.78, 0.82) * mm, "end": v(44.63, 0.95) * mm});
            skLineSegment(sketch, "E1343", {"start": v(44.63, 0.95) * mm, "end": v(44.5, 1.08) * mm});
            skLineSegment(sketch, "E1344", {"start": v(44.5, 1.08) * mm, "end": v(44.37, 1.22) * mm});
            skLineSegment(sketch, "E1345", {"start": v(44.37, 1.22) * mm, "end": v(44.25, 1.38) * mm});
            skLineSegment(sketch, "E1346", {"start": v(44.25, 1.38) * mm, "end": v(44.2, 1.46) * mm});
            skLineSegment(sketch, "E1347", {"start": v(44.2, 1.46) * mm, "end": v(44.14, 1.55) * mm});
            skLineSegment(sketch, "E1348", {"start": v(44.14, 1.55) * mm, "end": v(44.1, 1.63) * mm});
            skLineSegment(sketch, "E1349", {"start": v(44.1, 1.63) * mm, "end": v(44.05, 1.73) * mm});
            skLineSegment(sketch, "E1350", {"start": v(44.05, 1.73) * mm, "end": v(43.97, 1.91) * mm});
            skLineSegment(sketch, "E1351", {"start": v(43.97, 1.91) * mm, "end": v(43.9, 2.11) * mm});
            skLineSegment(sketch, "E1352", {"start": v(43.9, 2.11) * mm, "end": v(43.86, 2.32) * mm});
            skLineSegment(sketch, "E1353", {"start": v(43.86, 2.32) * mm, "end": v(43.82, 2.54) * mm});
            skLineSegment(sketch, "E1354", {"start": v(43.82, 2.54) * mm, "end": v(43.8, 2.78) * mm});
            skLineSegment(sketch, "E1355", {"start": v(43.8, 2.78) * mm, "end": v(43.8, 3.02) * mm});
            skLineSegment(sketch, "E1356", {"start": v(43.8, 3.02) * mm, "end": v(43.8, 3.27) * mm});
            skLineSegment(sketch, "E1357", {"start": v(43.8, 3.27) * mm, "end": v(43.81, 3.53) * mm});
            skLineSegment(sketch, "E1358", {"start": v(43.81, 3.53) * mm, "end": v(43.84, 3.77) * mm});
            skLineSegment(sketch, "E1359", {"start": v(43.84, 3.77) * mm, "end": v(43.87, 4) * mm});
            skLineSegment(sketch, "E1360", {"start": v(43.87, 4) * mm, "end": v(43.9, 4.24) * mm});
            skLineSegment(sketch, "E1361", {"start": v(43.9, 4.24) * mm, "end": v(43.96, 4.46) * mm});
            skLineSegment(sketch, "E1362", {"start": v(43.96, 4.46) * mm, "end": v(44.02, 4.68) * mm});
            skLineSegment(sketch, "E1363", {"start": v(44.02, 4.68) * mm, "end": v(44.09, 4.9) * mm});
            skLineSegment(sketch, "E1364", {"start": v(44.09, 4.9) * mm, "end": v(44.17, 5.1) * mm});
            skLineSegment(sketch, "E1365", {"start": v(44.17, 5.1) * mm, "end": v(44.25, 5.3) * mm});
            skLineSegment(sketch, "E1366", {"start": v(44.25, 5.3) * mm, "end": v(44.35, 5.49) * mm});
            skLineSegment(sketch, "E1367", {"start": v(44.35, 5.49) * mm, "end": v(44.46, 5.67) * mm});
            skLineSegment(sketch, "E1368", {"start": v(44.46, 5.67) * mm, "end": v(44.58, 5.84) * mm});
            skLineSegment(sketch, "E1369", {"start": v(44.58, 5.84) * mm, "end": v(44.7, 6) * mm});
            skLineSegment(sketch, "E1370", {"start": v(44.7, 6) * mm, "end": v(44.84, 6.16) * mm});
            skLineSegment(sketch, "E1371", {"start": v(44.84, 6.16) * mm, "end": v(44.99, 6.3) * mm});
            skLineSegment(sketch, "E1372", {"start": v(44.99, 6.3) * mm, "end": v(45.15, 6.45) * mm});
            skLineSegment(sketch, "E1373", {"start": v(45.15, 6.45) * mm, "end": v(45.31, 6.58) * mm});
            skLineSegment(sketch, "E1374", {"start": v(45.31, 6.58) * mm, "end": v(45.49, 6.7) * mm});
            skLineSegment(sketch, "E1375", {"start": v(45.49, 6.7) * mm, "end": v(45.68, 6.81) * mm});
            skLineSegment(sketch, "E1376", {"start": v(45.68, 6.81) * mm, "end": v(45.87, 6.92) * mm});
            skLineSegment(sketch, "E1377", {"start": v(45.87, 6.92) * mm, "end": v(46.08, 7.02) * mm});
            skLineSegment(sketch, "E1378", {"start": v(46.08, 7.02) * mm, "end": v(46.3, 7.1) * mm});
            skLineSegment(sketch, "E1379", {"start": v(46.3, 7.1) * mm, "end": v(46.52, 7.19) * mm});
            skLineSegment(sketch, "E1380", {"start": v(46.52, 7.19) * mm, "end": v(46.76, 7.26) * mm});
            skLineSegment(sketch, "E1381", {"start": v(46.76, 7.26) * mm, "end": v(47, 7.32) * mm});
            skLineSegment(sketch, "E1382", {"start": v(47, 7.32) * mm, "end": v(47.27, 7.38) * mm});
            skLineSegment(sketch, "E1383", {"start": v(47.27, 7.38) * mm, "end": v(47.53, 7.42) * mm});
            skLineSegment(sketch, "E1384", {"start": v(47.53, 7.42) * mm, "end": v(47.81, 7.46) * mm});
            skLineSegment(sketch, "E1385", {"start": v(47.81, 7.46) * mm, "end": v(48.1, 7.48) * mm});
            skLineSegment(sketch, "E1386", {"start": v(48.1, 7.48) * mm, "end": v(48.4, 7.5) * mm});
            skLineSegment(sketch, "E1387", {"start": v(48.4, 7.5) * mm, "end": v(48.71, 7.5) * mm});
            skLineSegment(sketch, "E1388", {"start": v(48.71, 7.5) * mm, "end": v(49.18, 7.49) * mm});
            skLineSegment(sketch, "E1389", {"start": v(49.18, 7.49) * mm, "end": v(49.4, 7.47) * mm});
            skLineSegment(sketch, "E1390", {"start": v(49.4, 7.47) * mm, "end": v(49.6, 7.45) * mm});
            skLineSegment(sketch, "E1391", {"start": v(49.6, 7.45) * mm, "end": v(49.81, 7.43) * mm});
            skLineSegment(sketch, "E1392", {"start": v(49.81, 7.43) * mm, "end": v(50.01, 7.4) * mm});
            skLineSegment(sketch, "E1393", {"start": v(50.01, 7.4) * mm, "end": v(50.2, 7.35) * mm});
            skLineSegment(sketch, "E1394", {"start": v(50.2, 7.35) * mm, "end": v(50.38, 7.31) * mm});
            skLineSegment(sketch, "E1395", {"start": v(50.38, 7.31) * mm, "end": v(50.55, 7.26) * mm});
            skLineSegment(sketch, "E1396", {"start": v(50.55, 7.26) * mm, "end": v(50.72, 7.2) * mm});
            skLineSegment(sketch, "E1397", {"start": v(50.72, 7.2) * mm, "end": v(50.88, 7.14) * mm});
            skLineSegment(sketch, "E1398", {"start": v(50.88, 7.14) * mm, "end": v(51.03, 7.07) * mm});
            skLineSegment(sketch, "E1399", {"start": v(51.03, 7.07) * mm, "end": v(51.17, 7) * mm});
            skLineSegment(sketch, "E1400", {"start": v(51.17, 7) * mm, "end": v(51.3, 6.92) * mm});
            skLineSegment(sketch, "E1401", {"start": v(51.3, 6.92) * mm, "end": v(51.43, 6.83) * mm});
            skLineSegment(sketch, "E1402", {"start": v(51.43, 6.83) * mm, "end": v(51.55, 6.74) * mm});
            skLineSegment(sketch, "E1403", {"start": v(51.55, 6.74) * mm, "end": v(51.66, 6.64) * mm});
            skLineSegment(sketch, "E1404", {"start": v(51.66, 6.64) * mm, "end": v(51.76, 6.54) * mm});
            skLineSegment(sketch, "E1405", {"start": v(51.76, 6.54) * mm, "end": v(51.86, 6.43) * mm});
            skLineSegment(sketch, "E1406", {"start": v(51.86, 6.43) * mm, "end": v(51.95, 6.32) * mm});
            skLineSegment(sketch, "E1407", {"start": v(51.95, 6.32) * mm, "end": v(52.03, 6.2) * mm});
            skLineSegment(sketch, "E1408", {"start": v(52.03, 6.2) * mm, "end": v(52.1, 6.08) * mm});
            skLineSegment(sketch, "E1409", {"start": v(52.1, 6.08) * mm, "end": v(52.18, 5.95) * mm});
            skLineSegment(sketch, "E1410", {"start": v(52.18, 5.95) * mm, "end": v(52.24, 5.82) * mm});
            skLineSegment(sketch, "E1411", {"start": v(52.24, 5.82) * mm, "end": v(52.3, 5.68) * mm});
            skLineSegment(sketch, "E1412", {"start": v(52.3, 5.68) * mm, "end": v(52.34, 5.54) * mm});
            skLineSegment(sketch, "E1413", {"start": v(52.34, 5.54) * mm, "end": v(52.38, 5.39) * mm});
            skLineSegment(sketch, "E1414", {"start": v(52.38, 5.39) * mm, "end": v(52.4, 5.23) * mm});
            skLineSegment(sketch, "E1415", {"start": v(52.4, 5.23) * mm, "end": v(52.44, 5.08) * mm});
            skLineSegment(sketch, "E1416", {"start": v(52.44, 5.08) * mm, "end": v(52.45, 4.91) * mm});
            skLineSegment(sketch, "E1417", {"start": v(52.45, 4.91) * mm, "end": v(52.46, 4.74) * mm});
            skLineSegment(sketch, "E1418", {"start": v(52.46, 4.74) * mm, "end": v(52.47, 4.57) * mm});
            skLineSegment(sketch, "E1419", {"start": v(46.36, -6.64) * mm, "end": v(46.6, -6.64) * mm});
            skLineSegment(sketch, "E1420", {"start": v(46.6, -6.64) * mm, "end": v(46.84, -6.62) * mm});
            skLineSegment(sketch, "E1421", {"start": v(46.84, -6.62) * mm, "end": v(47.06, -6.6) * mm});
            skLineSegment(sketch, "E1422", {"start": v(47.06, -6.6) * mm, "end": v(47.28, -6.57) * mm});
            skLineSegment(sketch, "E1423", {"start": v(47.28, -6.57) * mm, "end": v(47.48, -6.52) * mm});
            skLineSegment(sketch, "E1424", {"start": v(47.48, -6.52) * mm, "end": v(47.67, -6.47) * mm});
            skLineSegment(sketch, "E1425", {"start": v(47.67, -6.47) * mm, "end": v(47.85, -6.4) * mm});
            skLineSegment(sketch, "E1426", {"start": v(47.85, -6.4) * mm, "end": v(48.02, -6.34) * mm});
            skLineSegment(sketch, "E1427", {"start": v(48.02, -6.34) * mm, "end": v(48.18, -6.26) * mm});
            skLineSegment(sketch, "E1428", {"start": v(48.18, -6.26) * mm, "end": v(48.33, -6.17) * mm});
            skLineSegment(sketch, "E1429", {"start": v(48.33, -6.17) * mm, "end": v(48.47, -6.07) * mm});
            skLineSegment(sketch, "E1430", {"start": v(48.47, -6.07) * mm, "end": v(48.6, -5.96) * mm});
            skLineSegment(sketch, "E1431", {"start": v(48.6, -5.96) * mm, "end": v(48.73, -5.85) * mm});
            skLineSegment(sketch, "E1432", {"start": v(48.73, -5.85) * mm, "end": v(48.85, -5.73) * mm});
            skLineSegment(sketch, "E1433", {"start": v(48.85, -5.73) * mm, "end": v(48.96, -5.6) * mm});
            skLineSegment(sketch, "E1434", {"start": v(48.96, -5.6) * mm, "end": v(49.06, -5.47) * mm});
            skLineSegment(sketch, "E1435", {"start": v(49.06, -5.47) * mm, "end": v(49.15, -5.33) * mm});
            skLineSegment(sketch, "E1436", {"start": v(49.15, -5.33) * mm, "end": v(49.24, -5.18) * mm});
            skLineSegment(sketch, "E1437", {"start": v(49.24, -5.18) * mm, "end": v(49.32, -5.02) * mm});
            skLineSegment(sketch, "E1438", {"start": v(49.32, -5.02) * mm, "end": v(49.39, -4.86) * mm});
            skLineSegment(sketch, "E1439", {"start": v(49.39, -4.86) * mm, "end": v(49.45, -4.7) * mm});
            skLineSegment(sketch, "E1440", {"start": v(49.45, -4.7) * mm, "end": v(49.5, -4.52) * mm});
            skLineSegment(sketch, "E1441", {"start": v(49.5, -4.52) * mm, "end": v(49.55, -4.34) * mm});
            skLineSegment(sketch, "E1442", {"start": v(49.55, -4.34) * mm, "end": v(49.6, -4.15) * mm});
            skLineSegment(sketch, "E1443", {"start": v(49.6, -4.15) * mm, "end": v(49.66, -3.75) * mm});
            skLineSegment(sketch, "E1444", {"start": v(49.66, -3.75) * mm, "end": v(49.7, -3.33) * mm});
            skLineSegment(sketch, "E1445", {"start": v(49.7, -3.33) * mm, "end": v(49.73, -2.89) * mm});
            skLineSegment(sketch, "E1446", {"start": v(49.73, -2.89) * mm, "end": v(49.74, -2.43) * mm});
            skLineSegment(sketch, "E1447", {"start": v(49.74, -2.43) * mm, "end": v(49.74, -2.18) * mm});
            skLineSegment(sketch, "E1448", {"start": v(49.74, -2.18) * mm, "end": v(49.71, -1.93) * mm});
            skLineSegment(sketch, "E1449", {"start": v(49.71, -1.93) * mm, "end": v(49.67, -1.7) * mm});
            skLineSegment(sketch, "E1450", {"start": v(49.67, -1.7) * mm, "end": v(49.61, -1.48) * mm});
            skLineSegment(sketch, "E1451", {"start": v(49.61, -1.48) * mm, "end": v(49.58, -1.37) * mm});
            skLineSegment(sketch, "E1452", {"start": v(49.58, -1.37) * mm, "end": v(49.54, -1.27) * mm});
            skLineSegment(sketch, "E1453", {"start": v(49.54, -1.27) * mm, "end": v(49.5, -1.17) * mm});
            skLineSegment(sketch, "E1454", {"start": v(49.5, -1.17) * mm, "end": v(49.45, -1.07) * mm});
            skLineSegment(sketch, "E1455", {"start": v(49.45, -1.07) * mm, "end": v(49.4, -0.98) * mm});
            skLineSegment(sketch, "E1456", {"start": v(49.4, -0.98) * mm, "end": v(49.34, -0.9) * mm});
            skLineSegment(sketch, "E1457", {"start": v(49.34, -0.9) * mm, "end": v(49.28, -0.8) * mm});
            skLineSegment(sketch, "E1458", {"start": v(49.28, -0.8) * mm, "end": v(49.21, -0.73) * mm});
            skLineSegment(sketch, "E1459", {"start": v(49.21, -0.73) * mm, "end": v(49.14, -0.65) * mm});
            skLineSegment(sketch, "E1460", {"start": v(49.14, -0.65) * mm, "end": v(49.06, -0.57) * mm});
            skLineSegment(sketch, "E1461", {"start": v(49.06, -0.57) * mm, "end": v(48.98, -0.5) * mm});
            skLineSegment(sketch, "E1462", {"start": v(48.98, -0.5) * mm, "end": v(48.89, -0.44) * mm});
            skLineSegment(sketch, "E1463", {"start": v(48.89, -0.44) * mm, "end": v(48.8, -0.38) * mm});
            skLineSegment(sketch, "E1464", {"start": v(48.8, -0.38) * mm, "end": v(48.7, -0.32) * mm});
            skLineSegment(sketch, "E1465", {"start": v(48.7, -0.32) * mm, "end": v(48.6, -0.27) * mm});
            skLineSegment(sketch, "E1466", {"start": v(48.6, -0.27) * mm, "end": v(48.48, -0.23) * mm});
            skLineSegment(sketch, "E1467", {"start": v(48.48, -0.23) * mm, "end": v(48.37, -0.19) * mm});
            skLineSegment(sketch, "E1468", {"start": v(48.37, -0.19) * mm, "end": v(48.25, -0.15) * mm});
            skLineSegment(sketch, "E1469", {"start": v(48.25, -0.15) * mm, "end": v(48.12, -0.12) * mm});
            skLineSegment(sketch, "E1470", {"start": v(48.12, -0.12) * mm, "end": v(48, -0.1) * mm});
            skLineSegment(sketch, "E1471", {"start": v(48, -0.1) * mm, "end": v(47.85, -0.08) * mm});
            skLineSegment(sketch, "E1472", {"start": v(47.85, -0.08) * mm, "end": v(47.7, -0.07) * mm});
            skLineSegment(sketch, "E1473", {"start": v(47.7, -0.07) * mm, "end": v(47.56, -0.06) * mm});
            skLineSegment(sketch, "E1474", {"start": v(47.56, -0.06) * mm, "end": v(47.4, -0.05) * mm});
            skLineSegment(sketch, "E1475", {"start": v(47.4, -0.05) * mm, "end": v(47.17, -0.06) * mm});
            skLineSegment(sketch, "E1476", {"start": v(47.17, -0.06) * mm, "end": v(46.95, -0.07) * mm});
            skLineSegment(sketch, "E1477", {"start": v(46.95, -0.07) * mm, "end": v(46.73, -0.1) * mm});
            skLineSegment(sketch, "E1478", {"start": v(46.73, -0.1) * mm, "end": v(46.53, -0.13) * mm});
            skLineSegment(sketch, "E1479", {"start": v(46.53, -0.13) * mm, "end": v(46.33, -0.17) * mm});
            skLineSegment(sketch, "E1480", {"start": v(46.33, -0.17) * mm, "end": v(46.15, -0.22) * mm});
            skLineSegment(sketch, "E1481", {"start": v(46.15, -0.22) * mm, "end": v(45.97, -0.28) * mm});
            skLineSegment(sketch, "E1482", {"start": v(45.97, -0.28) * mm, "end": v(45.8, -0.35) * mm});
            skLineSegment(sketch, "E1483", {"start": v(45.8, -0.35) * mm, "end": v(45.64, -0.42) * mm});
            skLineSegment(sketch, "E1484", {"start": v(45.64, -0.42) * mm, "end": v(45.5, -0.5) * mm});
            skLineSegment(sketch, "E1485", {"start": v(45.5, -0.5) * mm, "end": v(45.35, -0.6) * mm});
            skLineSegment(sketch, "E1486", {"start": v(45.35, -0.6) * mm, "end": v(45.21, -0.7) * mm});
            skLineSegment(sketch, "E1487", {"start": v(45.21, -0.7) * mm, "end": v(45.09, -0.81) * mm});
            skLineSegment(sketch, "E1488", {"start": v(45.09, -0.81) * mm, "end": v(44.97, -0.93) * mm});
            skLineSegment(sketch, "E1489", {"start": v(44.97, -0.93) * mm, "end": v(44.85, -1.05) * mm});
            skLineSegment(sketch, "E1490", {"start": v(44.85, -1.05) * mm, "end": v(44.75, -1.18) * mm});
            skLineSegment(sketch, "E1491", {"start": v(44.75, -1.18) * mm, "end": v(44.65, -1.32) * mm});
            skLineSegment(sketch, "E1492", {"start": v(44.65, -1.32) * mm, "end": v(44.56, -1.46) * mm});
            skLineSegment(sketch, "E1493", {"start": v(44.56, -1.46) * mm, "end": v(44.48, -1.61) * mm});
            skLineSegment(sketch, "E1494", {"start": v(44.48, -1.61) * mm, "end": v(44.4, -1.77) * mm});
            skLineSegment(sketch, "E1495", {"start": v(44.4, -1.77) * mm, "end": v(44.33, -1.94) * mm});
            skLineSegment(sketch, "E1496", {"start": v(44.33, -1.94) * mm, "end": v(44.27, -2.1) * mm});
            skLineSegment(sketch, "E1497", {"start": v(44.27, -2.1) * mm, "end": v(44.21, -2.29) * mm});
            skLineSegment(sketch, "E1498", {"start": v(44.21, -2.29) * mm, "end": v(44.16, -2.47) * mm});
            skLineSegment(sketch, "E1499", {"start": v(44.16, -2.47) * mm, "end": v(44.09, -2.86) * mm});
            skLineSegment(sketch, "E1500", {"start": v(44.09, -2.86) * mm, "end": v(44.03, -3.27) * mm});
            skLineSegment(sketch, "E1501", {"start": v(44.03, -3.27) * mm, "end": v(44, -3.7) * mm});
            skLineSegment(sketch, "E1502", {"start": v(44, -3.7) * mm, "end": v(44, -4.15) * mm});
            skLineSegment(sketch, "E1503", {"start": v(44, -4.15) * mm, "end": v(44, -4.43) * mm});
            skLineSegment(sketch, "E1504", {"start": v(44, -4.43) * mm, "end": v(44.02, -4.7) * mm});
            skLineSegment(sketch, "E1505", {"start": v(44.02, -4.7) * mm, "end": v(44.06, -4.95) * mm});
            skLineSegment(sketch, "E1506", {"start": v(44.06, -4.95) * mm, "end": v(44.12, -5.19) * mm});
            skLineSegment(sketch, "E1507", {"start": v(44.12, -5.19) * mm, "end": v(44.16, -5.3) * mm});
            skLineSegment(sketch, "E1508", {"start": v(44.16, -5.3) * mm, "end": v(44.2, -5.4) * mm});
            skLineSegment(sketch, "E1509", {"start": v(44.2, -5.4) * mm, "end": v(44.25, -5.51) * mm});
            skLineSegment(sketch, "E1510", {"start": v(44.25, -5.51) * mm, "end": v(44.3, -5.61) * mm});
            skLineSegment(sketch, "E1511", {"start": v(44.3, -5.61) * mm, "end": v(44.35, -5.7) * mm});
            skLineSegment(sketch, "E1512", {"start": v(44.35, -5.7) * mm, "end": v(44.41, -5.8) * mm});
            skLineSegment(sketch, "E1513", {"start": v(44.41, -5.8) * mm, "end": v(44.48, -5.89) * mm});
            skLineSegment(sketch, "E1514", {"start": v(44.48, -5.89) * mm, "end": v(44.54, -5.97) * mm});
            skLineSegment(sketch, "E1515", {"start": v(44.54, -5.97) * mm, "end": v(44.62, -6.05) * mm});
            skLineSegment(sketch, "E1516", {"start": v(44.62, -6.05) * mm, "end": v(44.7, -6.12) * mm});
            skLineSegment(sketch, "E1517", {"start": v(44.7, -6.12) * mm, "end": v(44.79, -6.2) * mm});
            skLineSegment(sketch, "E1518", {"start": v(44.79, -6.2) * mm, "end": v(44.88, -6.26) * mm});
            skLineSegment(sketch, "E1519", {"start": v(44.88, -6.26) * mm, "end": v(44.97, -6.32) * mm});
            skLineSegment(sketch, "E1520", {"start": v(44.97, -6.32) * mm, "end": v(45.07, -6.37) * mm});
            skLineSegment(sketch, "E1521", {"start": v(45.07, -6.37) * mm, "end": v(45.17, -6.42) * mm});
            skLineSegment(sketch, "E1522", {"start": v(45.17, -6.42) * mm, "end": v(45.28, -6.47) * mm});
            skLineSegment(sketch, "E1523", {"start": v(45.28, -6.47) * mm, "end": v(45.4, -6.5) * mm});
            skLineSegment(sketch, "E1524", {"start": v(45.4, -6.5) * mm, "end": v(45.52, -6.54) * mm});
            skLineSegment(sketch, "E1525", {"start": v(45.52, -6.54) * mm, "end": v(45.65, -6.57) * mm});
            skLineSegment(sketch, "E1526", {"start": v(45.65, -6.57) * mm, "end": v(45.78, -6.6) * mm});
            skLineSegment(sketch, "E1527", {"start": v(45.78, -6.6) * mm, "end": v(45.92, -6.62) * mm});
            skLineSegment(sketch, "E1528", {"start": v(45.92, -6.62) * mm, "end": v(46.06, -6.63) * mm});
            skLineSegment(sketch, "E1529", {"start": v(46.06, -6.63) * mm, "end": v(46.2, -6.64) * mm});
            skLineSegment(sketch, "E1530", {"start": v(46.2, -6.64) * mm, "end": v(46.36, -6.64) * mm});
            skLineSegment(sketch, "E1531", {"start": v(47.58, 0.9) * mm, "end": v(47.8, 0.9) * mm});
            skLineSegment(sketch, "E1532", {"start": v(47.8, 0.9) * mm, "end": v(48, 0.92) * mm});
            skLineSegment(sketch, "E1533", {"start": v(48, 0.92) * mm, "end": v(48.19, 0.94) * mm});
            skLineSegment(sketch, "E1534", {"start": v(48.19, 0.94) * mm, "end": v(48.37, 0.98) * mm});
            skLineSegment(sketch, "E1535", {"start": v(48.37, 0.98) * mm, "end": v(48.54, 1.02) * mm});
            skLineSegment(sketch, "E1536", {"start": v(48.54, 1.02) * mm, "end": v(48.7, 1.07) * mm});
            skLineSegment(sketch, "E1537", {"start": v(48.7, 1.07) * mm, "end": v(48.86, 1.13) * mm});
            skLineSegment(sketch, "E1538", {"start": v(48.86, 1.13) * mm, "end": v(49, 1.2) * mm});
            skLineSegment(sketch, "E1539", {"start": v(49, 1.2) * mm, "end": v(49.14, 1.29) * mm});
            skLineSegment(sketch, "E1540", {"start": v(49.14, 1.29) * mm, "end": v(49.27, 1.37) * mm});
            skLineSegment(sketch, "E1541", {"start": v(49.27, 1.37) * mm, "end": v(49.4, 1.47) * mm});
            skLineSegment(sketch, "E1542", {"start": v(49.4, 1.47) * mm, "end": v(49.51, 1.57) * mm});
            skLineSegment(sketch, "E1543", {"start": v(49.51, 1.57) * mm, "end": v(49.62, 1.67) * mm});
            skLineSegment(sketch, "E1544", {"start": v(49.62, 1.67) * mm, "end": v(49.72, 1.79) * mm});
            skLineSegment(sketch, "E1545", {"start": v(49.72, 1.79) * mm, "end": v(49.82, 1.9) * mm});
            skLineSegment(sketch, "E1546", {"start": v(49.82, 1.9) * mm, "end": v(49.9, 2.03) * mm});
            skLineSegment(sketch, "E1547", {"start": v(49.9, 2.03) * mm, "end": v(49.99, 2.16) * mm});
            skLineSegment(sketch, "E1548", {"start": v(49.99, 2.16) * mm, "end": v(50.07, 2.3) * mm});
            skLineSegment(sketch, "E1549", {"start": v(50.07, 2.3) * mm, "end": v(50.14, 2.43) * mm});
            skLineSegment(sketch, "E1550", {"start": v(50.14, 2.43) * mm, "end": v(50.2, 2.58) * mm});
            skLineSegment(sketch, "E1551", {"start": v(50.2, 2.58) * mm, "end": v(50.26, 2.73) * mm});
            skLineSegment(sketch, "E1552", {"start": v(50.26, 2.73) * mm, "end": v(50.31, 2.88) * mm});
            skLineSegment(sketch, "E1553", {"start": v(50.31, 2.88) * mm, "end": v(50.36, 3.04) * mm});
            skLineSegment(sketch, "E1554", {"start": v(50.36, 3.04) * mm, "end": v(50.4, 3.2) * mm});
            skLineSegment(sketch, "E1555", {"start": v(50.4, 3.2) * mm, "end": v(50.46, 3.54) * mm});
            skLineSegment(sketch, "E1556", {"start": v(50.46, 3.54) * mm, "end": v(50.5, 3.87) * mm});
            skLineSegment(sketch, "E1557", {"start": v(50.5, 3.87) * mm, "end": v(50.53, 4.22) * mm});
            skLineSegment(sketch, "E1558", {"start": v(50.53, 4.22) * mm, "end": v(50.54, 4.57) * mm});
            skLineSegment(sketch, "E1559", {"start": v(50.54, 4.57) * mm, "end": v(50.53, 4.8) * mm});
            skLineSegment(sketch, "E1560", {"start": v(50.53, 4.8) * mm, "end": v(50.5, 5.02) * mm});
            skLineSegment(sketch, "E1561", {"start": v(50.5, 5.02) * mm, "end": v(50.47, 5.23) * mm});
            skLineSegment(sketch, "E1562", {"start": v(50.47, 5.23) * mm, "end": v(50.45, 5.33) * mm});
            skLineSegment(sketch, "E1563", {"start": v(50.45, 5.33) * mm, "end": v(50.43, 5.43) * mm});
            skLineSegment(sketch, "E1564", {"start": v(50.43, 5.43) * mm, "end": v(50.4, 5.52) * mm});
            skLineSegment(sketch, "E1565", {"start": v(50.4, 5.52) * mm, "end": v(50.37, 5.61) * mm});
            skLineSegment(sketch, "E1566", {"start": v(50.37, 5.61) * mm, "end": v(50.34, 5.7) * mm});
            skLineSegment(sketch, "E1567", {"start": v(50.34, 5.7) * mm, "end": v(50.3, 5.79) * mm});
            skLineSegment(sketch, "E1568", {"start": v(50.3, 5.79) * mm, "end": v(50.25, 5.86) * mm});
            skLineSegment(sketch, "E1569", {"start": v(50.25, 5.86) * mm, "end": v(50.2, 5.94) * mm});
            skLineSegment(sketch, "E1570", {"start": v(50.2, 5.94) * mm, "end": v(50.16, 6.01) * mm});
            skLineSegment(sketch, "E1571", {"start": v(50.16, 6.01) * mm, "end": v(50.1, 6.08) * mm});
            skLineSegment(sketch, "E1572", {"start": v(50.1, 6.08) * mm, "end": v(50.04, 6.14) * mm});
            skLineSegment(sketch, "E1573", {"start": v(50.04, 6.14) * mm, "end": v(49.98, 6.2) * mm});
            skLineSegment(sketch, "E1574", {"start": v(49.98, 6.2) * mm, "end": v(49.9, 6.26) * mm});
            skLineSegment(sketch, "E1575", {"start": v(49.9, 6.26) * mm, "end": v(49.84, 6.32) * mm});
            skLineSegment(sketch, "E1576", {"start": v(49.84, 6.32) * mm, "end": v(49.76, 6.37) * mm});
            skLineSegment(sketch, "E1577", {"start": v(49.76, 6.37) * mm, "end": v(49.67, 6.41) * mm});
            skLineSegment(sketch, "E1578", {"start": v(49.67, 6.41) * mm, "end": v(49.59, 6.45) * mm});
            skLineSegment(sketch, "E1579", {"start": v(49.59, 6.45) * mm, "end": v(49.5, 6.5) * mm});
            skLineSegment(sketch, "E1580", {"start": v(49.5, 6.5) * mm, "end": v(49.4, 6.52) * mm});
            skLineSegment(sketch, "E1581", {"start": v(49.4, 6.52) * mm, "end": v(49.3, 6.55) * mm});
            skLineSegment(sketch, "E1582", {"start": v(49.3, 6.55) * mm, "end": v(49.2, 6.58) * mm});
            skLineSegment(sketch, "E1583", {"start": v(49.2, 6.58) * mm, "end": v(49.08, 6.6) * mm});
            skLineSegment(sketch, "E1584", {"start": v(49.08, 6.6) * mm, "end": v(48.97, 6.61) * mm});
            skLineSegment(sketch, "E1585", {"start": v(48.97, 6.61) * mm, "end": v(48.85, 6.62) * mm});
            skLineSegment(sketch, "E1586", {"start": v(48.85, 6.62) * mm, "end": v(48.72, 6.63) * mm});
            skLineSegment(sketch, "E1587", {"start": v(48.72, 6.63) * mm, "end": v(48.6, 6.63) * mm});
            skLineSegment(sketch, "E1588", {"start": v(48.6, 6.63) * mm, "end": v(48.38, 6.63) * mm});
            skLineSegment(sketch, "E1589", {"start": v(48.38, 6.63) * mm, "end": v(48.18, 6.61) * mm});
            skLineSegment(sketch, "E1590", {"start": v(48.18, 6.61) * mm, "end": v(48, 6.6) * mm});
            skLineSegment(sketch, "E1591", {"start": v(48, 6.6) * mm, "end": v(47.8, 6.56) * mm});
            skLineSegment(sketch, "E1592", {"start": v(47.8, 6.56) * mm, "end": v(47.64, 6.52) * mm});
            skLineSegment(sketch, "E1593", {"start": v(47.64, 6.52) * mm, "end": v(47.47, 6.47) * mm});
            skLineSegment(sketch, "E1594", {"start": v(47.47, 6.47) * mm, "end": v(47.32, 6.4) * mm});
            skLineSegment(sketch, "E1595", {"start": v(47.32, 6.4) * mm, "end": v(47.17, 6.34) * mm});
            skLineSegment(sketch, "E1596", {"start": v(47.17, 6.34) * mm, "end": v(47.04, 6.26) * mm});
            skLineSegment(sketch, "E1597", {"start": v(47.04, 6.26) * mm, "end": v(46.9, 6.18) * mm});
            skLineSegment(sketch, "E1598", {"start": v(46.9, 6.18) * mm, "end": v(46.79, 6.1) * mm});
            skLineSegment(sketch, "E1599", {"start": v(46.79, 6.1) * mm, "end": v(46.67, 6) * mm});
            skLineSegment(sketch, "E1600", {"start": v(46.67, 6) * mm, "end": v(46.57, 5.9) * mm});
            skLineSegment(sketch, "E1601", {"start": v(46.57, 5.9) * mm, "end": v(46.47, 5.8) * mm});
            skLineSegment(sketch, "E1602", {"start": v(46.47, 5.8) * mm, "end": v(46.38, 5.68) * mm});
            skLineSegment(sketch, "E1603", {"start": v(46.38, 5.68) * mm, "end": v(46.3, 5.56) * mm});
            skLineSegment(sketch, "E1604", {"start": v(46.3, 5.56) * mm, "end": v(46.21, 5.43) * mm});
            skLineSegment(sketch, "E1605", {"start": v(46.21, 5.43) * mm, "end": v(46.14, 5.3) * mm});
            skLineSegment(sketch, "E1606", {"start": v(46.14, 5.3) * mm, "end": v(46.08, 5.16) * mm});
            skLineSegment(sketch, "E1607", {"start": v(46.08, 5.16) * mm, "end": v(46.02, 5.02) * mm});
            skLineSegment(sketch, "E1608", {"start": v(46.02, 5.02) * mm, "end": v(45.96, 4.87) * mm});
            skLineSegment(sketch, "E1609", {"start": v(45.96, 4.87) * mm, "end": v(45.91, 4.72) * mm});
            skLineSegment(sketch, "E1610", {"start": v(45.91, 4.72) * mm, "end": v(45.87, 4.56) * mm});
            skLineSegment(sketch, "E1611", {"start": v(45.87, 4.56) * mm, "end": v(45.84, 4.4) * mm});
            skLineSegment(sketch, "E1612", {"start": v(45.84, 4.4) * mm, "end": v(45.78, 4.06) * mm});
            skLineSegment(sketch, "E1613", {"start": v(45.78, 4.06) * mm, "end": v(45.74, 3.7) * mm});
            skLineSegment(sketch, "E1614", {"start": v(45.74, 3.7) * mm, "end": v(45.71, 3.35) * mm});
            skLineSegment(sketch, "E1615", {"start": v(45.71, 3.35) * mm, "end": v(45.7, 2.97) * mm});
            skLineSegment(sketch, "E1616", {"start": v(45.7, 2.97) * mm, "end": v(45.71, 2.76) * mm});
            skLineSegment(sketch, "E1617", {"start": v(45.71, 2.76) * mm, "end": v(45.73, 2.55) * mm});
            skLineSegment(sketch, "E1618", {"start": v(45.73, 2.55) * mm, "end": v(45.76, 2.35) * mm});
            skLineSegment(sketch, "E1619", {"start": v(45.76, 2.35) * mm, "end": v(45.8, 2.16) * mm});
            skLineSegment(sketch, "E1620", {"start": v(45.8, 2.16) * mm, "end": v(45.83, 2.07) * mm});
            skLineSegment(sketch, "E1621", {"start": v(45.83, 2.07) * mm, "end": v(45.86, 1.98) * mm});
            skLineSegment(sketch, "E1622", {"start": v(45.86, 1.98) * mm, "end": v(45.9, 1.9) * mm});
            skLineSegment(sketch, "E1623", {"start": v(45.9, 1.9) * mm, "end": v(45.93, 1.81) * mm});
            skLineSegment(sketch, "E1624", {"start": v(45.93, 1.81) * mm, "end": v(45.97, 1.73) * mm});
            skLineSegment(sketch, "E1625", {"start": v(45.97, 1.73) * mm, "end": v(46.02, 1.66) * mm});
            skLineSegment(sketch, "E1626", {"start": v(46.02, 1.66) * mm, "end": v(46.07, 1.58) * mm});
            skLineSegment(sketch, "E1627", {"start": v(46.07, 1.58) * mm, "end": v(46.12, 1.5) * mm});
            skLineSegment(sketch, "E1628", {"start": v(46.12, 1.5) * mm, "end": v(46.17, 1.44) * mm});
            skLineSegment(sketch, "E1629", {"start": v(46.17, 1.44) * mm, "end": v(46.24, 1.38) * mm});
            skLineSegment(sketch, "E1630", {"start": v(46.24, 1.38) * mm, "end": v(46.3, 1.31) * mm});
            skLineSegment(sketch, "E1631", {"start": v(46.3, 1.31) * mm, "end": v(46.37, 1.26) * mm});
            skLineSegment(sketch, "E1632", {"start": v(46.37, 1.26) * mm, "end": v(46.44, 1.2) * mm});
            skLineSegment(sketch, "E1633", {"start": v(46.44, 1.2) * mm, "end": v(46.52, 1.15) * mm});
            skLineSegment(sketch, "E1634", {"start": v(46.52, 1.15) * mm, "end": v(46.6, 1.1) * mm});
            skLineSegment(sketch, "E1635", {"start": v(46.6, 1.1) * mm, "end": v(46.7, 1.06) * mm});
            skLineSegment(sketch, "E1636", {"start": v(46.7, 1.06) * mm, "end": v(46.79, 1.03) * mm});
            skLineSegment(sketch, "E1637", {"start": v(46.79, 1.03) * mm, "end": v(46.89, 1) * mm});
            skLineSegment(sketch, "E1638", {"start": v(46.89, 1) * mm, "end": v(47, 0.96) * mm});
            skLineSegment(sketch, "E1639", {"start": v(47, 0.96) * mm, "end": v(47.1, 0.94) * mm});
            skLineSegment(sketch, "E1640", {"start": v(47.1, 0.94) * mm, "end": v(47.21, 0.92) * mm});
            skLineSegment(sketch, "E1641", {"start": v(47.21, 0.92) * mm, "end": v(47.33, 0.91) * mm});
            skLineSegment(sketch, "E1642", {"start": v(47.33, 0.91) * mm, "end": v(47.46, 0.9) * mm});
            skLineSegment(sketch, "E1643", {"start": v(47.46, 0.9) * mm, "end": v(47.58, 0.9) * mm});
            skLineSegment(sketch, "E1644", {"start": v(61.98, 7.43) * mm, "end": v(62.22, 7.43) * mm});
            skLineSegment(sketch, "E1645", {"start": v(62.22, 7.43) * mm, "end": v(62.46, 7.41) * mm});
            skLineSegment(sketch, "E1646", {"start": v(62.46, 7.41) * mm, "end": v(62.7, 7.39) * mm});
            skLineSegment(sketch, "E1647", {"start": v(62.7, 7.39) * mm, "end": v(62.92, 7.35) * mm});
            skLineSegment(sketch, "E1648", {"start": v(62.92, 7.35) * mm, "end": v(63.14, 7.3) * mm});
            skLineSegment(sketch, "E1649", {"start": v(63.14, 7.3) * mm, "end": v(63.36, 7.25) * mm});
            skLineSegment(sketch, "E1650", {"start": v(63.36, 7.25) * mm, "end": v(63.57, 7.19) * mm});
            skLineSegment(sketch, "E1651", {"start": v(63.57, 7.19) * mm, "end": v(63.77, 7.1) * mm});
            skLineSegment(sketch, "E1652", {"start": v(63.77, 7.1) * mm, "end": v(63.96, 7.03) * mm});
            skLineSegment(sketch, "E1653", {"start": v(63.96, 7.03) * mm, "end": v(64.15, 6.93) * mm});
            skLineSegment(sketch, "E1654", {"start": v(64.15, 6.93) * mm, "end": v(64.33, 6.83) * mm});
            skLineSegment(sketch, "E1655", {"start": v(64.33, 6.83) * mm, "end": v(64.5, 6.71) * mm});
            skLineSegment(sketch, "E1656", {"start": v(64.5, 6.71) * mm, "end": v(64.67, 6.59) * mm});
            skLineSegment(sketch, "E1657", {"start": v(64.67, 6.59) * mm, "end": v(64.82, 6.45) * mm});
            skLineSegment(sketch, "E1658", {"start": v(64.82, 6.45) * mm, "end": v(64.97, 6.3) * mm});
            skLineSegment(sketch, "E1659", {"start": v(64.97, 6.3) * mm, "end": v(65.11, 6.15) * mm});
            skLineSegment(sketch, "E1660", {"start": v(65.11, 6.15) * mm, "end": v(65.25, 6) * mm});
            skLineSegment(sketch, "E1661", {"start": v(65.25, 6) * mm, "end": v(65.37, 5.82) * mm});
            skLineSegment(sketch, "E1662", {"start": v(65.37, 5.82) * mm, "end": v(65.5, 5.64) * mm});
            skLineSegment(sketch, "E1663", {"start": v(65.5, 5.64) * mm, "end": v(65.6, 5.44) * mm});
            skLineSegment(sketch, "E1664", {"start": v(65.6, 5.44) * mm, "end": v(65.7, 5.24) * mm});
            skLineSegment(sketch, "E1665", {"start": v(65.7, 5.24) * mm, "end": v(65.8, 5.03) * mm});
            skLineSegment(sketch, "E1666", {"start": v(65.8, 5.03) * mm, "end": v(65.88, 4.8) * mm});
            skLineSegment(sketch, "E1667", {"start": v(65.88, 4.8) * mm, "end": v(65.96, 4.57) * mm});
            skLineSegment(sketch, "E1668", {"start": v(65.96, 4.57) * mm, "end": v(66.03, 4.33) * mm});
            skLineSegment(sketch, "E1669", {"start": v(66.03, 4.33) * mm, "end": v(66.09, 4.08) * mm});
            skLineSegment(sketch, "E1670", {"start": v(66.09, 4.08) * mm, "end": v(66.14, 3.82) * mm});
            skLineSegment(sketch, "E1671", {"start": v(66.14, 3.82) * mm, "end": v(66.18, 3.55) * mm});
            skLineSegment(sketch, "E1672", {"start": v(66.18, 3.55) * mm, "end": v(66.21, 3.27) * mm});
            skLineSegment(sketch, "E1673", {"start": v(66.21, 3.27) * mm, "end": v(66.24, 2.98) * mm});
            skLineSegment(sketch, "E1674", {"start": v(66.24, 2.98) * mm, "end": v(66.25, 2.38) * mm});
            skLineSegment(sketch, "E1675", {"start": v(66.25, 2.38) * mm, "end": v(66.24, 1.69) * mm});
            skLineSegment(sketch, "E1676", {"start": v(66.24, 1.69) * mm, "end": v(66.2, 1.02) * mm});
            skLineSegment(sketch, "E1677", {"start": v(66.2, 1.02) * mm, "end": v(66.13, 0.36) * mm});
            skLineSegment(sketch, "E1678", {"start": v(66.13, 0.36) * mm, "end": v(66.03, -0.28) * mm});
            skLineSegment(sketch, "E1679", {"start": v(66.03, -0.28) * mm, "end": v(65.9, -0.9) * mm});
            skLineSegment(sketch, "E1680", {"start": v(65.9, -0.9) * mm, "end": v(65.75, -1.5) * mm});
            skLineSegment(sketch, "E1681", {"start": v(65.75, -1.5) * mm, "end": v(65.57, -2.09) * mm});
            skLineSegment(sketch, "E1682", {"start": v(65.57, -2.09) * mm, "end": v(65.36, -2.65) * mm});
            skLineSegment(sketch, "E1683", {"start": v(65.36, -2.65) * mm, "end": v(65.14, -3.18) * mm});
            skLineSegment(sketch, "E1684", {"start": v(65.14, -3.18) * mm, "end": v(64.9, -3.7) * mm});
            skLineSegment(sketch, "E1685", {"start": v(64.9, -3.7) * mm, "end": v(64.63, -4.18) * mm});
            skLineSegment(sketch, "E1686", {"start": v(64.63, -4.18) * mm, "end": v(64.34, -4.65) * mm});
            skLineSegment(sketch, "E1687", {"start": v(64.34, -4.65) * mm, "end": v(64.04, -5.07) * mm});
            skLineSegment(sketch, "E1688", {"start": v(64.04, -5.07) * mm, "end": v(63.7, -5.47) * mm});
            skLineSegment(sketch, "E1689", {"start": v(63.7, -5.47) * mm, "end": v(63.36, -5.84) * mm});
            skLineSegment(sketch, "E1690", {"start": v(63.36, -5.84) * mm, "end": v(63, -6.18) * mm});
            skLineSegment(sketch, "E1691", {"start": v(63, -6.18) * mm, "end": v(62.62, -6.47) * mm});
            skLineSegment(sketch, "E1692", {"start": v(62.62, -6.47) * mm, "end": v(62.23, -6.73) * mm});
            skLineSegment(sketch, "E1693", {"start": v(62.23, -6.73) * mm, "end": v(61.82, -6.96) * mm});
            skLineSegment(sketch, "E1694", {"start": v(61.82, -6.96) * mm, "end": v(61.4, -7.15) * mm});
            skLineSegment(sketch, "E1695", {"start": v(61.4, -7.15) * mm, "end": v(61.18, -7.23) * mm});
            skLineSegment(sketch, "E1696", {"start": v(61.18, -7.23) * mm, "end": v(60.96, -7.3) * mm});
            skLineSegment(sketch, "E1697", {"start": v(60.96, -7.3) * mm, "end": v(60.73, -7.36) * mm});
            skLineSegment(sketch, "E1698", {"start": v(60.73, -7.36) * mm, "end": v(60.5, -7.41) * mm});
            skLineSegment(sketch, "E1699", {"start": v(60.5, -7.41) * mm, "end": v(60.28, -7.45) * mm});
            skLineSegment(sketch, "E1700", {"start": v(60.28, -7.45) * mm, "end": v(60.05, -7.48) * mm});
            skLineSegment(sketch, "E1701", {"start": v(60.05, -7.48) * mm, "end": v(59.82, -7.5) * mm});
            skLineSegment(sketch, "E1702", {"start": v(59.82, -7.5) * mm, "end": v(59.58, -7.5) * mm});
            skLineSegment(sketch, "E1703", {"start": v(59.58, -7.5) * mm, "end": v(59.08, -7.5) * mm});
            skLineSegment(sketch, "E1704", {"start": v(59.08, -7.5) * mm, "end": v(58.6, -7.46) * mm});
            skLineSegment(sketch, "E1705", {"start": v(58.6, -7.46) * mm, "end": v(58.15, -7.41) * mm});
            skLineSegment(sketch, "E1706", {"start": v(58.15, -7.41) * mm, "end": v(57.71, -7.35) * mm});
            skLineSegment(sketch, "E1707", {"start": v(57.71, -7.35) * mm, "end": v(57.3, -7.26) * mm});
            skLineSegment(sketch, "E1708", {"start": v(57.3, -7.26) * mm, "end": v(56.9, -7.16) * mm});
            skLineSegment(sketch, "E1709", {"start": v(56.9, -7.16) * mm, "end": v(56.51, -7.05) * mm});
            skLineSegment(sketch, "E1710", {"start": v(56.51, -7.05) * mm, "end": v(56.15, -6.91) * mm});
            skLineSegment(sketch, "E1711", {"start": v(56.15, -6.91) * mm, "end": v(56.57, -4.52) * mm});
            skLineSegment(sketch, "E1712", {"start": v(56.57, -4.52) * mm, "end": v(57.29, -4.52) * mm});
            skLineSegment(sketch, "E1713", {"start": v(57.29, -4.52) * mm, "end": v(57.4, -6.03) * mm});
            skLineSegment(sketch, "E1714", {"start": v(57.4, -6.03) * mm, "end": v(57.5, -6.09) * mm});
            skLineSegment(sketch, "E1715", {"start": v(57.5, -6.09) * mm, "end": v(57.6, -6.14) * mm});
            skLineSegment(sketch, "E1716", {"start": v(57.6, -6.14) * mm, "end": v(57.71, -6.2) * mm});
            skLineSegment(sketch, "E1717", {"start": v(57.71, -6.2) * mm, "end": v(57.83, -6.24) * mm});
            skLineSegment(sketch, "E1718", {"start": v(57.83, -6.24) * mm, "end": v(57.95, -6.29) * mm});
            skLineSegment(sketch, "E1719", {"start": v(57.95, -6.29) * mm, "end": v(58.07, -6.34) * mm});
            skLineSegment(sketch, "E1720", {"start": v(58.07, -6.34) * mm, "end": v(58.2, -6.38) * mm});
            skLineSegment(sketch, "E1721", {"start": v(58.2, -6.38) * mm, "end": v(58.34, -6.43) * mm});
            skLineSegment(sketch, "E1722", {"start": v(58.34, -6.43) * mm, "end": v(58.63, -6.5) * mm});
            skLineSegment(sketch, "E1723", {"start": v(58.63, -6.5) * mm, "end": v(58.93, -6.55) * mm});
            skLineSegment(sketch, "E1724", {"start": v(58.93, -6.55) * mm, "end": v(59.23, -6.58) * mm});
            skLineSegment(sketch, "E1725", {"start": v(59.23, -6.58) * mm, "end": v(59.54, -6.59) * mm});
            skLineSegment(sketch, "E1726", {"start": v(59.54, -6.59) * mm, "end": v(59.77, -6.58) * mm});
            skLineSegment(sketch, "E1727", {"start": v(59.77, -6.58) * mm, "end": v(60, -6.56) * mm});
            skLineSegment(sketch, "E1728", {"start": v(60, -6.56) * mm, "end": v(60.22, -6.52) * mm});
            skLineSegment(sketch, "E1729", {"start": v(60.22, -6.52) * mm, "end": v(60.44, -6.47) * mm});
            skLineSegment(sketch, "E1730", {"start": v(60.44, -6.47) * mm, "end": v(60.65, -6.4) * mm});
            skLineSegment(sketch, "E1731", {"start": v(60.65, -6.4) * mm, "end": v(60.86, -6.32) * mm});
            skLineSegment(sketch, "E1732", {"start": v(60.86, -6.32) * mm, "end": v(61.06, -6.22) * mm});
            skLineSegment(sketch, "E1733", {"start": v(61.06, -6.22) * mm, "end": v(61.25, -6.11) * mm});
            skLineSegment(sketch, "E1734", {"start": v(61.25, -6.11) * mm, "end": v(61.44, -5.98) * mm});
            skLineSegment(sketch, "E1735", {"start": v(61.44, -5.98) * mm, "end": v(61.62, -5.84) * mm});
            skLineSegment(sketch, "E1736", {"start": v(61.62, -5.84) * mm, "end": v(61.8, -5.7) * mm});
            skLineSegment(sketch, "E1737", {"start": v(61.8, -5.7) * mm, "end": v(61.96, -5.54) * mm});
            skLineSegment(sketch, "E1738", {"start": v(61.96, -5.54) * mm, "end": v(62.12, -5.36) * mm});
            skLineSegment(sketch, "E1739", {"start": v(62.12, -5.36) * mm, "end": v(62.27, -5.18) * mm});
            skLineSegment(sketch, "E1740", {"start": v(62.27, -5.18) * mm, "end": v(62.42, -5) * mm});
            skLineSegment(sketch, "E1741", {"start": v(62.42, -5) * mm, "end": v(62.56, -4.79) * mm});
            skLineSegment(sketch, "E1742", {"start": v(62.56, -4.79) * mm, "end": v(62.83, -4.35) * mm});
            skLineSegment(sketch, "E1743", {"start": v(62.83, -4.35) * mm, "end": v(63.08, -3.87) * mm});
            skLineSegment(sketch, "E1744", {"start": v(63.08, -3.87) * mm, "end": v(63.3, -3.36) * mm});
            skLineSegment(sketch, "E1745", {"start": v(63.3, -3.36) * mm, "end": v(63.5, -2.82) * mm});
            skLineSegment(sketch, "E1746", {"start": v(63.5, -2.82) * mm, "end": v(63.69, -2.25) * mm});
            skLineSegment(sketch, "E1747", {"start": v(63.69, -2.25) * mm, "end": v(63.84, -1.67) * mm});
            skLineSegment(sketch, "E1748", {"start": v(63.84, -1.67) * mm, "end": v(63.97, -1.06) * mm});
            skLineSegment(sketch, "E1749", {"start": v(63.97, -1.06) * mm, "end": v(64.08, -0.43) * mm});
            skLineSegment(sketch, "E1750", {"start": v(64.08, -0.43) * mm, "end": v(63.92, -0.53) * mm});
            skLineSegment(sketch, "E1751", {"start": v(63.92, -0.53) * mm, "end": v(63.75, -0.62) * mm});
            skLineSegment(sketch, "E1752", {"start": v(63.75, -0.62) * mm, "end": v(63.56, -0.72) * mm});
            skLineSegment(sketch, "E1753", {"start": v(63.56, -0.72) * mm, "end": v(63.37, -0.81) * mm});
            skLineSegment(sketch, "E1754", {"start": v(63.37, -0.81) * mm, "end": v(63.17, -0.9) * mm});
            skLineSegment(sketch, "E1755", {"start": v(63.17, -0.9) * mm, "end": v(62.74, -1.07) * mm});
            skLineSegment(sketch, "E1756", {"start": v(62.74, -1.07) * mm, "end": v(62.52, -1.15) * mm});
            skLineSegment(sketch, "E1757", {"start": v(62.52, -1.15) * mm, "end": v(62.29, -1.22) * mm});
            skLineSegment(sketch, "E1758", {"start": v(62.29, -1.22) * mm, "end": v(61.82, -1.35) * mm});
            skLineSegment(sketch, "E1759", {"start": v(61.82, -1.35) * mm, "end": v(61.58, -1.4) * mm});
            skLineSegment(sketch, "E1760", {"start": v(61.58, -1.4) * mm, "end": v(61.33, -1.44) * mm});
            skLineSegment(sketch, "E1761", {"start": v(61.33, -1.44) * mm, "end": v(61.09, -1.47) * mm});
            skLineSegment(sketch, "E1762", {"start": v(61.09, -1.47) * mm, "end": v(60.84, -1.5) * mm});
            skLineSegment(sketch, "E1763", {"start": v(60.84, -1.5) * mm, "end": v(60.6, -1.5) * mm});
            skLineSegment(sketch, "E1764", {"start": v(60.6, -1.5) * mm, "end": v(60.38, -1.5) * mm});
            skLineSegment(sketch, "E1765", {"start": v(60.38, -1.5) * mm, "end": v(60.17, -1.48) * mm});
            skLineSegment(sketch, "E1766", {"start": v(60.17, -1.48) * mm, "end": v(59.96, -1.46) * mm});
            skLineSegment(sketch, "E1767", {"start": v(59.96, -1.46) * mm, "end": v(59.76, -1.43) * mm});
            skLineSegment(sketch, "E1768", {"start": v(59.76, -1.43) * mm, "end": v(59.56, -1.4) * mm});
            skLineSegment(sketch, "E1769", {"start": v(59.56, -1.4) * mm, "end": v(59.37, -1.35) * mm});
            skLineSegment(sketch, "E1770", {"start": v(59.37, -1.35) * mm, "end": v(59.2, -1.3) * mm});
            skLineSegment(sketch, "E1771", {"start": v(59.2, -1.3) * mm, "end": v(59.01, -1.24) * mm});
            skLineSegment(sketch, "E1772", {"start": v(59.01, -1.24) * mm, "end": v(58.84, -1.17) * mm});
            skLineSegment(sketch, "E1773", {"start": v(58.84, -1.17) * mm, "end": v(58.68, -1.1) * mm});
            skLineSegment(sketch, "E1774", {"start": v(58.68, -1.1) * mm, "end": v(58.52, -1.01) * mm});
            skLineSegment(sketch, "E1775", {"start": v(58.52, -1.01) * mm, "end": v(58.37, -0.92) * mm});
            skLineSegment(sketch, "E1776", {"start": v(58.37, -0.92) * mm, "end": v(58.23, -0.83) * mm});
            skLineSegment(sketch, "E1777", {"start": v(58.23, -0.83) * mm, "end": v(58.1, -0.72) * mm});
            skLineSegment(sketch, "E1778", {"start": v(58.1, -0.72) * mm, "end": v(57.96, -0.62) * mm});
            skLineSegment(sketch, "E1779", {"start": v(57.96, -0.62) * mm, "end": v(57.84, -0.5) * mm});
            skLineSegment(sketch, "E1780", {"start": v(57.84, -0.5) * mm, "end": v(57.73, -0.38) * mm});
            skLineSegment(sketch, "E1781", {"start": v(57.73, -0.38) * mm, "end": v(57.62, -0.25) * mm});
            skLineSegment(sketch, "E1782", {"start": v(57.62, -0.25) * mm, "end": v(57.52, -0.11) * mm});
            skLineSegment(sketch, "E1783", {"start": v(57.52, -0.11) * mm, "end": v(57.42, 0.03) * mm});
            skLineSegment(sketch, "E1784", {"start": v(57.42, 0.03) * mm, "end": v(57.33, 0.17) * mm});
            skLineSegment(sketch, "E1785", {"start": v(57.33, 0.17) * mm, "end": v(57.25, 0.33) * mm});
            skLineSegment(sketch, "E1786", {"start": v(57.25, 0.33) * mm, "end": v(57.18, 0.49) * mm});
            skLineSegment(sketch, "E1787", {"start": v(57.18, 0.49) * mm, "end": v(57.11, 0.65) * mm});
            skLineSegment(sketch, "E1788", {"start": v(57.11, 0.65) * mm, "end": v(57.06, 0.82) * mm});
            skLineSegment(sketch, "E1789", {"start": v(57.06, 0.82) * mm, "end": v(57, 1) * mm});
            skLineSegment(sketch, "E1790", {"start": v(57, 1) * mm, "end": v(56.96, 1.19) * mm});
            skLineSegment(sketch, "E1791", {"start": v(56.96, 1.19) * mm, "end": v(56.93, 1.37) * mm});
            skLineSegment(sketch, "E1792", {"start": v(56.93, 1.37) * mm, "end": v(56.9, 1.57) * mm});
            skLineSegment(sketch, "E1793", {"start": v(56.9, 1.57) * mm, "end": v(56.88, 1.76) * mm});
            skLineSegment(sketch, "E1794", {"start": v(56.88, 1.76) * mm, "end": v(56.87, 1.96) * mm});
            skLineSegment(sketch, "E1795", {"start": v(56.87, 1.96) * mm, "end": v(56.87, 2.17) * mm});
            skLineSegment(sketch, "E1796", {"start": v(56.87, 2.17) * mm, "end": v(56.89, 2.72) * mm});
            skLineSegment(sketch, "E1797", {"start": v(56.89, 2.72) * mm, "end": v(56.95, 3.25) * mm});
            skLineSegment(sketch, "E1798", {"start": v(56.95, 3.25) * mm, "end": v(57.05, 3.76) * mm});
            skLineSegment(sketch, "E1799", {"start": v(57.05, 3.76) * mm, "end": v(57.11, 4.01) * mm});
            skLineSegment(sketch, "E1800", {"start": v(57.11, 4.01) * mm, "end": v(57.2, 4.25) * mm});
            skLineSegment(sketch, "E1801", {"start": v(57.2, 4.25) * mm, "end": v(57.28, 4.5) * mm});
            skLineSegment(sketch, "E1802", {"start": v(57.28, 4.5) * mm, "end": v(57.37, 4.72) * mm});
            skLineSegment(sketch, "E1803", {"start": v(57.37, 4.72) * mm, "end": v(57.48, 4.94) * mm});
            skLineSegment(sketch, "E1804", {"start": v(57.48, 4.94) * mm, "end": v(57.6, 5.16) * mm});
            skLineSegment(sketch, "E1805", {"start": v(57.6, 5.16) * mm, "end": v(57.72, 5.36) * mm});
            skLineSegment(sketch, "E1806", {"start": v(57.72, 5.36) * mm, "end": v(57.86, 5.56) * mm});
            skLineSegment(sketch, "E1807", {"start": v(57.86, 5.56) * mm, "end": v(58, 5.75) * mm});
            skLineSegment(sketch, "E1808", {"start": v(58, 5.75) * mm, "end": v(58.16, 5.93) * mm});
            skLineSegment(sketch, "E1809", {"start": v(58.16, 5.93) * mm, "end": v(58.32, 6.1) * mm});
            skLineSegment(sketch, "E1810", {"start": v(58.32, 6.1) * mm, "end": v(58.5, 6.26) * mm});
            skLineSegment(sketch, "E1811", {"start": v(58.5, 6.26) * mm, "end": v(58.68, 6.41) * mm});
            skLineSegment(sketch, "E1812", {"start": v(58.68, 6.41) * mm, "end": v(58.88, 6.56) * mm});
            skLineSegment(sketch, "E1813", {"start": v(58.88, 6.56) * mm, "end": v(59.08, 6.69) * mm});
            skLineSegment(sketch, "E1814", {"start": v(59.08, 6.69) * mm, "end": v(59.3, 6.81) * mm});
            skLineSegment(sketch, "E1815", {"start": v(59.3, 6.81) * mm, "end": v(59.52, 6.93) * mm});
            skLineSegment(sketch, "E1816", {"start": v(59.52, 6.93) * mm, "end": v(59.75, 7.03) * mm});
            skLineSegment(sketch, "E1817", {"start": v(59.75, 7.03) * mm, "end": v(60, 7.13) * mm});
            skLineSegment(sketch, "E1818", {"start": v(60, 7.13) * mm, "end": v(60.25, 7.2) * mm});
            skLineSegment(sketch, "E1819", {"start": v(60.25, 7.2) * mm, "end": v(60.52, 7.28) * mm});
            skLineSegment(sketch, "E1820", {"start": v(60.52, 7.28) * mm, "end": v(60.8, 7.33) * mm});
            skLineSegment(sketch, "E1821", {"start": v(60.8, 7.33) * mm, "end": v(61.07, 7.38) * mm});
            skLineSegment(sketch, "E1822", {"start": v(61.07, 7.38) * mm, "end": v(61.37, 7.4) * mm});
            skLineSegment(sketch, "E1823", {"start": v(61.37, 7.4) * mm, "end": v(61.67, 7.43) * mm});
            skLineSegment(sketch, "E1824", {"start": v(61.67, 7.43) * mm, "end": v(61.98, 7.43) * mm});
            skLineSegment(sketch, "E1825", {"start": v(64.33, 2.76) * mm, "end": v(64.33, 3) * mm});
            skLineSegment(sketch, "E1826", {"start": v(64.33, 3) * mm, "end": v(64.32, 3.25) * mm});
            skLineSegment(sketch, "E1827", {"start": v(64.32, 3.25) * mm, "end": v(64.3, 3.49) * mm});
            skLineSegment(sketch, "E1828", {"start": v(64.3, 3.49) * mm, "end": v(64.29, 3.71) * mm});
            skLineSegment(sketch, "E1829", {"start": v(64.29, 3.71) * mm, "end": v(64.26, 3.93) * mm});
            skLineSegment(sketch, "E1830", {"start": v(64.26, 3.93) * mm, "end": v(64.23, 4.13) * mm});
            skLineSegment(sketch, "E1831", {"start": v(64.23, 4.13) * mm, "end": v(64.2, 4.33) * mm});
            skLineSegment(sketch, "E1832", {"start": v(64.2, 4.33) * mm, "end": v(64.15, 4.52) * mm});
            skLineSegment(sketch, "E1833", {"start": v(64.15, 4.52) * mm, "end": v(64.1, 4.7) * mm});
            skLineSegment(sketch, "E1834", {"start": v(64.1, 4.7) * mm, "end": v(64.05, 4.86) * mm});
            skLineSegment(sketch, "E1835", {"start": v(64.05, 4.86) * mm, "end": v(64, 5.02) * mm});
            skLineSegment(sketch, "E1836", {"start": v(64, 5.02) * mm, "end": v(63.93, 5.17) * mm});
            skLineSegment(sketch, "E1837", {"start": v(63.93, 5.17) * mm, "end": v(63.87, 5.32) * mm});
            skLineSegment(sketch, "E1838", {"start": v(63.87, 5.32) * mm, "end": v(63.8, 5.45) * mm});
            skLineSegment(sketch, "E1839", {"start": v(63.8, 5.45) * mm, "end": v(63.73, 5.58) * mm});
            skLineSegment(sketch, "E1840", {"start": v(63.73, 5.58) * mm, "end": v(63.65, 5.7) * mm});
            skLineSegment(sketch, "E1841", {"start": v(63.65, 5.7) * mm, "end": v(63.57, 5.8) * mm});
            skLineSegment(sketch, "E1842", {"start": v(63.57, 5.8) * mm, "end": v(63.48, 5.91) * mm});
            skLineSegment(sketch, "E1843", {"start": v(63.48, 5.91) * mm, "end": v(63.4, 6) * mm});
            skLineSegment(sketch, "E1844", {"start": v(63.4, 6) * mm, "end": v(63.3, 6.1) * mm});
            skLineSegment(sketch, "E1845", {"start": v(63.3, 6.1) * mm, "end": v(63.2, 6.17) * mm});
            skLineSegment(sketch, "E1846", {"start": v(63.2, 6.17) * mm, "end": v(63.1, 6.24) * mm});
            skLineSegment(sketch, "E1847", {"start": v(63.1, 6.24) * mm, "end": v(63, 6.3) * mm});
            skLineSegment(sketch, "E1848", {"start": v(63, 6.3) * mm, "end": v(62.89, 6.36) * mm});
            skLineSegment(sketch, "E1849", {"start": v(62.89, 6.36) * mm, "end": v(62.78, 6.41) * mm});
            skLineSegment(sketch, "E1850", {"start": v(62.78, 6.41) * mm, "end": v(62.67, 6.46) * mm});
            skLineSegment(sketch, "E1851", {"start": v(62.67, 6.46) * mm, "end": v(62.55, 6.5) * mm});
            skLineSegment(sketch, "E1852", {"start": v(62.55, 6.5) * mm, "end": v(62.44, 6.52) * mm});
            skLineSegment(sketch, "E1853", {"start": v(62.44, 6.52) * mm, "end": v(62.32, 6.55) * mm});
            skLineSegment(sketch, "E1854", {"start": v(62.32, 6.55) * mm, "end": v(62.2, 6.56) * mm});
            skLineSegment(sketch, "E1855", {"start": v(62.2, 6.56) * mm, "end": v(62.08, 6.57) * mm});
            skLineSegment(sketch, "E1856", {"start": v(62.08, 6.57) * mm, "end": v(61.96, 6.58) * mm});
            skLineSegment(sketch, "E1857", {"start": v(61.96, 6.58) * mm, "end": v(61.76, 6.57) * mm});
            skLineSegment(sketch, "E1858", {"start": v(61.76, 6.57) * mm, "end": v(61.57, 6.56) * mm});
            skLineSegment(sketch, "E1859", {"start": v(61.57, 6.56) * mm, "end": v(61.38, 6.53) * mm});
            skLineSegment(sketch, "E1860", {"start": v(61.38, 6.53) * mm, "end": v(61.2, 6.5) * mm});
            skLineSegment(sketch, "E1861", {"start": v(61.2, 6.5) * mm, "end": v(61.04, 6.45) * mm});
            skLineSegment(sketch, "E1862", {"start": v(61.04, 6.45) * mm, "end": v(60.87, 6.39) * mm});
            skLineSegment(sketch, "E1863", {"start": v(60.87, 6.39) * mm, "end": v(60.72, 6.32) * mm});
            skLineSegment(sketch, "E1864", {"start": v(60.72, 6.32) * mm, "end": v(60.57, 6.24) * mm});
            skLineSegment(sketch, "E1865", {"start": v(60.57, 6.24) * mm, "end": v(60.43, 6.16) * mm});
            skLineSegment(sketch, "E1866", {"start": v(60.43, 6.16) * mm, "end": v(60.3, 6.06) * mm});
            skLineSegment(sketch, "E1867", {"start": v(60.3, 6.06) * mm, "end": v(60.16, 5.96) * mm});
            skLineSegment(sketch, "E1868", {"start": v(60.16, 5.96) * mm, "end": v(60.04, 5.85) * mm});
            skLineSegment(sketch, "E1869", {"start": v(60.04, 5.85) * mm, "end": v(59.92, 5.73) * mm});
            skLineSegment(sketch, "E1870", {"start": v(59.92, 5.73) * mm, "end": v(59.81, 5.6) * mm});
            skLineSegment(sketch, "E1871", {"start": v(59.81, 5.6) * mm, "end": v(59.7, 5.47) * mm});
            skLineSegment(sketch, "E1872", {"start": v(59.7, 5.47) * mm, "end": v(59.61, 5.33) * mm});
            skLineSegment(sketch, "E1873", {"start": v(59.61, 5.33) * mm, "end": v(59.52, 5.18) * mm});
            skLineSegment(sketch, "E1874", {"start": v(59.52, 5.18) * mm, "end": v(59.44, 5.02) * mm});
            skLineSegment(sketch, "E1875", {"start": v(59.44, 5.02) * mm, "end": v(59.36, 4.86) * mm});
            skLineSegment(sketch, "E1876", {"start": v(59.36, 4.86) * mm, "end": v(59.29, 4.69) * mm});
            skLineSegment(sketch, "E1877", {"start": v(59.29, 4.69) * mm, "end": v(59.22, 4.51) * mm});
            skLineSegment(sketch, "E1878", {"start": v(59.22, 4.51) * mm, "end": v(59.16, 4.33) * mm});
            skLineSegment(sketch, "E1879", {"start": v(59.16, 4.33) * mm, "end": v(59.1, 4.14) * mm});
            skLineSegment(sketch, "E1880", {"start": v(59.1, 4.14) * mm, "end": v(59.06, 3.94) * mm});
            skLineSegment(sketch, "E1881", {"start": v(59.06, 3.94) * mm, "end": v(58.98, 3.54) * mm});
            skLineSegment(sketch, "E1882", {"start": v(58.98, 3.54) * mm, "end": v(58.93, 3.12) * mm});
            skLineSegment(sketch, "E1883", {"start": v(58.93, 3.12) * mm, "end": v(58.9, 2.68) * mm});
            skLineSegment(sketch, "E1884", {"start": v(58.9, 2.68) * mm, "end": v(58.88, 2.23) * mm});
            skLineSegment(sketch, "E1885", {"start": v(58.88, 2.23) * mm, "end": v(58.89, 2.06) * mm});
            skLineSegment(sketch, "E1886", {"start": v(58.89, 2.06) * mm, "end": v(58.9, 1.9) * mm});
            skLineSegment(sketch, "E1887", {"start": v(58.9, 1.9) * mm, "end": v(58.9, 1.74) * mm});
            skLineSegment(sketch, "E1888", {"start": v(58.9, 1.74) * mm, "end": v(58.92, 1.59) * mm});
            skLineSegment(sketch, "E1889", {"start": v(58.92, 1.59) * mm, "end": v(58.94, 1.44) * mm});
            skLineSegment(sketch, "E1890", {"start": v(58.94, 1.44) * mm, "end": v(58.97, 1.3) * mm});
            skLineSegment(sketch, "E1891", {"start": v(58.97, 1.3) * mm, "end": v(59, 1.16) * mm});
            skLineSegment(sketch, "E1892", {"start": v(59, 1.16) * mm, "end": v(59.03, 1.03) * mm});
            skLineSegment(sketch, "E1893", {"start": v(59.03, 1.03) * mm, "end": v(59.07, 0.9) * mm});
            skLineSegment(sketch, "E1894", {"start": v(59.07, 0.9) * mm, "end": v(59.12, 0.8) * mm});
            skLineSegment(sketch, "E1895", {"start": v(59.12, 0.8) * mm, "end": v(59.17, 0.68) * mm});
            skLineSegment(sketch, "E1896", {"start": v(59.17, 0.68) * mm, "end": v(59.22, 0.57) * mm});
            skLineSegment(sketch, "E1897", {"start": v(59.22, 0.57) * mm, "end": v(59.28, 0.47) * mm});
            skLineSegment(sketch, "E1898", {"start": v(59.28, 0.47) * mm, "end": v(59.34, 0.37) * mm});
            skLineSegment(sketch, "E1899", {"start": v(59.34, 0.37) * mm, "end": v(59.4, 0.28) * mm});
            skLineSegment(sketch, "E1900", {"start": v(59.4, 0.28) * mm, "end": v(59.48, 0.2) * mm});
            skLineSegment(sketch, "E1901", {"start": v(59.48, 0.2) * mm, "end": v(59.56, 0.12) * mm});
            skLineSegment(sketch, "E1902", {"start": v(59.56, 0.12) * mm, "end": v(59.64, 0.04) * mm});
            skLineSegment(sketch, "E1903", {"start": v(59.64, 0.04) * mm, "end": v(59.72, -0.03) * mm});
            skLineSegment(sketch, "E1904", {"start": v(59.72, -0.03) * mm, "end": v(59.81, -0.09) * mm});
            skLineSegment(sketch, "E1905", {"start": v(59.81, -0.09) * mm, "end": v(59.9, -0.15) * mm});
            skLineSegment(sketch, "E1906", {"start": v(59.9, -0.15) * mm, "end": v(60, -0.2) * mm});
            skLineSegment(sketch, "E1907", {"start": v(60, -0.2) * mm, "end": v(60.1, -0.25) * mm});
            skLineSegment(sketch, "E1908", {"start": v(60.1, -0.25) * mm, "end": v(60.2, -0.3) * mm});
            skLineSegment(sketch, "E1909", {"start": v(60.2, -0.3) * mm, "end": v(60.3, -0.33) * mm});
            skLineSegment(sketch, "E1910", {"start": v(60.3, -0.33) * mm, "end": v(60.42, -0.36) * mm});
            skLineSegment(sketch, "E1911", {"start": v(60.42, -0.36) * mm, "end": v(60.53, -0.4) * mm});
            skLineSegment(sketch, "E1912", {"start": v(60.53, -0.4) * mm, "end": v(60.65, -0.42) * mm});
            skLineSegment(sketch, "E1913", {"start": v(60.65, -0.42) * mm, "end": v(60.77, -0.43) * mm});
            skLineSegment(sketch, "E1914", {"start": v(60.77, -0.43) * mm, "end": v(60.9, -0.45) * mm});
            skLineSegment(sketch, "E1915", {"start": v(60.9, -0.45) * mm, "end": v(61.02, -0.45) * mm});
            skLineSegment(sketch, "E1916", {"start": v(61.02, -0.45) * mm, "end": v(61.15, -0.46) * mm});
            skLineSegment(sketch, "E1917", {"start": v(61.15, -0.46) * mm, "end": v(61.57, -0.44) * mm});
            skLineSegment(sketch, "E1918", {"start": v(61.57, -0.44) * mm, "end": v(61.97, -0.4) * mm});
            skLineSegment(sketch, "E1919", {"start": v(61.97, -0.4) * mm, "end": v(62.37, -0.35) * mm});
            skLineSegment(sketch, "E1920", {"start": v(62.37, -0.35) * mm, "end": v(62.75, -0.27) * mm});
            skLineSegment(sketch, "E1921", {"start": v(62.75, -0.27) * mm, "end": v(63.12, -0.17) * mm});
            skLineSegment(sketch, "E1922", {"start": v(63.12, -0.17) * mm, "end": v(63.83, 0.07) * mm});
            skLineSegment(sketch, "E1923", {"start": v(63.83, 0.07) * mm, "end": v(64.18, 0.2) * mm});
            skLineSegment(sketch, "E1924", {"start": v(64.18, 0.2) * mm, "end": v(64.22, 0.52) * mm});
            skLineSegment(sketch, "E1925", {"start": v(64.22, 0.52) * mm, "end": v(64.27, 1.15) * mm});
            skLineSegment(sketch, "E1926", {"start": v(64.27, 1.15) * mm, "end": v(64.29, 1.47) * mm});
            skLineSegment(sketch, "E1927", {"start": v(64.29, 1.47) * mm, "end": v(64.3, 1.79) * mm});
            skLineSegment(sketch, "E1928", {"start": v(64.3, 1.79) * mm, "end": v(64.33, 2.43) * mm});
            skLineSegment(sketch, "E1929", {"start": v(64.33, 2.43) * mm, "end": v(64.33, 2.76) * mm});
            skPoint(sketch, "E1930.middle", {"position": v(0.98, 0.05) * mm});
            skLineSegment(sketch, "E1931.bottom", {"start": v(73.45, -10.33) * mm, "end": v(-73.45, -10.33) * mm});
            skLineSegment(sketch, "E1931.top", {"start": v(73.45, 10.33) * mm, "end": v(-73.45, 10.33) * mm});
            skLineSegment(sketch, "E1931.left", {"start": v(78.45, -5.33) * mm, "end": v(78.45, 5.33) * mm});
            skLineSegment(sketch, "E1931.right", {"start": v(-78.45, -5.33) * mm, "end": v(-78.45, 5.33) * mm});
            skPoint(sketch, "E1931.middle", {"position": v(0, 0) * mm});
            skPoint(sketch, "E1932.visualSharp", {"position": v(-78.45, 10.33) * mm});
            skArc(sketch, "E1932.filletArc", {"start": v(-73.45, 10.33) * mm, "mid": v(-76.98, 8.87) * mm, "end": v(-78.45, 5.33) * mm});
            skPoint(sketch, "E1933.visualSharp", {"position": v(-78.45, -10.33) * mm});
            skArc(sketch, "E1933.filletArc", {"start": v(-78.45, -5.33) * mm, "mid": v(-76.98, -8.87) * mm, "end": v(-73.45, -10.33) * mm});
            skPoint(sketch, "E1934.visualSharp", {"position": v(78.45, -10.33) * mm});
            skArc(sketch, "E1934.filletArc", {"start": v(73.45, -10.33) * mm, "mid": v(76.98, -8.87) * mm, "end": v(78.45, -5.33) * mm});
            skPoint(sketch, "E1935.visualSharp", {"position": v(78.45, 10.33) * mm});
            skArc(sketch, "E1935.filletArc", {"start": v(78.45, 5.33) * mm, "mid": v(76.98, 8.87) * mm, "end": v(73.45, 10.33) * mm});
            skArc(sketch, "E1936.0", {"start": v(80.65, 5.33) * mm, "mid": v(78.54, 10.42) * mm, "end": v(73.45, 12.53) * mm});
            skLineSegment(sketch, "E1936.1", {"start": v(80.65, -5.33) * mm, "end": v(80.65, 5.33) * mm});
            skLineSegment(sketch, "E1936.2", {"start": v(73.45, 12.53) * mm, "end": v(-73.45, 12.53) * mm});
            skArc(sketch, "E1936.3", {"start": v(73.45, -12.53) * mm, "mid": v(78.54, -10.42) * mm, "end": v(80.65, -5.33) * mm});
            skArc(sketch, "E1936.4", {"start": v(-73.45, 12.53) * mm, "mid": v(-78.54, 10.42) * mm, "end": v(-80.65, 5.33) * mm});
            skLineSegment(sketch, "E1936.5", {"start": v(-80.65, -5.33) * mm, "end": v(-80.65, 5.33) * mm});
            skArc(sketch, "E1936.6", {"start": v(-80.65, -5.33) * mm, "mid": v(-78.54, -10.42) * mm, "end": v(-73.45, -12.53) * mm});
            skLineSegment(sketch, "E1936.7", {"start": v(73.45, -12.53) * mm, "end": v(-73.45, -12.53) * mm});
            skSolve(sketch);
        }
        {
            var Q0;
            Q0=makeQuery(id+"F0.imprint","IMPRINT",FACE,{"disambiguationData":[TD([[makeQuery(id+"F0.imprint","IMPRINT",EDGE,{"derivedFrom":sQuery(id+"F0.wireOp",EDGE,"E1931.bottom")}),1.0]])]});
            var Q1;
            Q1=makeQuery(id+"F0.imprint","IMPRINT",FACE,{"disambiguationData":[TD([[makeQuery(id+"F0.imprint","IMPRINT",EDGE,{"derivedFrom":sQuery(id+"F0.wireOp",EDGE,"E3")}),-1.0]])]});
            var Q2;
            Q2=makeQuery(id+"F0.imprint","IMPRINT",FACE,{"disambiguationData":[TD([[makeQuery(id+"F0.imprint","IMPRINT",EDGE,{"derivedFrom":sQuery(id+"F0.wireOp",EDGE,"E134")}),1.0]])]});
            var Q3;
            Q3=makeQuery(id+"F0.imprint","IMPRINT",FACE,{"disambiguationData":[TD([[makeQuery(id+"F0.imprint","IMPRINT",EDGE,{"derivedFrom":sQuery(id+"F0.wireOp",EDGE,"E264")}),-1.0]])]});
            var Q4;
            Q4=makeQuery(id+"F0.imprint","IMPRINT",FACE,{"disambiguationData":[TD([[makeQuery(id+"F0.imprint","IMPRINT",EDGE,{"derivedFrom":sQuery(id+"F0.wireOp",EDGE,"E275")}),-1.0]])]});
            var Q5;
            Q5=makeQuery(id+"F0.imprint","IMPRINT",FACE,{"disambiguationData":[TD([[makeQuery(id+"F0.imprint","IMPRINT",EDGE,{"derivedFrom":sQuery(id+"F0.wireOp",EDGE,"E411")}),-1.0]])]});
            var Q6;
            Q6=makeQuery(id+"F0.imprint","IMPRINT",FACE,{"disambiguationData":[TD([[makeQuery(id+"F0.imprint","IMPRINT",EDGE,{"derivedFrom":sQuery(id+"F0.wireOp",EDGE,"E727")}),1.0]])]});
            var Q7;
            Q7=makeQuery(id+"F0.imprint","IMPRINT",FACE,{"disambiguationData":[TD([[makeQuery(id+"F0.imprint","IMPRINT",EDGE,{"derivedFrom":sQuery(id+"F0.wireOp",EDGE,"E716")}),-1.0]])]});
            var Q8;
            Q8=makeQuery(id+"F0.imprint","IMPRINT",FACE,{"disambiguationData":[TD([[makeQuery(id+"F0.imprint","IMPRINT",EDGE,{"derivedFrom":sQuery(id+"F0.wireOp",EDGE,"E740")}),-1.0]])]});
            var Q9;
            Q9=makeQuery(id+"F0.imprint","IMPRINT",FACE,{"disambiguationData":[TD([[makeQuery(id+"F0.imprint","IMPRINT",EDGE,{"derivedFrom":sQuery(id+"F0.wireOp",EDGE,"E919")}),-1.0]])]});
            var Q10;
            Q10=makeQuery(id+"F0.imprint","IMPRINT",FACE,{"disambiguationData":[TD([[makeQuery(id+"F0.imprint","IMPRINT",EDGE,{"derivedFrom":sQuery(id+"F0.wireOp",EDGE,"E1098")}),1.0]])]});
            var Q11;
            Q11=makeQuery(id+"F0.imprint","IMPRINT",FACE,{"disambiguationData":[TD([[makeQuery(id+"F0.imprint","IMPRINT",EDGE,{"derivedFrom":sQuery(id+"F0.wireOp",EDGE,"E1206")}),-1.0]])]});
            var Q12;
            Q12=makeQuery(id+"F0.imprint","IMPRINT",FACE,{"disambiguationData":[TD([[makeQuery(id+"F0.imprint","IMPRINT",EDGE,{"derivedFrom":sQuery(id+"F0.wireOp",EDGE,"E1531")}),1.0]])]});
            var Q13;
            Q13=makeQuery(id+"F0.imprint","IMPRINT",FACE,{"disambiguationData":[TD([[makeQuery(id+"F0.imprint","IMPRINT",EDGE,{"derivedFrom":sQuery(id+"F0.wireOp",EDGE,"E1419")}),1.0]])]});
            var Q14;
            Q14=makeQuery(id+"F0.imprint","IMPRINT",FACE,{"disambiguationData":[TD([[makeQuery(id+"F0.imprint","IMPRINT",EDGE,{"derivedFrom":sQuery(id+"F0.wireOp",EDGE,"E1215")}),-1.0]])]});
            var Q15;
            Q15=makeQuery(id+"F0.imprint","IMPRINT",FACE,{"disambiguationData":[TD([[makeQuery(id+"F0.imprint","IMPRINT",EDGE,{"derivedFrom":sQuery(id+"F0.wireOp",EDGE,"E1644")}),-1.0]])]});
            var Q16;
            Q16=makeQuery(id+"F0.imprint","IMPRINT",FACE,{"disambiguationData":[TD([[makeQuery(id+"F0.imprint","IMPRINT",EDGE,{"derivedFrom":sQuery(id+"F0.wireOp",EDGE,"E1")}),-1.0]])]});
            var Q17;
            Q17=makeQuery(id+"F0.imprint","IMPRINT",FACE,{"disambiguationData":[TD([[makeQuery(id+"F0.imprint","IMPRINT",EDGE,{"derivedFrom":sQuery(id+"F0.wireOp",EDGE,"E1825")}),1.0]])]});
            extrude(context, id + "F1", {"entities" : qUnion([Q0, Q1, Q2, Q3, Q4, Q5, Q6, Q7, Q8, Q9, Q10, Q11, Q12, Q13, Q14, Q15, Q16, Q17]), "depth" : 1.6 * mm, "offsetDistance" : 25 * mm});
        }
        {
            var Q0;
            Q0=makeQuery(id+"F0.imprint","IMPRINT",FACE,{"disambiguationData":[TD([[makeQuery(id+"F0.imprint","IMPRINT",EDGE,{"derivedFrom":sQuery(id+"F0.wireOp",EDGE,"E1931.bottom")}),1.0]])]});
            extrude(context, id + "F2", {"entities" : qUnion([Q0]), "operationType" : NewBodyOperationType.ADD, "depth" : 3.2 * mm, "offsetDistance" : 25 * mm});
        }
        {
            var Q0;
            Q0=makeQuery(id+"F0.imprint","IMPRINT",FACE,{"disambiguationData":[TD([[makeQuery(id+"F0.imprint","IMPRINT",EDGE,{"derivedFrom":sQuery(id+"F0.wireOp",EDGE,"E3")}),-1.0]])]});
            var Q1;
            Q1=makeQuery(id+"F0.imprint","IMPRINT",FACE,{"disambiguationData":[TD([[makeQuery(id+"F0.imprint","IMPRINT",EDGE,{"derivedFrom":sQuery(id+"F0.wireOp",EDGE,"E264")}),-1.0]])]});
            var Q2;
            Q2=makeQuery(id+"F0.imprint","IMPRINT",FACE,{"disambiguationData":[TD([[makeQuery(id+"F0.imprint","IMPRINT",EDGE,{"derivedFrom":sQuery(id+"F0.wireOp",EDGE,"E275")}),-1.0]])]});
            var Q3;
            Q3=makeQuery(id+"F0.imprint","IMPRINT",FACE,{"disambiguationData":[TD([[makeQuery(id+"F0.imprint","IMPRINT",EDGE,{"derivedFrom":sQuery(id+"F0.wireOp",EDGE,"E411")}),-1.0]])]});
            var Q4;
            Q4=makeQuery(id+"F0.imprint","IMPRINT",FACE,{"disambiguationData":[TD([[makeQuery(id+"F0.imprint","IMPRINT",EDGE,{"derivedFrom":sQuery(id+"F0.wireOp",EDGE,"E716")}),-1.0]])]});
            var Q5;
            Q5=makeQuery(id+"F0.imprint","IMPRINT",FACE,{"disambiguationData":[TD([[makeQuery(id+"F0.imprint","IMPRINT",EDGE,{"derivedFrom":sQuery(id+"F0.wireOp",EDGE,"E740")}),-1.0]])]});
            var Q6;
            Q6=makeQuery(id+"F0.imprint","IMPRINT",FACE,{"disambiguationData":[TD([[makeQuery(id+"F0.imprint","IMPRINT",EDGE,{"derivedFrom":sQuery(id+"F0.wireOp",EDGE,"E919")}),-1.0]])]});
            var Q7;
            Q7=makeQuery(id+"F0.imprint","IMPRINT",FACE,{"disambiguationData":[TD([[makeQuery(id+"F0.imprint","IMPRINT",EDGE,{"derivedFrom":sQuery(id+"F0.wireOp",EDGE,"E1206")}),-1.0]])]});
            var Q8;
            Q8=makeQuery(id+"F0.imprint","IMPRINT",FACE,{"disambiguationData":[TD([[makeQuery(id+"F0.imprint","IMPRINT",EDGE,{"derivedFrom":sQuery(id+"F0.wireOp",EDGE,"E1215")}),-1.0]])]});
            var Q9;
            Q9=makeQuery(id+"F0.imprint","IMPRINT",FACE,{"disambiguationData":[TD([[makeQuery(id+"F0.imprint","IMPRINT",EDGE,{"derivedFrom":sQuery(id+"F0.wireOp",EDGE,"E1644")}),-1.0]])]});
            extrude(context, id + "F3", {"entities" : qUnion([Q0, Q1, Q2, Q3, Q4, Q5, Q6, Q7, Q8, Q9]), "operationType" : NewBodyOperationType.ADD, "depth" : 3 * mm, "offsetDistance" : 25 * mm});
        }
    });
